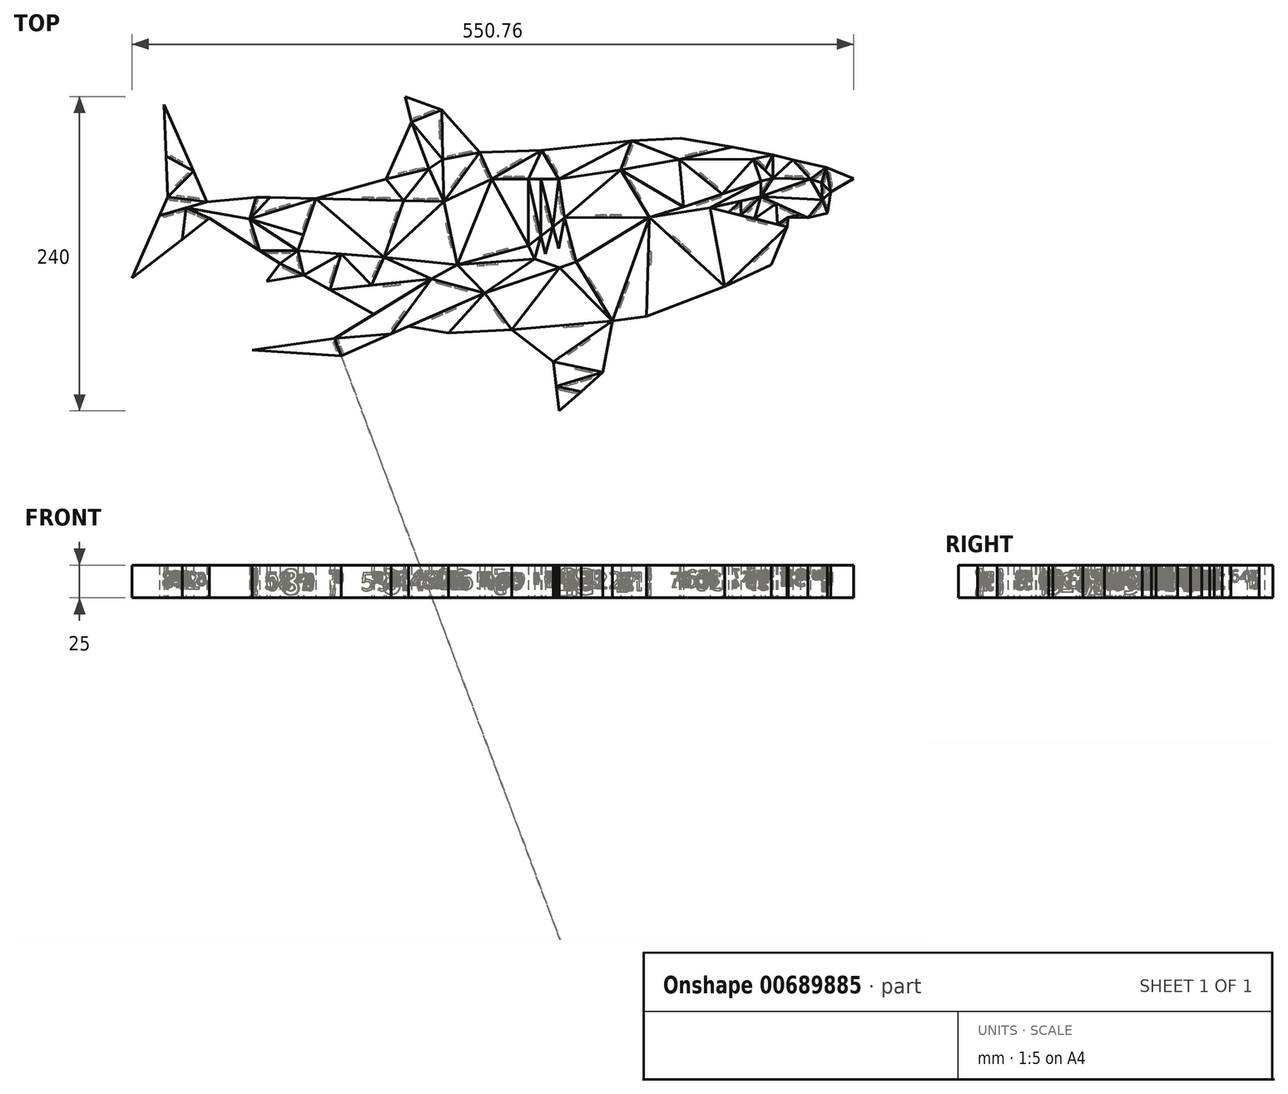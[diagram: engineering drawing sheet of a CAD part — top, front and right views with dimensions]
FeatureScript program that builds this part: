
annotation { "Feature Type Name" : "Feature", "Feature Type Description" : "" }
export const myFeature = defineFeature(function(context is Context, id is Id, definition is map)
    precondition{}
    {
        {
            var Q0;
            Q0=qCreatedBy(makeId("Top.planeOp"),FACE);
            var sketch = newSketch(context, id + "F0", { "sketchPlane" : qUnion([Q0])});
            skLineSegment(sketch, "E0.bottom", {"start": v(-560, -120) * mm, "end": v(560, -120) * mm});
            skLineSegment(sketch, "E0.top", {"start": v(-560, 120) * mm, "end": v(560, 120) * mm});
            skLineSegment(sketch, "E0.left", {"start": v(-560, -120) * mm, "end": v(-560, 120) * mm});
            skLineSegment(sketch, "E0.right", {"start": v(560, -120) * mm, "end": v(560, 120) * mm});
            skPoint(sketch, "E0.middle", {"position": v(0, 0) * mm});
            skLineSegment(sketch, "E1", {"start": v(0, 120) * mm, "end": v(0, -120) * mm});
            skLineSegment(sketch, "E2", {"start": v(-98.5, -25) * mm, "end": v(-62.96, -8.5) * mm});
            skLineSegment(sketch, "E3", {"start": v(-158.02, -47.81) * mm, "end": v(-98.5, -25) * mm});
            skLineSegment(sketch, "E4", {"start": v(-184.16, -51.15) * mm, "end": v(-158.02, -47.81) * mm});
            skLineSegment(sketch, "E5", {"start": v(-191.25, -90.42) * mm, "end": v(-184.16, -51.15) * mm});
            skLineSegment(sketch, "E6", {"start": v(-224.77, -120) * mm, "end": v(-191.25, -90.42) * mm});
            skLineSegment(sketch, "E7", {"start": v(-229.22, -82.3) * mm, "end": v(-224.77, -120) * mm});
            skLineSegment(sketch, "E8", {"start": v(-260.93, -57.82) * mm, "end": v(-229.22, -82.3) * mm});
            skLineSegment(sketch, "E9", {"start": v(-309.32, -60.6) * mm, "end": v(-260.93, -57.82) * mm});
            skLineSegment(sketch, "E10", {"start": v(-458.96, -73.4) * mm, "end": v(-391.1, -77.85) * mm});
            skLineSegment(sketch, "E11", {"start": v(-396.1, -64.5) * mm, "end": v(-458.96, -73.4) * mm});
            skLineSegment(sketch, "E12", {"start": v(-399.7, -27.56) * mm, "end": v(-366.14, -46.09) * mm});
            skLineSegment(sketch, "E13", {"start": v(-419.75, -16.22) * mm, "end": v(-399.7, -27.56) * mm});
            skLineSegment(sketch, "E14", {"start": v(-437.83, -7.4) * mm, "end": v(-419.75, -16.22) * mm});
            skLineSegment(sketch, "E15", {"start": v(-491.8, 27.08) * mm, "end": v(-437.83, -7.4) * mm});
            skLineSegment(sketch, "E16", {"start": v(-526.26, 113.86) * mm, "end": v(-523.5, 43.21) * mm});
            skLineSegment(sketch, "E17", {"start": v(-493.56, 39.57) * mm, "end": v(-526.26, 113.86) * mm});
            skLineSegment(sketch, "E18", {"start": v(-456.3, 42.91) * mm, "end": v(-493.56, 39.57) * mm});
            skLineSegment(sketch, "E19", {"start": v(-445.4, 43.06) * mm, "end": v(-456.3, 42.91) * mm});
            skLineSegment(sketch, "E20", {"start": v(-410.31, 42.07) * mm, "end": v(-445.4, 43.06) * mm});
            skLineSegment(sketch, "E21", {"start": v(-356.91, 57.1) * mm, "end": v(-410.31, 42.07) * mm});
            skLineSegment(sketch, "E22", {"start": v(-337.47, 100.57) * mm, "end": v(-356.91, 57.1) * mm});
            skLineSegment(sketch, "E23", {"start": v(-342.14, 120) * mm, "end": v(-337.47, 100.57) * mm});
            skLineSegment(sketch, "E24", {"start": v(-314.33, 109.61) * mm, "end": v(-342.14, 120) * mm});
            skLineSegment(sketch, "E25", {"start": v(-285.4, 77.35) * mm, "end": v(-314.33, 109.61) * mm});
            skLineSegment(sketch, "E26", {"start": v(-238.12, 79.02) * mm, "end": v(-285.4, 77.35) * mm});
            skLineSegment(sketch, "E27", {"start": v(-169.37, 86.33) * mm, "end": v(-238.12, 79.02) * mm});
            skLineSegment(sketch, "E28", {"start": v(-169.37, 86.33) * mm, "end": v(-132.1, 88) * mm});
            skLineSegment(sketch, "E29", {"start": v(-550.76, -18.53) * mm, "end": v(-491.8, 27.08) * mm});
            skLineSegment(sketch, "E30", {"start": v(-523.5, 43.21) * mm, "end": v(-550.76, -18.53) * mm});
            skLineSegment(sketch, "E31", {"start": v(-314.33, 109.61) * mm, "end": v(-337.47, 100.57) * mm});
            skLineSegment(sketch, "E32", {"start": v(-313.66, 71.78) * mm, "end": v(-285.4, 77.35) * mm});
            skLineSegment(sketch, "E33", {"start": v(-313.66, 71.78) * mm, "end": v(-314.33, 109.61) * mm});
            skLineSegment(sketch, "E34", {"start": v(-313.66, 71.78) * mm, "end": v(-337.47, 100.57) * mm});
            skLineSegment(sketch, "E35", {"start": v(-324.1, 64.88) * mm, "end": v(-313.66, 71.78) * mm});
            skLineSegment(sketch, "E36", {"start": v(-324.1, 64.88) * mm, "end": v(-356.91, 57.1) * mm});
            skLineSegment(sketch, "E37", {"start": v(-324.1, 64.88) * mm, "end": v(-337.47, 100.57) * mm});
            skLineSegment(sketch, "E38", {"start": v(-396.1, -64.5) * mm, "end": v(-391.1, -77.85) * mm});
            skLineSegment(sketch, "E39", {"start": v(-208.01, -105.2) * mm, "end": v(-227, -101.15) * mm});
            skLineSegment(sketch, "E40", {"start": v(-229.22, -82.3) * mm, "end": v(-184.16, -51.15) * mm});
            skLineSegment(sketch, "E41", {"start": v(-191.25, -90.42) * mm, "end": v(-229.22, -82.3) * mm});
            skLineSegment(sketch, "E42", {"start": v(-281.5, -30.01) * mm, "end": v(-391.1, -77.85) * mm});
            skLineSegment(sketch, "E43", {"start": v(-396.1, -64.5) * mm, "end": v(-353.1, -61.27) * mm});
            skLineSegment(sketch, "E44", {"start": v(-322.17, -19.07) * mm, "end": v(-396.1, -64.5) * mm});
            skLineSegment(sketch, "E45", {"start": v(-322.17, -19.07) * mm, "end": v(-353.1, -61.27) * mm});
            skLineSegment(sketch, "E46", {"start": v(-184.16, -51.15) * mm, "end": v(-260.93, -57.82) * mm});
            skLineSegment(sketch, "E47", {"start": v(-21, 65.86) * mm, "end": v(0, 57.32) * mm});
            skLineSegment(sketch, "E48", {"start": v(-61.42, 75.33) * mm, "end": v(-21, 65.86) * mm});
            skLineSegment(sketch, "E49", {"start": v(-92.6, 81.33) * mm, "end": v(-61.42, 75.33) * mm});
            skLineSegment(sketch, "E50", {"start": v(-132.1, 88) * mm, "end": v(-92.6, 81.33) * mm});
            skLineSegment(sketch, "E51", {"start": v(-17.51, 47.28) * mm, "end": v(0, 57.32) * mm});
            skLineSegment(sketch, "E52", {"start": v(-17.51, 47.28) * mm, "end": v(-19.9, 31) * mm});
            skLineSegment(sketch, "E53", {"start": v(-155.69, 27.8) * mm, "end": v(-158.02, -47.81) * mm});
            skLineSegment(sketch, "E54", {"start": v(-155.69, 27.8) * mm, "end": v(-98.5, -25) * mm});
            skLineSegment(sketch, "E55", {"start": v(-177.9, 64) * mm, "end": v(-155.69, 27.8) * mm});
            skLineSegment(sketch, "E56", {"start": v(-177.9, 64) * mm, "end": v(-169.37, 86.33) * mm});
            skLineSegment(sketch, "E57", {"start": v(-17.51, 47.28) * mm, "end": v(-21, 65.86) * mm});
            skLineSegment(sketch, "E58", {"start": v(-34.99, 27.4) * mm, "end": v(-19.9, 31) * mm});
            skLineSegment(sketch, "E59", {"start": v(-49.9, 27.93) * mm, "end": v(-34.99, 27.4) * mm});
            skLineSegment(sketch, "E60", {"start": v(-49.9, 27.93) * mm, "end": v(-50.83, 20.55) * mm});
            skLineSegment(sketch, "E61", {"start": v(-50.83, 20.55) * mm, "end": v(-62.96, -8.5) * mm});
            skLineSegment(sketch, "E62", {"start": v(-50.83, 20.55) * mm, "end": v(-98.5, -25) * mm});
            skLineSegment(sketch, "E63", {"start": v(-109.43, 35.16) * mm, "end": v(-98.5, -25) * mm});
            skLineSegment(sketch, "E64", {"start": v(-109.43, 35.16) * mm, "end": v(-50.83, 20.55) * mm});
            skLineSegment(sketch, "E65", {"start": v(-70.86, 43.59) * mm, "end": v(-34.99, 27.4) * mm});
            skLineSegment(sketch, "E66", {"start": v(-70.86, 43.59) * mm, "end": v(-109.43, 35.16) * mm});
            skLineSegment(sketch, "E67", {"start": v(-503.89, 63.04) * mm, "end": v(-524.72, 74.56) * mm});
            skLineSegment(sketch, "E68", {"start": v(-523.5, 43.21) * mm, "end": v(-503.89, 63.04) * mm});
            skLineSegment(sketch, "E69", {"start": v(-493.56, 39.57) * mm, "end": v(-523.5, 43.21) * mm});
            skLineSegment(sketch, "E70", {"start": v(-509.57, 34.94) * mm, "end": v(-493.56, 39.57) * mm});
            skLineSegment(sketch, "E71", {"start": v(-509.57, 34.94) * mm, "end": v(-491.8, 27.08) * mm});
            skLineSegment(sketch, "E72", {"start": v(-509.57, 34.94) * mm, "end": v(-529.73, 29.1) * mm});
            skLineSegment(sketch, "E73", {"start": v(-509.57, 34.94) * mm, "end": v(-512.54, 11.03) * mm});
            skLineSegment(sketch, "E74", {"start": v(-509.57, 34.94) * mm, "end": v(-461.04, 26.47) * mm});
            skLineSegment(sketch, "E75", {"start": v(-461.04, 26.47) * mm, "end": v(-456.3, 42.91) * mm});
            skLineSegment(sketch, "E76", {"start": v(-445.4, 43.06) * mm, "end": v(-461.04, 26.47) * mm});
            skLineSegment(sketch, "E77", {"start": v(-447.94, -21.09) * mm, "end": v(-437.83, -7.4) * mm});
            skLineSegment(sketch, "E78", {"start": v(-447.94, -21.09) * mm, "end": v(-419.75, -16.22) * mm});
            skLineSegment(sketch, "E79", {"start": v(-461.04, 26.47) * mm, "end": v(-453.35, 2.5) * mm});
            skLineSegment(sketch, "E80", {"start": v(-461.04, 26.47) * mm, "end": v(-410.31, 42.07) * mm});
            skLineSegment(sketch, "E81", {"start": v(-322.17, -19.07) * mm, "end": v(-281.5, -30.01) * mm});
            skLineSegment(sketch, "E82", {"start": v(-260.93, -57.82) * mm, "end": v(-281.5, -30.01) * mm});
            skLineSegment(sketch, "E83", {"start": v(-281.5, -30.01) * mm, "end": v(-309.32, -60.6) * mm});
            skLineSegment(sketch, "E84", {"start": v(-155.69, 27.8) * mm, "end": v(-109.43, 35.16) * mm});
            skLineSegment(sketch, "E85", {"start": v(-155.69, 27.8) * mm, "end": v(-129.84, 35.74) * mm});
            skLineSegment(sketch, "E86", {"start": v(-85.88, 40.3) * mm, "end": v(-85.88, 29.29) * mm});
            skLineSegment(sketch, "E87", {"start": v(-85.88, 29.29) * mm, "end": v(-70.86, 43.59) * mm});
            skLineSegment(sketch, "E88", {"start": v(-70.86, 43.59) * mm, "end": v(-75.52, 26.7) * mm});
            skLineSegment(sketch, "E89", {"start": v(-58.19, 22.38) * mm, "end": v(-49.9, 27.93) * mm});
            skLineSegment(sketch, "E90", {"start": v(-49.9, 27.93) * mm, "end": v(-40.47, 29.87) * mm});
            skLineSegment(sketch, "E91", {"start": v(-17.51, 47.28) * mm, "end": v(-23.8, 41.06) * mm});
            skLineSegment(sketch, "E92", {"start": v(-23.8, 41.06) * mm, "end": v(-34.99, 27.4) * mm});
            skLineSegment(sketch, "E93", {"start": v(-23.8, 41.06) * mm, "end": v(-19.9, 31) * mm});
            skLineSegment(sketch, "E94", {"start": v(-23.8, 41.06) * mm, "end": v(-70.86, 43.59) * mm});
            skLineSegment(sketch, "E95", {"start": v(-24.49, 54.25) * mm, "end": v(-21, 65.86) * mm});
            skLineSegment(sketch, "E96", {"start": v(-24.49, 54.25) * mm, "end": v(-23.8, 41.06) * mm});
            skLineSegment(sketch, "E97", {"start": v(-33, 57) * mm, "end": v(-21, 65.86) * mm});
            skLineSegment(sketch, "E98", {"start": v(-33, 57) * mm, "end": v(-24.49, 54.25) * mm});
            skLineSegment(sketch, "E99", {"start": v(-33, 57) * mm, "end": v(-23.8, 41.06) * mm});
            skLineSegment(sketch, "E100", {"start": v(-70.86, 43.59) * mm, "end": v(-70.86, 55.35) * mm});
            skLineSegment(sketch, "E101", {"start": v(-109.43, 35.16) * mm, "end": v(-70.86, 55.35) * mm});
            skLineSegment(sketch, "E102", {"start": v(-129.84, 35.74) * mm, "end": v(-70.86, 55.35) * mm});
            skLineSegment(sketch, "E103", {"start": v(-129.84, 35.74) * mm, "end": v(-177.9, 64) * mm});
            skLineSegment(sketch, "E104", {"start": v(-129.84, 35.74) * mm, "end": v(-132.83, 71.97) * mm});
            skLineSegment(sketch, "E105", {"start": v(-132.83, 71.97) * mm, "end": v(-169.37, 86.33) * mm});
            skLineSegment(sketch, "E106", {"start": v(-177.9, 64) * mm, "end": v(-132.83, 71.97) * mm});
            skLineSegment(sketch, "E107", {"start": v(-132.83, 71.97) * mm, "end": v(-92.6, 81.33) * mm});
            skLineSegment(sketch, "E108", {"start": v(-76.54, 72.24) * mm, "end": v(-61.42, 75.33) * mm});
            skLineSegment(sketch, "E109", {"start": v(-76.54, 72.24) * mm, "end": v(-132.83, 71.97) * mm});
            skLineSegment(sketch, "E110", {"start": v(-76.54, 72.24) * mm, "end": v(-70.86, 55.35) * mm});
            skLineSegment(sketch, "E111", {"start": v(-132.83, 71.97) * mm, "end": v(-100.35, 45.54) * mm});
            skLineSegment(sketch, "E112", {"start": v(-61.42, 57.63) * mm, "end": v(-70.86, 55.35) * mm});
            skLineSegment(sketch, "E113", {"start": v(-61.42, 57.63) * mm, "end": v(-33, 57) * mm});
            skLineSegment(sketch, "E114", {"start": v(-61.42, 57.63) * mm, "end": v(-61.42, 75.33) * mm});
            skLineSegment(sketch, "E115", {"start": v(-61.42, 57.63) * mm, "end": v(-76.54, 72.24) * mm});
            skLineSegment(sketch, "E116", {"start": v(-61.42, 75.33) * mm, "end": v(-67.65, 63.65) * mm});
            skLineSegment(sketch, "E117", {"start": v(-61.42, 57.63) * mm, "end": v(-46.15, 71.75) * mm});
            skLineSegment(sketch, "E118", {"start": v(-225.14, 56.85) * mm, "end": v(-177.9, 64) * mm});
            skLineSegment(sketch, "E119", {"start": v(-225.14, 56.85) * mm, "end": v(-238.12, 79.02) * mm});
            skLineSegment(sketch, "E120", {"start": v(-225.14, 56.85) * mm, "end": v(-169.37, 86.33) * mm});
            skLineSegment(sketch, "E121", {"start": v(-276.28, 56.87) * mm, "end": v(-285.4, 77.35) * mm});
            skLineSegment(sketch, "E122", {"start": v(-276.28, 56.87) * mm, "end": v(-225.14, 56.85) * mm});
            skLineSegment(sketch, "E123", {"start": v(-238.12, 79.02) * mm, "end": v(-276.28, 56.87) * mm});
            skLineSegment(sketch, "E124", {"start": v(-312.55, 39.84) * mm, "end": v(-313.66, 71.78) * mm});
            skLineSegment(sketch, "E125", {"start": v(-312.55, 39.84) * mm, "end": v(-276.28, 56.87) * mm});
            skLineSegment(sketch, "E126", {"start": v(-312.55, 39.84) * mm, "end": v(-285.4, 77.35) * mm});
            skLineSegment(sketch, "E127", {"start": v(-302.43, -8.43) * mm, "end": v(-276.28, 56.87) * mm});
            skLineSegment(sketch, "E128", {"start": v(-302.43, -8.43) * mm, "end": v(-281.5, -30.01) * mm});
            skLineSegment(sketch, "E129", {"start": v(-302.43, -8.43) * mm, "end": v(-322.17, -19.07) * mm});
            skLineSegment(sketch, "E130", {"start": v(-302.43, -8.43) * mm, "end": v(-312.55, 39.84) * mm});
            skLineSegment(sketch, "E131", {"start": v(-302.43, -8.43) * mm, "end": v(-248.23, 6.09) * mm});
            skLineSegment(sketch, "E132", {"start": v(-248.23, 6.09) * mm, "end": v(-276.28, 56.87) * mm});
            skLineSegment(sketch, "E133", {"start": v(-184.16, -51.15) * mm, "end": v(-155.69, 27.8) * mm});
            skLineSegment(sketch, "E134", {"start": v(-248.23, 6.09) * mm, "end": v(-220.7, 27.33) * mm});
            skLineSegment(sketch, "E135", {"start": v(-220.7, 27.33) * mm, "end": v(-155.69, 27.8) * mm});
            skLineSegment(sketch, "E136", {"start": v(-211.69, -6.17) * mm, "end": v(-155.69, 27.8) * mm});
            skLineSegment(sketch, "E137", {"start": v(-211.69, -6.17) * mm, "end": v(-220.7, 27.33) * mm});
            skLineSegment(sketch, "E138", {"start": v(-225.14, 56.85) * mm, "end": v(-220.7, 27.33) * mm});
            skLineSegment(sketch, "E139", {"start": v(-260.93, -57.82) * mm, "end": v(-224.52, -10.66) * mm});
            skLineSegment(sketch, "E140", {"start": v(-224.52, -10.66) * mm, "end": v(-184.16, -51.15) * mm});
            skLineSegment(sketch, "E141", {"start": v(-224.52, -10.66) * mm, "end": v(-211.69, -6.17) * mm});
            skLineSegment(sketch, "E142", {"start": v(-211.69, -6.17) * mm, "end": v(-184.16, -51.15) * mm});
            skLineSegment(sketch, "E143", {"start": v(-248.23, 6.09) * mm, "end": v(-248.23, 56.86) * mm});
            skLineSegment(sketch, "E144", {"start": v(-238.12, 79.02) * mm, "end": v(-248.23, 56.86) * mm});
            skLineSegment(sketch, "E145", {"start": v(-224.52, -10.66) * mm, "end": v(-243.56, -4.04) * mm});
            skLineSegment(sketch, "E146", {"start": v(-243.56, -4.04) * mm, "end": v(-248.23, 6.09) * mm});
            skLineSegment(sketch, "E147", {"start": v(-281.5, -30.01) * mm, "end": v(-243.56, -4.04) * mm});
            skLineSegment(sketch, "E148", {"start": v(-343.48, 40.35) * mm, "end": v(-410.31, 42.07) * mm});
            skLineSegment(sketch, "E149", {"start": v(-324.1, 64.88) * mm, "end": v(-343.48, 40.35) * mm});
            skLineSegment(sketch, "E150", {"start": v(-343.48, 40.35) * mm, "end": v(-356.91, 57.1) * mm});
            skLineSegment(sketch, "E151", {"start": v(-324.1, 64.88) * mm, "end": v(-312.55, 39.84) * mm});
            skLineSegment(sketch, "E152", {"start": v(-343.48, 40.35) * mm, "end": v(-312.55, 39.84) * mm});
            skLineSegment(sketch, "E153", {"start": v(-399.7, -27.56) * mm, "end": v(-322.17, -19.07) * mm});
            skLineSegment(sketch, "E154", {"start": v(-309.32, -60.6) * mm, "end": v(-339.75, -55.44) * mm});
            skLineSegment(sketch, "E155", {"start": v(-358.3, -2.7) * mm, "end": v(-322.17, -19.07) * mm});
            skLineSegment(sketch, "E156", {"start": v(-358.3, -2.7) * mm, "end": v(-302.43, -8.43) * mm});
            skLineSegment(sketch, "E157", {"start": v(-343.48, 40.35) * mm, "end": v(-358.3, -2.7) * mm});
            skLineSegment(sketch, "E158", {"start": v(-358.3, -2.7) * mm, "end": v(-410.31, 42.07) * mm});
            skLineSegment(sketch, "E159", {"start": v(-453.35, 2.5) * mm, "end": v(-424.06, 2.5) * mm});
            skLineSegment(sketch, "E160", {"start": v(-424.06, 2.5) * mm, "end": v(-419.75, -16.22) * mm});
            skLineSegment(sketch, "E161", {"start": v(-424.06, 2.5) * mm, "end": v(-437.83, -7.4) * mm});
            skLineSegment(sketch, "E162", {"start": v(-424.06, 2.5) * mm, "end": v(-410.31, 42.07) * mm});
            skLineSegment(sketch, "E163", {"start": v(-461.04, 26.47) * mm, "end": v(-419.87, 14.57) * mm});
            skLineSegment(sketch, "E164", {"start": v(-424.06, 2.5) * mm, "end": v(-358.3, -2.7) * mm});
            skLineSegment(sketch, "E165", {"start": v(-419.75, -16.22) * mm, "end": v(-391.18, -0.1) * mm});
            skLineSegment(sketch, "E166", {"start": v(-391.18, -0.1) * mm, "end": v(-399.7, -27.56) * mm});
            skLineSegment(sketch, "E167", {"start": v(-58.19, 22.38) * mm, "end": v(-58.84, 38.16) * mm});
            skLineSegment(sketch, "E168", {"start": v(-58.84, 38.16) * mm, "end": v(-75.52, 26.7) * mm});
            skLineSegment(sketch, "E169", {"start": v(-200.98, -99) * mm, "end": v(-21, -99) * mm});
            skLineSegment(sketch, "E170", {"start": v(-21, -99) * mm, "end": v(0, -120) * mm});
            skLineSegment(sketch, "E171", {"start": v(-21, -99) * mm, "end": v(-21, 30.74) * mm});
            skLineSegment(sketch, "E172", {"start": v(-21, 99) * mm, "end": v(-21, 65.86) * mm});
            skLineSegment(sketch, "E173", {"start": v(-21, 99) * mm, "end": v(0, 120) * mm});
            skLineSegment(sketch, "E174", {"start": v(-21, 99) * mm, "end": v(-304.81, 99) * mm});
            skLineSegment(sketch, "E175", {"start": v(-519.72, 99) * mm, "end": v(-338.17, 99) * mm});
            skLineSegment(sketch, "E176", {"start": v(-539, 99) * mm, "end": v(-525.68, 99) * mm});
            skLineSegment(sketch, "E177", {"start": v(-539, 99) * mm, "end": v(-560, 120) * mm});
            skLineSegment(sketch, "E178", {"start": v(-539, -99) * mm, "end": v(-539, -9.44) * mm});
            skLineSegment(sketch, "E179", {"start": v(-539, -99) * mm, "end": v(-227.25, -99) * mm});
            skLineSegment(sketch, "E180", {"start": v(-539, -99) * mm, "end": v(-560, -120) * mm});
            skLineSegment(sketch, "E181", {"start": v(-539, 99) * mm, "end": v(-539, 8.1) * mm});
            skLineSegment(sketch, "E182", {"start": v(-238.79, 13.37) * mm, "end": v(-248.23, 56.86) * mm});
            skLineSegment(sketch, "E183", {"start": v(-238.79, 13.37) * mm, "end": v(-243.56, -4.04) * mm});
            skLineSegment(sketch, "E184", {"start": v(-238.79, 56.86) * mm, "end": v(-238.79, 13.37) * mm});
            skLineSegment(sketch, "E185", {"start": v(-238.79, 56.86) * mm, "end": v(-229.63, 20.44) * mm});
            skLineSegment(sketch, "E186", {"start": v(-229.63, 20.44) * mm, "end": v(-225.14, 56.85) * mm});
            skLineSegment(sketch, "E187", {"start": v(-220.7, 27.33) * mm, "end": v(-225.14, 4.02) * mm});
            skLineSegment(sketch, "E188", {"start": v(-225.14, 4.02) * mm, "end": v(-229.63, 20.44) * mm});
            skLineSegment(sketch, "E189", {"start": v(-238.79, 13.37) * mm, "end": v(-235.13, 0) * mm});
            skLineSegment(sketch, "E190", {"start": v(-235.13, 0) * mm, "end": v(-229.63, 20.44) * mm});
            skLineSegment(sketch, "E191", {"start": v(-76.54, 72.24) * mm, "end": v(-100.35, 45.54) * mm});
            skLineSegment(sketch, "E192", {"start": v(-46.15, 71.75) * mm, "end": v(-33, 57) * mm});
            skLineSegment(sketch, "E193", {"start": v(-70.86, 43.59) * mm, "end": v(-33, 57) * mm});
            skLineSegment(sketch, "E194", {"start": v(-220.7, 27.33) * mm, "end": v(-177.9, 64) * mm});
            skLineSegment(sketch, "E195", {"start": v(-302.43, -8.43) * mm, "end": v(-243.56, -4.04) * mm});
            skLineSegment(sketch, "E196", {"start": v(-281.5, -30.01) * mm, "end": v(-224.52, -10.66) * mm});
            skLineSegment(sketch, "E197", {"start": v(-312.55, 39.84) * mm, "end": v(-358.3, -2.7) * mm});
            skLineSegment(sketch, "E198", {"start": v(-358.3, -2.7) * mm, "end": v(-367.99, -24.09) * mm});
            skLineSegment(sketch, "E199", {"start": v(-367.99, -24.09) * mm, "end": v(-391.18, -0.1) * mm});
            skLineSegment(sketch, "E200", {"start": v(-191.25, -90.42) * mm, "end": v(-227, -101.15) * mm});
            skLineSegment(sketch, "E201", {"start": v(-17.51, 47.28) * mm, "end": v(-24.49, 54.25) * mm});
            skLineSegment(sketch, "E202", {"start": v(-85.88, 40.3) * mm, "end": v(-95.55, 31.7) * mm});
            skLineSegment(sketch, "E203", {"start": v(-70.86, 43.59) * mm, "end": v(-61.42, 57.63) * mm});
            skLineSegment(sketch, "E204", {"start": v(-461.04, 26.47) * mm, "end": v(-424.06, 2.5) * mm});
            skSolve(sketch);
        }
        {
            var Q0;
            {var subQ0=sQuery(id+"F0.wireOp",EDGE,"E67");Q0=makeQuery(id+"F0.imprint","IMPRINT",FACE,{"disambiguationData":[TD([[makeQuery(id+"F0.imprint","IMPRINT",EDGE,{"derivedFrom":subQ0}),-1.0]])]});}
            var Q1;
            {var subQ2=sQuery(id+"F0.wireOp",EDGE,"E68");Q1=makeQuery(id+"F0.imprint","IMPRINT",FACE,{"disambiguationData":[TD([[makeQuery(id+"F0.imprint","IMPRINT",EDGE,{"derivedFrom":subQ2}),-1.0]])]});}
            var Q2;
            {var subQ0=sQuery(id+"F0.wireOp",EDGE,"E72");Q2=makeQuery(id+"F0.imprint","IMPRINT",FACE,{"disambiguationData":[TD([[makeQuery(id+"F0.imprint","IMPRINT",EDGE,{"derivedFrom":subQ0}),1.0]])]});}
            var Q3;
            {var subQ0=sQuery(id+"F0.wireOp",EDGE,"E71");Q3=makeQuery(id+"F0.imprint","IMPRINT",FACE,{"disambiguationData":[TD([[makeQuery(id+"F0.imprint","IMPRINT",EDGE,{"derivedFrom":subQ0}),1.0]])]});}
            var Q4;
            Q4=makeQuery(id+"F0.imprint","IMPRINT",FACE,{"disambiguationData":[TD([[makeQuery(id+"F0.imprint","IMPRINT",EDGE,{"derivedFrom":sQuery(id+"F0.wireOp",EDGE,"E19")}),1.0]])]});
            var Q5;
            {var subQ0=sQuery(id+"F0.wireOp",EDGE,"E80");Q5=makeQuery(id+"F0.imprint","IMPRINT",FACE,{"disambiguationData":[TD([[makeQuery(id+"F0.imprint","IMPRINT",EDGE,{"derivedFrom":subQ0}),-1.0]])]});}
            var Q6;
            {var subQ2=sQuery(id+"F0.wireOp",EDGE,"E159");Q6=makeQuery(id+"F0.imprint","IMPRINT",FACE,{"disambiguationData":[TD([[makeQuery(id+"F0.imprint","IMPRINT",EDGE,{"derivedFrom":subQ2}),-1.0]])]});}
            var Q7;
            Q7=makeQuery(id+"F0.imprint","IMPRINT",FACE,{"disambiguationData":[TD([[makeQuery(id+"F0.imprint","IMPRINT",EDGE,{"derivedFrom":sQuery(id+"F0.wireOp",EDGE,"E14")}),-1.0]])]});
            var Q8;
            Q8=makeQuery(id+"F0.imprint","IMPRINT",FACE,{"disambiguationData":[TD([[makeQuery(id+"F0.imprint","IMPRINT",EDGE,{"derivedFrom":sQuery(id+"F0.wireOp",EDGE,"E13")}),1.0]])]});
            var Q9;
            Q9=makeQuery(id+"F0.imprint","IMPRINT",FACE,{"disambiguationData":[TD([[makeQuery(id+"F0.imprint","IMPRINT",EDGE,{"derivedFrom":sQuery(id+"F0.wireOp",EDGE,"E148")}),1.0]])]});
            var Q10;
            Q10=makeQuery(id+"F0.imprint","IMPRINT",FACE,{"disambiguationData":[TD([[makeQuery(id+"F0.imprint","IMPRINT",EDGE,{"derivedFrom":sQuery(id+"F0.wireOp",EDGE,"E23")}),1.0]])]});
            var Q11;
            {var subQ3=sQuery(id+"F0.wireOp",EDGE,"E36");Q11=makeQuery(id+"F0.imprint","IMPRINT",FACE,{"disambiguationData":[TD([[makeQuery(id+"F0.imprint","IMPRINT",EDGE,{"derivedFrom":subQ3}),-1.0]])]});}
            var Q12;
            Q12=makeQuery(id+"F0.imprint","IMPRINT",FACE,{"disambiguationData":[TD([[makeQuery(id+"F0.imprint","IMPRINT",EDGE,{"derivedFrom":sQuery(id+"F0.wireOp",EDGE,"E149")}),1.0]])]});
            var Q13;
            {var subQ0=sQuery(id+"F0.wireOp",EDGE,"E198");Q13=makeQuery(id+"F0.imprint","IMPRINT",FACE,{"disambiguationData":[TD([[makeQuery(id+"F0.imprint","IMPRINT",EDGE,{"derivedFrom":subQ0}),-1.0]])]});}
            var Q14;
            {var subQ0=sQuery(id+"F0.wireOp",EDGE,"E12");Q14=makeQuery(id+"F0.imprint","IMPRINT",FACE,{"disambiguationData":[TD([[makeQuery(id+"F0.imprint","IMPRINT",EDGE,{"derivedFrom":subQ0}),1.0]])]});}
            var Q15;
            {var subQ0=sQuery(id+"F0.wireOp",EDGE,"E38");Q15=makeQuery(id+"F0.imprint","IMPRINT",FACE,{"disambiguationData":[TD([[makeQuery(id+"F0.imprint","IMPRINT",EDGE,{"derivedFrom":subQ0}),1.0]])]});}
            var Q16;
            {var subQ3=sQuery(id+"F0.wireOp",EDGE,"E45");Q16=makeQuery(id+"F0.imprint","IMPRINT",FACE,{"disambiguationData":[TD([[makeQuery(id+"F0.imprint","IMPRINT",EDGE,{"derivedFrom":subQ3}),1.0]])]});}
            var Q17;
            Q17=makeQuery(id+"F0.imprint","IMPRINT",FACE,{"disambiguationData":[TD([[makeQuery(id+"F0.imprint","IMPRINT",EDGE,{"derivedFrom":sQuery(id+"F0.wireOp",EDGE,"E130")}),1.0]])]});
            var Q18;
            {var subQ0=sQuery(id+"F0.wireOp",EDGE,"E32");Q18=makeQuery(id+"F0.imprint","IMPRINT",FACE,{"disambiguationData":[TD([[makeQuery(id+"F0.imprint","IMPRINT",EDGE,{"derivedFrom":subQ0}),1.0]])]});}
            var Q19;
            Q19=makeQuery(id+"F0.imprint","IMPRINT",FACE,{"disambiguationData":[TD([[makeQuery(id+"F0.imprint","IMPRINT",EDGE,{"derivedFrom":sQuery(id+"F0.wireOp",EDGE,"E121")}),1.0]])]});
            var Q20;
            Q20=makeQuery(id+"F0.imprint","IMPRINT",FACE,{"disambiguationData":[TD([[makeQuery(id+"F0.imprint","IMPRINT",EDGE,{"derivedFrom":sQuery(id+"F0.wireOp",EDGE,"E127")}),-1.0]])]});
            var Q21;
            {var subQ0=sQuery(id+"F0.wireOp",EDGE,"E123");Q21=makeQuery(id+"F0.imprint","IMPRINT",FACE,{"disambiguationData":[TD([[makeQuery(id+"F0.imprint","IMPRINT",EDGE,{"derivedFrom":subQ0}),1.0]])]});}
            var Q22;
            Q22=makeQuery(id+"F0.imprint","IMPRINT",FACE,{"disambiguationData":[TD([[makeQuery(id+"F0.imprint","IMPRINT",EDGE,{"derivedFrom":sQuery(id+"F0.wireOp",EDGE,"E128")}),1.0]])]});
            var Q23;
            Q23=makeQuery(id+"F0.imprint","IMPRINT",FACE,{"disambiguationData":[TD([[makeQuery(id+"F0.imprint","IMPRINT",EDGE,{"derivedFrom":sQuery(id+"F0.wireOp",EDGE,"E9")}),1.0]])]});
            var Q24;
            {var subQ3=sQuery(id+"F0.wireOp",EDGE,"E39");Q24=makeQuery(id+"F0.imprint","IMPRINT",FACE,{"disambiguationData":[TD([[makeQuery(id+"F0.imprint","IMPRINT",EDGE,{"derivedFrom":subQ3}),1.0]])]});}
            var Q25;
            {var subQ0=sQuery(id+"F0.wireOp",EDGE,"E41");Q25=makeQuery(id+"F0.imprint","IMPRINT",FACE,{"disambiguationData":[TD([[makeQuery(id+"F0.imprint","IMPRINT",EDGE,{"derivedFrom":subQ0}),1.0]])]});}
            var Q26;
            Q26=makeQuery(id+"F0.imprint","IMPRINT",FACE,{"disambiguationData":[TD([[makeQuery(id+"F0.imprint","IMPRINT",EDGE,{"derivedFrom":sQuery(id+"F0.wireOp",EDGE,"E8")}),1.0]])]});
            var Q27;
            Q27=makeQuery(id+"F0.imprint","IMPRINT",FACE,{"disambiguationData":[TD([[makeQuery(id+"F0.imprint","IMPRINT",EDGE,{"derivedFrom":sQuery(id+"F0.wireOp",EDGE,"E137")}),1.0]])]});
            var Q28;
            {var subQ0=sQuery(id+"F0.wireOp",EDGE,"E143");Q28=makeQuery(id+"F0.imprint","IMPRINT",FACE,{"disambiguationData":[TD([[makeQuery(id+"F0.imprint","IMPRINT",EDGE,{"derivedFrom":subQ0}),-1.0]])]});}
            var Q29;
            {var subQ0=sQuery(id+"F0.wireOp",EDGE,"E184");Q29=makeQuery(id+"F0.imprint","IMPRINT",FACE,{"disambiguationData":[TD([[makeQuery(id+"F0.imprint","IMPRINT",EDGE,{"derivedFrom":subQ0}),1.0]])]});}
            var Q30;
            {var subQ0=sQuery(id+"F0.wireOp",EDGE,"E138");Q30=makeQuery(id+"F0.imprint","IMPRINT",FACE,{"disambiguationData":[TD([[makeQuery(id+"F0.imprint","IMPRINT",EDGE,{"derivedFrom":subQ0}),-1.0]])]});}
            var Q31;
            Q31=makeQuery(id+"F0.imprint","IMPRINT",FACE,{"disambiguationData":[TD([[makeQuery(id+"F0.imprint","IMPRINT",EDGE,{"derivedFrom":sQuery(id+"F0.wireOp",EDGE,"E27")}),1.0]])]});
            var Q32;
            Q32=makeQuery(id+"F0.imprint","IMPRINT",FACE,{"disambiguationData":[TD([[makeQuery(id+"F0.imprint","IMPRINT",EDGE,{"derivedFrom":sQuery(id+"F0.wireOp",EDGE,"E56")}),-1.0]])]});
            var Q33;
            Q33=makeQuery(id+"F0.imprint","IMPRINT",FACE,{"disambiguationData":[TD([[makeQuery(id+"F0.imprint","IMPRINT",EDGE,{"derivedFrom":sQuery(id+"F0.wireOp",EDGE,"E55")}),-1.0]])]});
            var Q34;
            Q34=makeQuery(id+"F0.imprint","IMPRINT",FACE,{"disambiguationData":[TD([[makeQuery(id+"F0.imprint","IMPRINT",EDGE,{"derivedFrom":sQuery(id+"F0.wireOp",EDGE,"E133")}),1.0]])]});
            var Q35;
            Q35=makeQuery(id+"F0.imprint","IMPRINT",FACE,{"disambiguationData":[TD([[makeQuery(id+"F0.imprint","IMPRINT",EDGE,{"derivedFrom":sQuery(id+"F0.wireOp",EDGE,"E3")}),1.0]])]});
            var Q36;
            Q36=makeQuery(id+"F0.imprint","IMPRINT",FACE,{"disambiguationData":[TD([[makeQuery(id+"F0.imprint","IMPRINT",EDGE,{"derivedFrom":sQuery(id+"F0.wireOp",EDGE,"E84")}),1.0]])]});
            var Q37;
            {var subQ4=sQuery(id+"F0.wireOp",EDGE,"E62");Q37=makeQuery(id+"F0.imprint","IMPRINT",FACE,{"disambiguationData":[TD([[makeQuery(id+"F0.imprint","IMPRINT",EDGE,{"derivedFrom":subQ4}),-1.0]])]});}
            var Q38;
            Q38=makeQuery(id+"F0.imprint","IMPRINT",FACE,{"disambiguationData":[TD([[makeQuery(id+"F0.imprint","IMPRINT",EDGE,{"derivedFrom":sQuery(id+"F0.wireOp",EDGE,"E109")}),1.0]])]});
            var Q39;
            {var subQ0=sQuery(id+"F0.wireOp",EDGE,"E108");Q39=makeQuery(id+"F0.imprint","IMPRINT",FACE,{"disambiguationData":[TD([[makeQuery(id+"F0.imprint","IMPRINT",EDGE,{"derivedFrom":subQ0}),-1.0]])]});}
            var Q40;
            Q40=makeQuery(id+"F0.imprint","IMPRINT",FACE,{"disambiguationData":[TD([[makeQuery(id+"F0.imprint","IMPRINT",EDGE,{"derivedFrom":sQuery(id+"F0.wireOp",EDGE,"E100")}),-1.0]])]});
            var Q41;
            {var subQ2=sQuery(id+"F0.wireOp",EDGE,"E86");Q41=makeQuery(id+"F0.imprint","IMPRINT",FACE,{"disambiguationData":[TD([[makeQuery(id+"F0.imprint","IMPRINT",EDGE,{"derivedFrom":subQ2}),1.0]])]});}
            var Q42;
            {var subQ0=sQuery(id+"F0.wireOp",EDGE,"E88");Q42=makeQuery(id+"F0.imprint","IMPRINT",FACE,{"disambiguationData":[TD([[makeQuery(id+"F0.imprint","IMPRINT",EDGE,{"derivedFrom":subQ0}),1.0]])]});}
            var Q43;
            Q43=makeQuery(id+"F0.imprint","IMPRINT",FACE,{"disambiguationData":[TD([[makeQuery(id+"F0.imprint","IMPRINT",EDGE,{"derivedFrom":sQuery(id+"F0.wireOp",EDGE,"E89")}),1.0]])]});
            var Q44;
            Q44=makeQuery(id+"F0.imprint","IMPRINT",FACE,{"disambiguationData":[TD([[makeQuery(id+"F0.imprint","IMPRINT",EDGE,{"derivedFrom":sQuery(id+"F0.wireOp",EDGE,"E94")}),-1.0]])]});
            var Q45;
            Q45=makeQuery(id+"F0.imprint","IMPRINT",FACE,{"disambiguationData":[TD([[makeQuery(id+"F0.imprint","IMPRINT",EDGE,{"derivedFrom":sQuery(id+"F0.wireOp",EDGE,"E113")}),1.0]])]});
            var Q46;
            Q46=makeQuery(id+"F0.imprint","IMPRINT",FACE,{"disambiguationData":[TD([[makeQuery(id+"F0.imprint","IMPRINT",EDGE,{"derivedFrom":sQuery(id+"F0.wireOp",EDGE,"E95")}),1.0]])]});
            var Q47;
            Q47=makeQuery(id+"F0.imprint","IMPRINT",FACE,{"disambiguationData":[TD([[makeQuery(id+"F0.imprint","IMPRINT",EDGE,{"derivedFrom":sQuery(id+"F0.wireOp",EDGE,"E47")}),-1.0]])]});
            var Q48;
            Q48=makeQuery(id+"F0.imprint","IMPRINT",FACE,{"disambiguationData":[TD([[makeQuery(id+"F0.imprint","IMPRINT",EDGE,{"derivedFrom":sQuery(id+"F0.wireOp",EDGE,"E91")}),-1.0]])]});
            var Q49;
            {var subQ0=sQuery(id+"F0.wireOp",EDGE,"E92");Q49=makeQuery(id+"F0.imprint","IMPRINT",FACE,{"disambiguationData":[TD([[makeQuery(id+"F0.imprint","IMPRINT",EDGE,{"derivedFrom":subQ0}),1.0]])]});}
            extrude(context, id + "F1", {"entities" : qUnion([Q0, Q1, Q2, Q3, Q4, Q5, Q6, Q7, Q8, Q9, Q10, Q11, Q12, Q13, Q14, Q15, Q16, Q17, Q18, Q19, Q20, Q21, Q22, Q23, Q24, Q25, Q26, Q27, Q28, Q29, Q30, Q31, Q32, Q33, Q34, Q35, Q36, Q37, Q38, Q39, Q40, Q41, Q42, Q43, Q44, Q45, Q46, Q47, Q48, Q49]), "depth" : 25 * mm, "offsetDistance" : 25 * mm});
        }
        {
            var Q0;
            {var subQ2=sQuery(id+"F0.wireOp",EDGE,"E67");Q0=makeQuery(id+"F0.imprint","IMPRINT",FACE,{"disambiguationData":[TD([[makeQuery(id+"F0.imprint","IMPRINT",EDGE,{"derivedFrom":subQ2}),1.0]])]});}
            var Q1;
            {var subQ0=sQuery(id+"F0.wireOp",EDGE,"E69");Q1=makeQuery(id+"F0.imprint","IMPRINT",FACE,{"disambiguationData":[TD([[makeQuery(id+"F0.imprint","IMPRINT",EDGE,{"derivedFrom":subQ0}),1.0]])]});}
            var Q2;
            {var subQ0=sQuery(id+"F0.wireOp",EDGE,"E71");Q2=makeQuery(id+"F0.imprint","IMPRINT",FACE,{"disambiguationData":[TD([[makeQuery(id+"F0.imprint","IMPRINT",EDGE,{"derivedFrom":subQ0}),-1.0]])]});}
            var Q3;
            Q3=makeQuery(id+"F0.imprint","IMPRINT",FACE,{"disambiguationData":[TD([[makeQuery(id+"F0.imprint","IMPRINT",EDGE,{"derivedFrom":sQuery(id+"F0.wireOp",EDGE,"E20")}),1.0]])]});
            var Q4;
            Q4=makeQuery(id+"F0.imprint","IMPRINT",FACE,{"disambiguationData":[TD([[makeQuery(id+"F0.imprint","IMPRINT",EDGE,{"derivedFrom":sQuery(id+"F0.wireOp",EDGE,"E14")}),1.0]])]});
            var Q5;
            {var subQ0=sQuery(id+"F0.wireOp",EDGE,"E166");Q5=makeQuery(id+"F0.imprint","IMPRINT",FACE,{"disambiguationData":[TD([[makeQuery(id+"F0.imprint","IMPRINT",EDGE,{"derivedFrom":subQ0}),1.0]])]});}
            var Q6;
            {var subQ0=sQuery(id+"F0.wireOp",EDGE,"E155");Q6=makeQuery(id+"F0.imprint","IMPRINT",FACE,{"disambiguationData":[TD([[makeQuery(id+"F0.imprint","IMPRINT",EDGE,{"derivedFrom":subQ0}),-1.0]])]});}
            var Q7;
            Q7=makeQuery(id+"F0.imprint","IMPRINT",FACE,{"disambiguationData":[TD([[makeQuery(id+"F0.imprint","IMPRINT",EDGE,{"derivedFrom":sQuery(id+"F0.wireOp",EDGE,"E152")}),-1.0]])]});
            var Q8;
            Q8=makeQuery(id+"F0.imprint","IMPRINT",FACE,{"disambiguationData":[TD([[makeQuery(id+"F0.imprint","IMPRINT",EDGE,{"derivedFrom":sQuery(id+"F0.wireOp",EDGE,"E21")}),1.0]])]});
            var Q9;
            Q9=makeQuery(id+"F0.imprint","IMPRINT",FACE,{"disambiguationData":[TD([[makeQuery(id+"F0.imprint","IMPRINT",EDGE,{"derivedFrom":sQuery(id+"F0.wireOp",EDGE,"E31")}),1.0]])]});
            var Q10;
            Q10=makeQuery(id+"F0.imprint","IMPRINT",FACE,{"disambiguationData":[TD([[makeQuery(id+"F0.imprint","IMPRINT",EDGE,{"derivedFrom":sQuery(id+"F0.wireOp",EDGE,"E32")}),-1.0]])]});
            var Q11;
            Q11=makeQuery(id+"F0.imprint","IMPRINT",FACE,{"disambiguationData":[TD([[makeQuery(id+"F0.imprint","IMPRINT",EDGE,{"derivedFrom":sQuery(id+"F0.wireOp",EDGE,"E125")}),-1.0]])]});
            var Q12;
            Q12=makeQuery(id+"F0.imprint","IMPRINT",FACE,{"disambiguationData":[TD([[makeQuery(id+"F0.imprint","IMPRINT",EDGE,{"derivedFrom":sQuery(id+"F0.wireOp",EDGE,"E10")}),1.0]])]});
            var Q13;
            {var subQ0=sQuery(id+"F0.wireOp",EDGE,"E43");Q13=makeQuery(id+"F0.imprint","IMPRINT",FACE,{"disambiguationData":[TD([[makeQuery(id+"F0.imprint","IMPRINT",EDGE,{"derivedFrom":subQ0}),1.0]])]});}
            var Q14;
            Q14=makeQuery(id+"F0.imprint","IMPRINT",FACE,{"disambiguationData":[TD([[makeQuery(id+"F0.imprint","IMPRINT",EDGE,{"derivedFrom":sQuery(id+"F0.wireOp",EDGE,"E81")}),1.0]])]});
            var Q15;
            {var subQ0=sQuery(id+"F0.wireOp",EDGE,"E83");Q15=makeQuery(id+"F0.imprint","IMPRINT",FACE,{"disambiguationData":[TD([[makeQuery(id+"F0.imprint","IMPRINT",EDGE,{"derivedFrom":subQ0}),-1.0]])]});}
            var Q16;
            Q16=makeQuery(id+"F0.imprint","IMPRINT",FACE,{"disambiguationData":[TD([[makeQuery(id+"F0.imprint","IMPRINT",EDGE,{"derivedFrom":sQuery(id+"F0.wireOp",EDGE,"E131")}),-1.0]])]});
            var Q17;
            Q17=makeQuery(id+"F0.imprint","IMPRINT",FACE,{"disambiguationData":[TD([[makeQuery(id+"F0.imprint","IMPRINT",EDGE,{"derivedFrom":sQuery(id+"F0.wireOp",EDGE,"E82")}),-1.0]])]});
            var Q18;
            Q18=makeQuery(id+"F0.imprint","IMPRINT",FACE,{"disambiguationData":[TD([[makeQuery(id+"F0.imprint","IMPRINT",EDGE,{"derivedFrom":sQuery(id+"F0.wireOp",EDGE,"E140")}),1.0]])]});
            var Q19;
            Q19=makeQuery(id+"F0.imprint","IMPRINT",FACE,{"disambiguationData":[TD([[makeQuery(id+"F0.imprint","IMPRINT",EDGE,{"derivedFrom":sQuery(id+"F0.wireOp",EDGE,"E5")}),1.0]])]});
            var Q20;
            {var subQ0=sQuery(id+"F0.wireOp",EDGE,"E39");Q20=makeQuery(id+"F0.imprint","IMPRINT",FACE,{"disambiguationData":[TD([[makeQuery(id+"F0.imprint","IMPRINT",EDGE,{"derivedFrom":subQ0}),-1.0]])]});}
            var Q21;
            Q21=makeQuery(id+"F0.imprint","IMPRINT",FACE,{"disambiguationData":[TD([[makeQuery(id+"F0.imprint","IMPRINT",EDGE,{"derivedFrom":sQuery(id+"F0.wireOp",EDGE,"E4")}),1.0]])]});
            var Q22;
            Q22=makeQuery(id+"F0.imprint","IMPRINT",FACE,{"disambiguationData":[TD([[makeQuery(id+"F0.imprint","IMPRINT",EDGE,{"derivedFrom":sQuery(id+"F0.wireOp",EDGE,"E135")}),-1.0]])]});
            var Q23;
            {var subQ0=sQuery(id+"F0.wireOp",EDGE,"E187");Q23=makeQuery(id+"F0.imprint","IMPRINT",FACE,{"disambiguationData":[TD([[makeQuery(id+"F0.imprint","IMPRINT",EDGE,{"derivedFrom":subQ0}),-1.0]])]});}
            var Q24;
            {var subQ0=sQuery(id+"F0.wireOp",EDGE,"E189");Q24=makeQuery(id+"F0.imprint","IMPRINT",FACE,{"disambiguationData":[TD([[makeQuery(id+"F0.imprint","IMPRINT",EDGE,{"derivedFrom":subQ0}),1.0]])]});}
            var Q25;
            {var subQ0=sQuery(id+"F0.wireOp",EDGE,"E132");Q25=makeQuery(id+"F0.imprint","IMPRINT",FACE,{"disambiguationData":[TD([[makeQuery(id+"F0.imprint","IMPRINT",EDGE,{"derivedFrom":subQ0}),-1.0]])]});}
            var Q26;
            {var subQ0=sQuery(id+"F0.wireOp",EDGE,"E182");Q26=makeQuery(id+"F0.imprint","IMPRINT",FACE,{"disambiguationData":[TD([[makeQuery(id+"F0.imprint","IMPRINT",EDGE,{"derivedFrom":subQ0}),-1.0]])]});}
            var Q27;
            {var subQ2=sQuery(id+"F0.wireOp",EDGE,"E185");Q27=makeQuery(id+"F0.imprint","IMPRINT",FACE,{"disambiguationData":[TD([[makeQuery(id+"F0.imprint","IMPRINT",EDGE,{"derivedFrom":subQ2}),1.0]])]});}
            var Q28;
            Q28=makeQuery(id+"F0.imprint","IMPRINT",FACE,{"disambiguationData":[TD([[makeQuery(id+"F0.imprint","IMPRINT",EDGE,{"derivedFrom":sQuery(id+"F0.wireOp",EDGE,"E26")}),1.0]])]});
            var Q29;
            Q29=makeQuery(id+"F0.imprint","IMPRINT",FACE,{"disambiguationData":[TD([[makeQuery(id+"F0.imprint","IMPRINT",EDGE,{"derivedFrom":sQuery(id+"F0.wireOp",EDGE,"E118")}),-1.0]])]});
            var Q30;
            Q30=makeQuery(id+"F0.imprint","IMPRINT",FACE,{"disambiguationData":[TD([[makeQuery(id+"F0.imprint","IMPRINT",EDGE,{"derivedFrom":sQuery(id+"F0.wireOp",EDGE,"E28")}),-1.0]])]});
            var Q31;
            Q31=makeQuery(id+"F0.imprint","IMPRINT",FACE,{"disambiguationData":[TD([[makeQuery(id+"F0.imprint","IMPRINT",EDGE,{"derivedFrom":sQuery(id+"F0.wireOp",EDGE,"E55")}),1.0]])]});
            var Q32;
            {var subQ0=sQuery(id+"F0.wireOp",EDGE,"E104");Q32=makeQuery(id+"F0.imprint","IMPRINT",FACE,{"disambiguationData":[TD([[makeQuery(id+"F0.imprint","IMPRINT",EDGE,{"derivedFrom":subQ0}),-1.0]])]});}
            var Q33;
            Q33=makeQuery(id+"F0.imprint","IMPRINT",FACE,{"disambiguationData":[TD([[makeQuery(id+"F0.imprint","IMPRINT",EDGE,{"derivedFrom":sQuery(id+"F0.wireOp",EDGE,"E54")}),1.0]])]});
            var Q34;
            {var subQ0=sQuery(id+"F0.wireOp",EDGE,"E110");Q34=makeQuery(id+"F0.imprint","IMPRINT",FACE,{"disambiguationData":[TD([[makeQuery(id+"F0.imprint","IMPRINT",EDGE,{"derivedFrom":subQ0}),-1.0]])]});}
            var Q35;
            {var subQ0=sQuery(id+"F0.wireOp",EDGE,"E100");Q35=makeQuery(id+"F0.imprint","IMPRINT",FACE,{"disambiguationData":[TD([[makeQuery(id+"F0.imprint","IMPRINT",EDGE,{"derivedFrom":subQ0}),1.0]])]});}
            var Q36;
            {var subQ0=sQuery(id+"F0.wireOp",EDGE,"E86");Q36=makeQuery(id+"F0.imprint","IMPRINT",FACE,{"disambiguationData":[TD([[makeQuery(id+"F0.imprint","IMPRINT",EDGE,{"derivedFrom":subQ0}),-1.0]])]});}
            var Q37;
            {var subQ0=sQuery(id+"F0.wireOp",EDGE,"E87");Q37=makeQuery(id+"F0.imprint","IMPRINT",FACE,{"disambiguationData":[TD([[makeQuery(id+"F0.imprint","IMPRINT",EDGE,{"derivedFrom":subQ0}),-1.0]])]});}
            var Q38;
            {var subQ2=sQuery(id+"F0.wireOp",EDGE,"E167");Q38=makeQuery(id+"F0.imprint","IMPRINT",FACE,{"disambiguationData":[TD([[makeQuery(id+"F0.imprint","IMPRINT",EDGE,{"derivedFrom":subQ2}),1.0]])]});}
            var Q39;
            {var subQ0=sQuery(id+"F0.wireOp",EDGE,"E114");Q39=makeQuery(id+"F0.imprint","IMPRINT",FACE,{"disambiguationData":[TD([[makeQuery(id+"F0.imprint","IMPRINT",EDGE,{"derivedFrom":subQ0}),1.0]])]});}
            var Q40;
            {var subQ0=sQuery(id+"F0.wireOp",EDGE,"E97");Q40=makeQuery(id+"F0.imprint","IMPRINT",FACE,{"disambiguationData":[TD([[makeQuery(id+"F0.imprint","IMPRINT",EDGE,{"derivedFrom":subQ0}),1.0]])]});}
            var Q41;
            Q41=makeQuery(id+"F0.imprint","IMPRINT",FACE,{"disambiguationData":[TD([[makeQuery(id+"F0.imprint","IMPRINT",EDGE,{"derivedFrom":sQuery(id+"F0.wireOp",EDGE,"E57")}),1.0]])]});
            var Q42;
            Q42=makeQuery(id+"F0.imprint","IMPRINT",FACE,{"disambiguationData":[TD([[makeQuery(id+"F0.imprint","IMPRINT",EDGE,{"derivedFrom":sQuery(id+"F0.wireOp",EDGE,"E52")}),-1.0]])]});
            var Q43;
            Q43=makeQuery(id+"F0.imprint","IMPRINT",FACE,{"disambiguationData":[TD([[makeQuery(id+"F0.imprint","IMPRINT",EDGE,{"derivedFrom":sQuery(id+"F0.wireOp",EDGE,"E96")}),-1.0]])]});
            var Q44;
            Q44=makeQuery(id+"F0.imprint","IMPRINT",FACE,{"disambiguationData":[TD([[makeQuery(id+"F0.imprint","IMPRINT",EDGE,{"derivedFrom":sQuery(id+"F0.wireOp",EDGE,"E113")}),-1.0]])]});
            var Q45;
            {var subQ0=sQuery(id+"F0.wireOp",EDGE,"E92");Q45=makeQuery(id+"F0.imprint","IMPRINT",FACE,{"disambiguationData":[TD([[makeQuery(id+"F0.imprint","IMPRINT",EDGE,{"derivedFrom":subQ0}),-1.0]])]});}
            var Q46;
            Q46=makeQuery(id+"F0.imprint","IMPRINT",FACE,{"disambiguationData":[TD([[makeQuery(id+"F0.imprint","IMPRINT",EDGE,{"derivedFrom":sQuery(id+"F0.wireOp",EDGE,"E2")}),1.0]])]});
            var Q47;
            {var subQ0=sQuery(id+"F0.wireOp",EDGE,"E60");Q47=makeQuery(id+"F0.imprint","IMPRINT",FACE,{"disambiguationData":[TD([[makeQuery(id+"F0.imprint","IMPRINT",EDGE,{"derivedFrom":subQ0}),-1.0]])]});}
            extrude(context, id + "F2", {"entities" : qUnion([Q0, Q1, Q2, Q3, Q4, Q5, Q6, Q7, Q8, Q9, Q10, Q11, Q12, Q13, Q14, Q15, Q16, Q17, Q18, Q19, Q20, Q21, Q22, Q23, Q24, Q25, Q26, Q27, Q28, Q29, Q30, Q31, Q32, Q33, Q34, Q35, Q36, Q37, Q38, Q39, Q40, Q41, Q42, Q43, Q44, Q45, Q46, Q47]), "depth" : 25 * mm, "offsetDistance" : 25 * mm});
        }
        {
            var Q0;
            Q0=makeQuery(id+"F0.imprint","IMPRINT",FACE,{"disambiguationData":[TD([[makeQuery(id+"F0.imprint","IMPRINT",EDGE,{"derivedFrom":sQuery(id+"F0.wireOp",EDGE,"E18")}),1.0]])]});
            var Q1;
            Q1=makeQuery(id+"F0.imprint","IMPRINT",FACE,{"disambiguationData":[TD([[makeQuery(id+"F0.imprint","IMPRINT",EDGE,{"derivedFrom":sQuery(id+"F0.wireOp",EDGE,"E79")}),1.0]])]});
            var Q2;
            {var subQ5=sQuery(id+"F0.wireOp",EDGE,"E158");Q2=makeQuery(id+"F0.imprint","IMPRINT",FACE,{"disambiguationData":[TD([[makeQuery(id+"F0.imprint","IMPRINT",EDGE,{"derivedFrom":subQ5}),1.0]])]});}
            var Q3;
            Q3=makeQuery(id+"F0.imprint","IMPRINT",FACE,{"disambiguationData":[TD([[makeQuery(id+"F0.imprint","IMPRINT",EDGE,{"derivedFrom":sQuery(id+"F0.wireOp",EDGE,"E36")}),1.0]])]});
            var Q4;
            Q4=makeQuery(id+"F0.imprint","IMPRINT",FACE,{"disambiguationData":[TD([[makeQuery(id+"F0.imprint","IMPRINT",EDGE,{"derivedFrom":sQuery(id+"F0.wireOp",EDGE,"E34")}),1.0]])]});
            var Q5;
            Q5=makeQuery(id+"F0.imprint","IMPRINT",FACE,{"disambiguationData":[TD([[makeQuery(id+"F0.imprint","IMPRINT",EDGE,{"derivedFrom":sQuery(id+"F0.wireOp",EDGE,"E129")}),-1.0]])]});
            var Q6;
            {var subQ0=sQuery(id+"F0.wireOp",EDGE,"E119");Q6=makeQuery(id+"F0.imprint","IMPRINT",FACE,{"disambiguationData":[TD([[makeQuery(id+"F0.imprint","IMPRINT",EDGE,{"derivedFrom":subQ0}),1.0]])]});}
            var Q7;
            {var subQ0=sQuery(id+"F0.wireOp",EDGE,"E146");Q7=makeQuery(id+"F0.imprint","IMPRINT",FACE,{"disambiguationData":[TD([[makeQuery(id+"F0.imprint","IMPRINT",EDGE,{"derivedFrom":subQ0}),-1.0]])]});}
            var Q8;
            Q8=makeQuery(id+"F0.imprint","IMPRINT",FACE,{"disambiguationData":[TD([[makeQuery(id+"F0.imprint","IMPRINT",EDGE,{"derivedFrom":sQuery(id+"F0.wireOp",EDGE,"E145")}),1.0]])]});
            var Q9;
            Q9=makeQuery(id+"F0.imprint","IMPRINT",FACE,{"disambiguationData":[TD([[makeQuery(id+"F0.imprint","IMPRINT",EDGE,{"derivedFrom":sQuery(id+"F0.wireOp",EDGE,"E46")}),-1.0]])]});
            var Q10;
            Q10=makeQuery(id+"F0.imprint","IMPRINT",FACE,{"disambiguationData":[TD([[makeQuery(id+"F0.imprint","IMPRINT",EDGE,{"derivedFrom":sQuery(id+"F0.wireOp",EDGE,"E56")}),1.0]])]});
            var Q11;
            Q11=makeQuery(id+"F0.imprint","IMPRINT",FACE,{"disambiguationData":[TD([[makeQuery(id+"F0.imprint","IMPRINT",EDGE,{"derivedFrom":sQuery(id+"F0.wireOp",EDGE,"E103")}),-1.0]])]});
            var Q12;
            Q12=makeQuery(id+"F0.imprint","IMPRINT",FACE,{"disambiguationData":[TD([[makeQuery(id+"F0.imprint","IMPRINT",EDGE,{"derivedFrom":sQuery(id+"F0.wireOp",EDGE,"E49")}),-1.0]])]});
            var Q13;
            {var subQ0=sQuery(id+"F0.wireOp",EDGE,"E110");Q13=makeQuery(id+"F0.imprint","IMPRINT",FACE,{"disambiguationData":[TD([[makeQuery(id+"F0.imprint","IMPRINT",EDGE,{"derivedFrom":subQ0}),1.0]])]});}
            var Q14;
            {var subQ0=sQuery(id+"F0.wireOp",EDGE,"E114");Q14=makeQuery(id+"F0.imprint","IMPRINT",FACE,{"disambiguationData":[TD([[makeQuery(id+"F0.imprint","IMPRINT",EDGE,{"derivedFrom":subQ0}),-1.0]])]});}
            var Q15;
            {var subQ3=sQuery(id+"F0.wireOp",EDGE,"E202");Q15=makeQuery(id+"F0.imprint","IMPRINT",FACE,{"disambiguationData":[TD([[makeQuery(id+"F0.imprint","IMPRINT",EDGE,{"derivedFrom":subQ3}),-1.0]])]});}
            var Q16;
            {var subQ0=sQuery(id+"F0.wireOp",EDGE,"E59");Q16=makeQuery(id+"F0.imprint","IMPRINT",FACE,{"disambiguationData":[TD([[makeQuery(id+"F0.imprint","IMPRINT",EDGE,{"derivedFrom":subQ0}),1.0]])]});}
            extrude(context, id + "F3", {"entities" : qUnion([Q0, Q1, Q2, Q3, Q4, Q5, Q6, Q7, Q8, Q9, Q10, Q11, Q12, Q13, Q14, Q15, Q16]), "depth" : 25 * mm, "offsetDistance" : 25 * mm});
        }
        {
            var Q0;
            {var subQ2=sQuery(id+"F0.wireOp",EDGE,"E163");Q0=makeQuery(id+"F0.imprint","IMPRINT",FACE,{"disambiguationData":[TD([[makeQuery(id+"F0.imprint","IMPRINT",EDGE,{"derivedFrom":subQ2}),-1.0]])]});}
            var Q1;
            {var subQ0=sQuery(id+"F0.wireOp",EDGE,"E160");Q1=makeQuery(id+"F0.imprint","IMPRINT",FACE,{"disambiguationData":[TD([[makeQuery(id+"F0.imprint","IMPRINT",EDGE,{"derivedFrom":subQ0}),1.0]])]});}
            var Q2;
            Q2=makeQuery(id+"F0.imprint","IMPRINT",FACE,{"disambiguationData":[TD([[makeQuery(id+"F0.imprint","IMPRINT",EDGE,{"derivedFrom":sQuery(id+"F0.wireOp",EDGE,"E35")}),-1.0]])]});
            extrude(context, id + "F4", {"entities" : qUnion([Q0, Q1, Q2]), "depth" : 25 * mm, "offsetDistance" : 25 * mm});
        }
        {
            var Q0;
            Q0=makeQuery(id+"F1.opExtrude","SWEPT_BODY",BODY,{"disambiguationData":[OSD([sQuery(id+"F0.wireOp",EDGE,"E3"),sQuery(id+"F0.wireOp",EDGE,"E53"),sQuery(id+"F0.wireOp",EDGE,"E54")])]});
            transform(context, id + "F5", {"entities" : qUnion([Q0]), "transformType" : TransformType.TRANSLATION_3D, "dx" : 0 * mm, "dy" : 0 * mm, "dz" : 0 * mm, "makeCopy" : true});
        }
        {
            var Q0;
            Q0=makeQuery(id+"F1.opExtrude","SWEPT_FACE",FACE,{"disambiguationData":[OSD([sQuery(id+"F0.wireOp",EDGE,"E53")])]});
            var sketch = newSketch(context, id + "F6", { "sketchPlane" : qUnion([Q0])});
            skText(sketch, "E205", { "text": "1", "fontName": "OpenSans-Bold.ttf"});
            const initialGuessF6  = {"E205": [0.00121, 0.00172, 1, 0, 0.02117]};
            skSetInitialGuess(sketch, initialGuessF6);
            skSolve(sketch);
        }
        {
            var Q0;
            Q0 = qSketchRegion(id + "F6", true);
            extrude(context, id + "F7", {"entities" : qUnion([Q0]), "operationType" : NewBodyOperationType.REMOVE, "oppositeDirection" : true, "depth" : 2 * mm, "offsetDistance" : 25 * mm});
        }
        {
            var Q0;
            Q0=makeQuery(id+"F1.opExtrude","SWEPT_FACE",FACE,{"disambiguationData":[OSD([sQuery(id+"F0.wireOp",EDGE,"E39")])]});
            var sketch = newSketch(context, id + "F8", { "sketchPlane" : qUnion([Q0])});
            skText(sketch, "E206", { "text": "2", "fontName": "OpenSans-Bold.ttf"});
            const initialGuessF8  = {"E206": [0.18333, 0.0017, 1, 0, 0.02096]};
            skSetInitialGuess(sketch, initialGuessF8);
            skSolve(sketch);
        }
        {
            var Q0;
            Q0=makeQuery(id+"F8.imprint","IMPRINT",FACE,{"disambiguationData":[TD([[makeQuery(id+"F8.imprint","IMPRINT",EDGE,{"derivedFrom":sQuery(id+"F8.wireOp",EDGE,"E206.sketch_text.stroke-0")}),-1.0]])]});
            extrude(context, id + "F9", {"entities" : qUnion([Q0]), "operationType" : NewBodyOperationType.REMOVE, "oppositeDirection" : true, "depth" : 2 * mm, "offsetDistance" : 25 * mm});
        }
        {
            var Q0;
            Q0=makeQuery(id+"F1.opExtrude","SWEPT_FACE",FACE,{"disambiguationData":[OSD([sQuery(id+"F0.wireOp",EDGE,"E41")])]});
            var sketch = newSketch(context, id + "F10", { "sketchPlane" : qUnion([Q0])});
            skText(sketch, "E207", { "text": "3", "fontName": "OpenSans-Bold.ttf"});
            const initialGuessF10  = {"E207": [0.17496, 0.00268, 1, 0, 0.01956]};
            skSetInitialGuess(sketch, initialGuessF10);
            skSolve(sketch);
        }
        {
            var Q0;
            Q0=makeQuery(id+"F10.imprint","IMPRINT",FACE,{"disambiguationData":[TD([[makeQuery(id+"F10.imprint","IMPRINT",EDGE,{"derivedFrom":sQuery(id+"F10.wireOp",EDGE,"E207.sketch_text.stroke-0")}),-1.0]])]});
            extrude(context, id + "F11", {"entities" : qUnion([Q0]), "operationType" : NewBodyOperationType.REMOVE, "oppositeDirection" : true, "depth" : 2 * mm, "offsetDistance" : 25 * mm});
        }
        {
            var Q0;
            Q0=makeQuery(id+"F1.opExtrude","SWEPT_FACE",FACE,{"disambiguationData":[OSD([sQuery(id+"F0.wireOp",EDGE,"E46")])]});
            var sketch = newSketch(context, id + "F12", { "sketchPlane" : qUnion([Q0])});
            skText(sketch, "E208", { "text": "4", "fontName": "OpenSans-Bold.ttf"});
            const initialGuessF12  = {"E208": [0.2097, 0.00235, 1, 0, 0.02013]};
            skSetInitialGuess(sketch, initialGuessF12);
            skSolve(sketch);
        }
        {
            var Q0;
            Q0=makeQuery(id+"F12.imprint","IMPRINT",FACE,{"disambiguationData":[TD([[makeQuery(id+"F12.imprint","IMPRINT",EDGE,{"derivedFrom":sQuery(id+"F12.wireOp",EDGE,"E208.sketch_text.stroke-0")}),-1.0]])]});
            extrude(context, id + "F13", {"entities" : qUnion([Q0]), "operationType" : NewBodyOperationType.REMOVE, "oppositeDirection" : true, "depth" : 2 * mm, "offsetDistance" : 25 * mm});
        }
        {
            var Q0;
            Q0=makeQuery(id+"F1.opExtrude","SWEPT_FACE",FACE,{"disambiguationData":[OSD([sQuery(id+"F0.wireOp",EDGE,"E82")])]});
            var sketch = newSketch(context, id + "F14", { "sketchPlane" : qUnion([Q0])});
            skText(sketch, "E209", { "text": "5", "fontName": "OpenSans-Bold.ttf"});
            const initialGuessF14  = {"E209": [0.11513, 0.00267, 1, 0, 0.0192]};
            skSetInitialGuess(sketch, initialGuessF14);
            skSolve(sketch);
        }
        {
            var Q0;
            Q0=makeQuery(id+"F14.imprint","IMPRINT",FACE,{"disambiguationData":[TD([[makeQuery(id+"F14.imprint","IMPRINT",EDGE,{"derivedFrom":sQuery(id+"F14.wireOp",EDGE,"E209.sketch_text.stroke-0")}),-1.0]])]});
            extrude(context, id + "F15", {"entities" : qUnion([Q0]), "operationType" : NewBodyOperationType.REMOVE, "oppositeDirection" : true, "depth" : 2 * mm, "offsetDistance" : 25 * mm});
        }
        {
            var Q0;
            Q0=makeQuery(id+"F1.opExtrude","SWEPT_FACE",FACE,{"disambiguationData":[OSD([sQuery(id+"F0.wireOp",EDGE,"E153")])]});
            var sketch = newSketch(context, id + "F16", { "sketchPlane" : qUnion([Q0])});
            skText(sketch, "E210", { "text": "6", "fontName": "OpenSans-Bold.ttf"});
            const initialGuessF16  = {"E210": [0.34531, 0.003, 1, 0, 0.01905]};
            skSetInitialGuess(sketch, initialGuessF16);
            skSolve(sketch);
        }
        {
            var Q0;
            Q0=makeQuery(id+"F16.imprint","IMPRINT",FACE,{"disambiguationData":[TD([[makeQuery(id+"F16.imprint","IMPRINT",EDGE,{"derivedFrom":sQuery(id+"F16.wireOp",EDGE,"E210.sketch_text.stroke-0")}),-1.0]])]});
            extrude(context, id + "F17", {"entities" : qUnion([Q0]), "operationType" : NewBodyOperationType.REMOVE, "oppositeDirection" : true, "depth" : 2 * mm, "offsetDistance" : 25 * mm});
        }
        {
            var Q0;
            Q0=makeQuery(id+"F1.opExtrude","SWEPT_FACE",FACE,{"disambiguationData":[OSD([sQuery(id+"F0.wireOp",EDGE,"E166")])]});
            var sketch = newSketch(context, id + "F18", { "sketchPlane" : qUnion([Q0])});
            skText(sketch, "E211", { "text": "7", "fontName": "OpenSans-Bold.ttf"});
            const initialGuessF18  = {"E211": [-0.14042, 0.00212, 1, 0, 0.01955]};
            skSetInitialGuess(sketch, initialGuessF18);
            skSolve(sketch);
        }
        {
            var Q0;
            Q0=makeQuery(id+"F18.imprint","IMPRINT",FACE,{"disambiguationData":[TD([[makeQuery(id+"F18.imprint","IMPRINT",EDGE,{"derivedFrom":sQuery(id+"F18.wireOp",EDGE,"E211.sketch_text.stroke-0")}),-1.0]])]});
            extrude(context, id + "F19", {"entities" : qUnion([Q0]), "operationType" : NewBodyOperationType.REMOVE, "oppositeDirection" : true, "depth" : 2 * mm, "offsetDistance" : 25 * mm});
        }
        {
            var Q0;
            Q0=makeQuery(id+"F1.opExtrude","SWEPT_FACE",FACE,{"disambiguationData":[OSD([sQuery(id+"F0.wireOp",EDGE,"E14")])]});
            var sketch = newSketch(context, id + "F20", { "sketchPlane" : qUnion([Q0])});
            skText(sketch, "E212", { "text": "8", "fontName": "OpenSans-Bold.ttf"});
            const initialGuessF20  = {"E212": [0.37286, 0.00255, 1, 0, 0.0194]};
            skSetInitialGuess(sketch, initialGuessF20);
            skSolve(sketch);
        }
        {
            var Q0;
            Q0=makeQuery(id+"F20.imprint","IMPRINT",FACE,{"disambiguationData":[TD([[makeQuery(id+"F20.imprint","IMPRINT",EDGE,{"derivedFrom":sQuery(id+"F20.wireOp",EDGE,"E212.sketch_text.stroke-0")}),-1.0]])]});
            extrude(context, id + "F21", {"entities" : qUnion([Q0]), "operationType" : NewBodyOperationType.REMOVE, "oppositeDirection" : true, "depth" : 2 * mm, "offsetDistance" : 25 * mm});
        }
        {
            var Q0;
            Q0=makeQuery(id+"F1.opExtrude","SWEPT_FACE",FACE,{"disambiguationData":[OSD([sQuery(id+"F0.wireOp",EDGE,"E79")])]});
            var sketch = newSketch(context, id + "F22", { "sketchPlane" : qUnion([Q0])});
            skText(sketch, "E213", { "text": "9", "fontName": "OpenSans-Bold.ttf"});
            const initialGuessF22  = {"E213": [0.14422, 0.00248, 1, 0, 0.01863]};
            skSetInitialGuess(sketch, initialGuessF22);
            skSolve(sketch);
        }
        {
            var Q0;
            Q0=makeQuery(id+"F22.imprint","IMPRINT",FACE,{"disambiguationData":[TD([[makeQuery(id+"F22.imprint","IMPRINT",EDGE,{"derivedFrom":sQuery(id+"F22.wireOp",EDGE,"E213.sketch_text.stroke-0")}),-1.0]])]});
            extrude(context, id + "F23", {"entities" : qUnion([Q0]), "operationType" : NewBodyOperationType.REMOVE, "oppositeDirection" : true, "depth" : 2 * mm, "offsetDistance" : 25 * mm});
        }
        {
            var Q0;
            Q0=makeQuery(id+"F1.opExtrude","SWEPT_FACE",FACE,{"disambiguationData":[OSD([sQuery(id+"F0.wireOp",EDGE,"E159")])]});
            var sketch = newSketch(context, id + "F24", { "sketchPlane" : qUnion([Q0])});
            skText(sketch, "E214", { "text": "10", "fontName": "OpenSans-Bold.ttf"});
            const initialGuessF24  = {"E214": [0.42897, 0.00562, 1, 0, 0.01227]};
            skSetInitialGuess(sketch, initialGuessF24);
            skSolve(sketch);
        }
        {
            var Q0;
            Q0=makeQuery(id+"F24.imprint","IMPRINT",FACE,{"disambiguationData":[TD([[makeQuery(id+"F24.imprint","IMPRINT",EDGE,{"derivedFrom":sQuery(id+"F24.wireOp",EDGE,"E214.sketch_text.stroke-0")}),-1.0]])]});
            var Q1;
            Q1=makeQuery(id+"F24.imprint","IMPRINT",FACE,{"disambiguationData":[TD([[makeQuery(id+"F24.imprint","IMPRINT",EDGE,{"derivedFrom":sQuery(id+"F24.wireOp",EDGE,"E214.sketch_text.stroke-10")}),-1.0]])]});
            extrude(context, id + "F25", {"entities" : qUnion([Q0, Q1]), "operationType" : NewBodyOperationType.REMOVE, "oppositeDirection" : true, "depth" : 2 * mm, "offsetDistance" : 25 * mm});
        }
        {
            var Q0;
            Q0=makeQuery(id+"F1.opExtrude","SWEPT_FACE",FACE,{"disambiguationData":[OSD([sQuery(id+"F0.wireOp",EDGE,"E67")])]});
            var sketch = newSketch(context, id + "F26", { "sketchPlane" : qUnion([Q0])});
            skText(sketch, "E215", { "text": "11", "fontName": "AllertaStencil-Regular.ttf"});
            const initialGuessF26  = {"E215": [-0.49277, 0.00927, 1, 0, 0.01037]};
            skSetInitialGuess(sketch, initialGuessF26);
            skSolve(sketch);
        }
        {
            var Q0;
            Q0=makeQuery(id+"F26.imprint","IMPRINT",FACE,{"disambiguationData":[TD([[makeQuery(id+"F26.imprint","IMPRINT",EDGE,{"derivedFrom":sQuery(id+"F26.wireOp",EDGE,"E215.sketch_text.stroke-0")}),-1.0]])]});
            var Q1;
            Q1=makeQuery(id+"F26.imprint","IMPRINT",FACE,{"disambiguationData":[TD([[makeQuery(id+"F26.imprint","IMPRINT",EDGE,{"derivedFrom":sQuery(id+"F26.wireOp",EDGE,"E215.sketch_text.stroke-7")}),-1.0]])]});
            extrude(context, id + "F27", {"entities" : qUnion([Q0, Q1]), "operationType" : NewBodyOperationType.REMOVE, "oppositeDirection" : true, "depth" : 2 * mm, "offsetDistance" : 25 * mm});
        }
        {
            var Q0;
            Q0=makeQuery(id+"F1.opExtrude","SWEPT_FACE",FACE,{"disambiguationData":[OSD([sQuery(id+"F0.wireOp",EDGE,"E69")])]});
            var sketch = newSketch(context, id + "F28", { "sketchPlane" : qUnion([Q0])});
            skText(sketch, "E216", { "text": "12", "fontName": "AllertaStencil-Regular.ttf"});
            const initialGuessF28  = {"E216": [-0.51886, 0.00654, 1, 0, 0.0135]};
            skSetInitialGuess(sketch, initialGuessF28);
            skSolve(sketch);
        }
        {
            var Q0;
            Q0=makeQuery(id+"F28.imprint","IMPRINT",FACE,{"disambiguationData":[TD([[makeQuery(id+"F28.imprint","IMPRINT",EDGE,{"derivedFrom":sQuery(id+"F28.wireOp",EDGE,"E216.sketch_text.stroke-0")}),-1.0]])]});
            var Q1;
            Q1=makeQuery(id+"F28.imprint","IMPRINT",FACE,{"disambiguationData":[TD([[makeQuery(id+"F28.imprint","IMPRINT",EDGE,{"derivedFrom":sQuery(id+"F28.wireOp",EDGE,"E216.sketch_text.stroke-7")}),-1.0]])]});
            extrude(context, id + "F29", {"entities" : qUnion([Q0, Q1]), "operationType" : NewBodyOperationType.REMOVE, "oppositeDirection" : true, "depth" : 2 * mm, "offsetDistance" : 25 * mm});
        }
        {
            var Q0;
            Q0=makeQuery(id+"F1.opExtrude","SWEPT_FACE",FACE,{"disambiguationData":[OSD([sQuery(id+"F0.wireOp",EDGE,"E75")])]});
            var sketch = newSketch(context, id + "F30", { "sketchPlane" : qUnion([Q0])});
            skText(sketch, "E217", { "text": "13", "fontName": "AllertaStencil-Regular.ttf"});
            const initialGuessF30  = {"E217": [0.086, 0.01316, 1, 0, 0.00916]};
            skSetInitialGuess(sketch, initialGuessF30);
            skSolve(sketch);
        }
        {
            var Q0;
            Q0=makeQuery(id+"F30.imprint","IMPRINT",FACE,{"disambiguationData":[TD([[makeQuery(id+"F30.imprint","IMPRINT",EDGE,{"derivedFrom":sQuery(id+"F30.wireOp",EDGE,"E217.sketch_text.stroke-0")}),-1.0]])]});
            var Q1;
            Q1=makeQuery(id+"F30.imprint","IMPRINT",FACE,{"disambiguationData":[TD([[makeQuery(id+"F30.imprint","IMPRINT",EDGE,{"derivedFrom":sQuery(id+"F30.wireOp",EDGE,"E217.sketch_text.stroke-7")}),-1.0]])]});
            extrude(context, id + "F31", {"entities" : qUnion([Q0, Q1]), "operationType" : NewBodyOperationType.REMOVE, "oppositeDirection" : true, "depth" : 2 * mm, "offsetDistance" : 25 * mm});
        }
        {
            var Q0;
            Q0=makeQuery(id+"F1.opExtrude","SWEPT_FACE",FACE,{"disambiguationData":[OSD([sQuery(id+"F0.wireOp",EDGE,"E36")])]});
            var sketch = newSketch(context, id + "F32", { "sketchPlane" : qUnion([Q0])});
            skText(sketch, "E218", { "text": "14", "fontName": "AllertaStencil-Regular.ttf"});
            const initialGuessF32  = {"E218": [-0.32481, 0.0056, 1, 0, 0.01585]};
            skSetInitialGuess(sketch, initialGuessF32);
            skSolve(sketch);
        }
        {
            var Q0;
            Q0=makeQuery(id+"F32.imprint","IMPRINT",FACE,{"disambiguationData":[TD([[makeQuery(id+"F32.imprint","IMPRINT",EDGE,{"derivedFrom":sQuery(id+"F32.wireOp",EDGE,"E218.sketch_text.stroke-0")}),-1.0]])]});
            var Q1;
            Q1=makeQuery(id+"F32.imprint","IMPRINT",FACE,{"disambiguationData":[TD([[makeQuery(id+"F32.imprint","IMPRINT",EDGE,{"derivedFrom":sQuery(id+"F32.wireOp",EDGE,"E218.sketch_text.stroke-7")}),-1.0]])]});
            var Q2;
            Q2=makeQuery(id+"F32.imprint","IMPRINT",FACE,{"disambiguationData":[TD([[makeQuery(id+"F32.imprint","IMPRINT",EDGE,{"derivedFrom":sQuery(id+"F32.wireOp",EDGE,"E218.sketch_text.stroke-15")}),-1.0]])]});
            extrude(context, id + "F33", {"entities" : qUnion([Q0, Q1, Q2]), "operationType" : NewBodyOperationType.REMOVE, "oppositeDirection" : true, "depth" : 2 * mm, "offsetDistance" : 25 * mm});
        }
        {
            var Q0;
            Q0=makeQuery(id+"F1.opExtrude","SWEPT_FACE",FACE,{"disambiguationData":[OSD([sQuery(id+"F0.wireOp",EDGE,"E31")])]});
            var sketch = newSketch(context, id + "F34", { "sketchPlane" : qUnion([Q0])});
            skText(sketch, "E219", { "text": "15", "fontName": "AllertaStencil-Regular.ttf"});
            const initialGuessF34  = {"E219": [-0.27595, 0.00694, 1, 0, 0.01372]};
            skSetInitialGuess(sketch, initialGuessF34);
            skSolve(sketch);
        }
        {
            var Q0;
            Q0=makeQuery(id+"F34.imprint","IMPRINT",FACE,{"disambiguationData":[TD([[makeQuery(id+"F34.imprint","IMPRINT",EDGE,{"derivedFrom":sQuery(id+"F34.wireOp",EDGE,"E219.sketch_text.stroke-0")}),-1.0]])]});
            var Q1;
            Q1=makeQuery(id+"F34.imprint","IMPRINT",FACE,{"disambiguationData":[TD([[makeQuery(id+"F34.imprint","IMPRINT",EDGE,{"derivedFrom":sQuery(id+"F34.wireOp",EDGE,"E219.sketch_text.stroke-33")}),-1.0]])]});
            var Q2;
            Q2=makeQuery(id+"F34.imprint","IMPRINT",FACE,{"disambiguationData":[TD([[makeQuery(id+"F34.imprint","IMPRINT",EDGE,{"derivedFrom":sQuery(id+"F34.wireOp",EDGE,"E219.sketch_text.stroke-7")}),-1.0]])]});
            extrude(context, id + "F35", {"entities" : qUnion([Q0, Q1, Q2]), "operationType" : NewBodyOperationType.REMOVE, "oppositeDirection" : true, "depth" : 2 * mm, "offsetDistance" : 25 * mm});
        }
        {
            var Q0;
            Q0=makeQuery(id+"F1.opExtrude","SWEPT_FACE",FACE,{"disambiguationData":[OSD([sQuery(id+"F0.wireOp",EDGE,"E32")])]});
            var sketch = newSketch(context, id + "F36", { "sketchPlane" : qUnion([Q0])});
            skText(sketch, "E220", { "text": "16", "fontName": "AllertaStencil-Regular.ttf"});
            const initialGuessF36  = {"E220": [-0.29057, 0.006, 1, 0, 0.01466]};
            skSetInitialGuess(sketch, initialGuessF36);
            skSolve(sketch);
        }
        {
            var Q0;
            Q0=makeQuery(id+"F36.imprint","IMPRINT",FACE,{"disambiguationData":[TD([[makeQuery(id+"F36.imprint","IMPRINT",EDGE,{"derivedFrom":sQuery(id+"F36.wireOp",EDGE,"E220.sketch_text.stroke-0")}),-1.0]])]});
            var Q1;
            Q1=makeQuery(id+"F36.imprint","IMPRINT",FACE,{"disambiguationData":[TD([[makeQuery(id+"F36.imprint","IMPRINT",EDGE,{"derivedFrom":sQuery(id+"F36.wireOp",EDGE,"E220.sketch_text.stroke-7")}),-1.0]])]});
            var Q2;
            Q2=makeQuery(id+"F36.imprint","IMPRINT",FACE,{"disambiguationData":[TD([[makeQuery(id+"F36.imprint","IMPRINT",EDGE,{"derivedFrom":sQuery(id+"F36.wireOp",EDGE,"E220.sketch_text.stroke-38")}),-1.0]])]});
            extrude(context, id + "F37", {"entities" : qUnion([Q0, Q1, Q2]), "operationType" : NewBodyOperationType.REMOVE, "oppositeDirection" : true, "depth" : 2 * mm, "offsetDistance" : 25 * mm});
        }
        {
            var Q0;
            Q0=makeQuery(id+"F1.opExtrude","SWEPT_FACE",FACE,{"disambiguationData":[OSD([sQuery(id+"F0.wireOp",EDGE,"E119")])]});
            var sketch = newSketch(context, id + "F38", { "sketchPlane" : qUnion([Q0])});
            skText(sketch, "E221", { "text": "17", "fontName": "AllertaStencil-Regular.ttf"});
            const initialGuessF38  = {"E221": [-0.1833, 0.00772, 1, 0, 0.01225]};
            skSetInitialGuess(sketch, initialGuessF38);
            skSolve(sketch);
        }
        {
            var Q0;
            Q0=makeQuery(id+"F38.imprint","IMPRINT",FACE,{"disambiguationData":[TD([[makeQuery(id+"F38.imprint","IMPRINT",EDGE,{"derivedFrom":sQuery(id+"F38.wireOp",EDGE,"E221.sketch_text.stroke-0")}),-1.0]])]});
            var Q1;
            Q1=makeQuery(id+"F38.imprint","IMPRINT",FACE,{"disambiguationData":[TD([[makeQuery(id+"F38.imprint","IMPRINT",EDGE,{"derivedFrom":sQuery(id+"F38.wireOp",EDGE,"E221.sketch_text.stroke-7")}),-1.0]])]});
            extrude(context, id + "F39", {"entities" : qUnion([Q0, Q1]), "operationType" : NewBodyOperationType.REMOVE, "oppositeDirection" : true, "depth" : 2 * mm, "offsetDistance" : 25 * mm});
        }
        {
            var Q0;
            Q0=makeQuery(id+"F1.opExtrude","SWEPT_FACE",FACE,{"disambiguationData":[OSD([sQuery(id+"F0.wireOp",EDGE,"E72")])]});
            var sketch = newSketch(context, id + "F40", { "sketchPlane" : qUnion([Q0])});
            skText(sketch, "E222", { "text": "18", "fontName": "AllertaStencil-Regular.ttf"});
            const initialGuessF40  = {"E222": [0.48186, 0.00795, 1, 0, 0.01248]};
            skSetInitialGuess(sketch, initialGuessF40);
            skSolve(sketch);
        }
        {
            var Q0;
            Q0=makeQuery(id+"F40.imprint","IMPRINT",FACE,{"disambiguationData":[TD([[makeQuery(id+"F40.imprint","IMPRINT",EDGE,{"derivedFrom":sQuery(id+"F40.wireOp",EDGE,"E222.sketch_text.stroke-0")}),-1.0]])]});
            var Q1;
            Q1=makeQuery(id+"F40.imprint","IMPRINT",FACE,{"disambiguationData":[TD([[makeQuery(id+"F40.imprint","IMPRINT",EDGE,{"derivedFrom":sQuery(id+"F40.wireOp",EDGE,"E222.sketch_text.stroke-7")}),-1.0]])]});
            var Q2;
            Q2=makeQuery(id+"F40.imprint","IMPRINT",FACE,{"disambiguationData":[TD([[makeQuery(id+"F40.imprint","IMPRINT",EDGE,{"derivedFrom":sQuery(id+"F40.wireOp",EDGE,"E222.sketch_text.stroke-31")}),-1.0]])]});
            extrude(context, id + "F41", {"entities" : qUnion([Q0, Q1, Q2]), "operationType" : NewBodyOperationType.REMOVE, "oppositeDirection" : true, "depth" : 2 * mm, "offsetDistance" : 25 * mm});
        }
        {
            var Q0;
            Q0=makeQuery(id+"F1.opExtrude","SWEPT_FACE",FACE,{"disambiguationData":[OSD([sQuery(id+"F0.wireOp",EDGE,"E38")])]});
            var sketch = newSketch(context, id + "F42", { "sketchPlane" : qUnion([Q0])});
            skText(sketch, "E223", { "text": "19", "fontName": "AllertaStencil-Regular.ttf"});
            const initialGuessF42  = {"E223": [-0.07757, 0.01116, 1, 0, 0.00856]};
            skSetInitialGuess(sketch, initialGuessF42);
            skSolve(sketch);
        }
        {
            var Q0;
            Q0=makeQuery(id+"F42.imprint","IMPRINT",FACE,{"disambiguationData":[TD([[makeQuery(id+"F42.imprint","IMPRINT",EDGE,{"derivedFrom":sQuery(id+"F42.wireOp",EDGE,"E223.sketch_text.stroke-0")}),-1.0]])]});
            var Q1;
            Q1=makeQuery(id+"F42.imprint","IMPRINT",FACE,{"disambiguationData":[TD([[makeQuery(id+"F42.imprint","IMPRINT",EDGE,{"derivedFrom":sQuery(id+"F42.wireOp",EDGE,"E223.sketch_text.stroke-7")}),-1.0]])]});
            var Q2;
            Q2=makeQuery(id+"F42.imprint","IMPRINT",FACE,{"disambiguationData":[TD([[makeQuery(id+"F42.imprint","IMPRINT",EDGE,{"derivedFrom":sQuery(id+"F42.wireOp",EDGE,"E223.sketch_text.stroke-21")}),-1.0]])]});
            extrude(context, id + "F43", {"entities" : qUnion([Q0, Q1, Q2]), "operationType" : NewBodyOperationType.REMOVE, "oppositeDirection" : true, "depth" : 2 * mm, "offsetDistance" : 25 * mm});
        }
        {
            var Q0;
            Q0=makeQuery(id+"F1.opExtrude","SWEPT_FACE",FACE,{"disambiguationData":[OSD([sQuery(id+"F0.wireOp",EDGE,"E81")])]});
            var sketch = newSketch(context, id + "F44", { "sketchPlane" : qUnion([Q0])});
            skText(sketch, "E224", { "text": "20", "fontName": "AllertaStencil-Regular.ttf"});
            const initialGuessF44  = {"E224": [0.2757, 0.00644, 1, 0, 0.0154]};
            skSetInitialGuess(sketch, initialGuessF44);
            skSolve(sketch);
        }
        {
            var Q0;
            Q0=makeQuery(id+"F44.imprint","IMPRINT",FACE,{"disambiguationData":[TD([[makeQuery(id+"F44.imprint","IMPRINT",EDGE,{"derivedFrom":sQuery(id+"F44.wireOp",EDGE,"E224.sketch_text.stroke-0")}),-1.0]])]});
            var Q1;
            Q1=makeQuery(id+"F44.imprint","IMPRINT",FACE,{"disambiguationData":[TD([[makeQuery(id+"F44.imprint","IMPRINT",EDGE,{"derivedFrom":sQuery(id+"F44.wireOp",EDGE,"E224.sketch_text.stroke-33")}),-1.0]])]});
            var Q2;
            Q2=makeQuery(id+"F44.imprint","IMPRINT",FACE,{"disambiguationData":[TD([[makeQuery(id+"F44.imprint","IMPRINT",EDGE,{"derivedFrom":sQuery(id+"F44.wireOp",EDGE,"E224.sketch_text.stroke-49")}),-1.0]])]});
            extrude(context, id + "F45", {"entities" : qUnion([Q0, Q1, Q2]), "operationType" : NewBodyOperationType.REMOVE, "oppositeDirection" : true, "depth" : 2 * mm, "offsetDistance" : 25 * mm});
        }
        {
            var Q0;
            Q0=makeQuery(id+"F1.opExtrude","SWEPT_FACE",FACE,{"disambiguationData":[OSD([sQuery(id+"F0.wireOp",EDGE,"E57")])]});
            var sketch = newSketch(context, id + "F46", { "sketchPlane" : qUnion([Q0])});
            skText(sketch, "E225", { "text": "21", "fontName": "AllertaStencil-Regular.ttf"});
            const initialGuessF46  = {"E225": [-0.06574, 0.00947, 1, 0, 0.00984]};
            skSetInitialGuess(sketch, initialGuessF46);
            skSolve(sketch);
        }
        {
            var Q0;
            Q0=makeQuery(id+"F46.imprint","IMPRINT",FACE,{"disambiguationData":[TD([[makeQuery(id+"F46.imprint","IMPRINT",EDGE,{"derivedFrom":sQuery(id+"F46.wireOp",EDGE,"E225.sketch_text.stroke-0")}),-1.0]])]});
            var Q1;
            Q1=makeQuery(id+"F46.imprint","IMPRINT",FACE,{"disambiguationData":[TD([[makeQuery(id+"F46.imprint","IMPRINT",EDGE,{"derivedFrom":sQuery(id+"F46.wireOp",EDGE,"E225.sketch_text.stroke-33")}),-1.0]])]});
            extrude(context, id + "F47", {"entities" : qUnion([Q0, Q1]), "operationType" : NewBodyOperationType.REMOVE, "oppositeDirection" : true, "depth" : 2 * mm, "offsetDistance" : 25 * mm});
        }
        {
            var Q0;
            Q0=makeQuery(id+"F1.opExtrude","SWEPT_FACE",FACE,{"disambiguationData":[OSD([sQuery(id+"F0.wireOp",EDGE,"E135")])]});
            var sketch = newSketch(context, id + "F48", { "sketchPlane" : qUnion([Q0])});
            skText(sketch, "E226", { "text": "22", "fontName": "AllertaStencil-Regular.ttf"});
            const initialGuessF48  = {"E226": [-0.19845, 0.00662, 1, 0, 0.01349]};
            skSetInitialGuess(sketch, initialGuessF48);
            skSolve(sketch);
        }
        {
            var Q0;
            Q0=makeQuery(id+"F48.imprint","IMPRINT",FACE,{"disambiguationData":[TD([[makeQuery(id+"F48.imprint","IMPRINT",EDGE,{"derivedFrom":sQuery(id+"F48.wireOp",EDGE,"E226.sketch_text.stroke-0")}),-1.0]])]});
            var Q1;
            Q1=makeQuery(id+"F48.imprint","IMPRINT",FACE,{"disambiguationData":[TD([[makeQuery(id+"F48.imprint","IMPRINT",EDGE,{"derivedFrom":sQuery(id+"F48.wireOp",EDGE,"E226.sketch_text.stroke-33")}),-1.0]])]});
            extrude(context, id + "F49", {"entities" : qUnion([Q0, Q1]), "operationType" : NewBodyOperationType.REMOVE, "oppositeDirection" : true, "depth" : 2 * mm, "offsetDistance" : 25 * mm});
        }
        {
            var Q0;
            Q0=makeQuery(id+"F1.opExtrude","SWEPT_FACE",FACE,{"disambiguationData":[OSD([sQuery(id+"F0.wireOp",EDGE,"E56")])]});
            var sketch = newSketch(context, id + "F50", { "sketchPlane" : qUnion([Q0])});
            skText(sketch, "E227", { "text": "23", "fontName": "AllertaStencil-Regular.ttf"});
            const initialGuessF50  = {"E227": [-0.01833, 0.00667, 1, 0, 0.012]};
            skSetInitialGuess(sketch, initialGuessF50);
            skSolve(sketch);
        }
        {
            var Q0;
            Q0=makeQuery(id+"F50.imprint","IMPRINT",FACE,{"disambiguationData":[TD([[makeQuery(id+"F50.imprint","IMPRINT",EDGE,{"derivedFrom":sQuery(id+"F50.wireOp",EDGE,"E227.sketch_text.stroke-0")}),-1.0]])]});
            var Q1;
            Q1=makeQuery(id+"F50.imprint","IMPRINT",FACE,{"disambiguationData":[TD([[makeQuery(id+"F50.imprint","IMPRINT",EDGE,{"derivedFrom":sQuery(id+"F50.wireOp",EDGE,"E227.sketch_text.stroke-33")}),-1.0]])]});
            extrude(context, id + "F51", {"entities" : qUnion([Q0, Q1]), "operationType" : NewBodyOperationType.REMOVE, "oppositeDirection" : true, "depth" : 2 * mm, "offsetDistance" : 25 * mm});
        }
        {
            var Q0;
            Q0=makeQuery(id+"F1.opExtrude","SWEPT_FACE",FACE,{"disambiguationData":[OSD([sQuery(id+"F0.wireOp",EDGE,"E92")])]});
            var sketch = newSketch(context, id + "F52", { "sketchPlane" : qUnion([Q0])});
            skText(sketch, "E228", { "text": "24", "fontName": "AllertaStencil-Regular.ttf"});
            const initialGuessF52  = {"E228": [-0.01428, 0.01431, 1, 0, 0.0066]};
            skSetInitialGuess(sketch, initialGuessF52);
            skSolve(sketch);
        }
        {
            var Q0;
            Q0=makeQuery(id+"F52.imprint","IMPRINT",FACE,{"disambiguationData":[TD([[makeQuery(id+"F52.imprint","IMPRINT",EDGE,{"derivedFrom":sQuery(id+"F52.wireOp",EDGE,"E228.sketch_text.stroke-0")}),-1.0]])]});
            var Q1;
            Q1=makeQuery(id+"F52.imprint","IMPRINT",FACE,{"disambiguationData":[TD([[makeQuery(id+"F52.imprint","IMPRINT",EDGE,{"derivedFrom":sQuery(id+"F52.wireOp",EDGE,"E228.sketch_text.stroke-41")}),-1.0]])]});
            var Q2;
            Q2=makeQuery(id+"F52.imprint","IMPRINT",FACE,{"disambiguationData":[TD([[makeQuery(id+"F52.imprint","IMPRINT",EDGE,{"derivedFrom":sQuery(id+"F52.wireOp",EDGE,"E228.sketch_text.stroke-33")}),-1.0]])]});
            extrude(context, id + "F53", {"entities" : qUnion([Q0, Q1, Q2]), "operationType" : NewBodyOperationType.REMOVE, "oppositeDirection" : true, "depth" : 2 * mm, "offsetDistance" : 25 * mm});
        }
        {
            var Q0;
            Q0=makeQuery(id+"F1.opExtrude","SWEPT_FACE",FACE,{"disambiguationData":[OSD([sQuery(id+"F0.wireOp",EDGE,"E64")])]});
            var sketch = newSketch(context, id + "F54", { "sketchPlane" : qUnion([Q0])});
            skText(sketch, "E229", { "text": "25", "fontName": "AllertaStencil-Regular.ttf"});
            const initialGuessF54  = {"E229": [0.06818, 0.00692, 1, 0, 0.01121]};
            skSetInitialGuess(sketch, initialGuessF54);
            skSolve(sketch);
        }
        {
            var Q0;
            Q0=makeQuery(id+"F54.imprint","IMPRINT",FACE,{"disambiguationData":[TD([[makeQuery(id+"F54.imprint","IMPRINT",EDGE,{"derivedFrom":sQuery(id+"F54.wireOp",EDGE,"E229.sketch_text.stroke-0")}),-1.0]])]});
            var Q1;
            Q1=makeQuery(id+"F54.imprint","IMPRINT",FACE,{"disambiguationData":[TD([[makeQuery(id+"F54.imprint","IMPRINT",EDGE,{"derivedFrom":sQuery(id+"F54.wireOp",EDGE,"E229.sketch_text.stroke-59")}),-1.0]])]});
            var Q2;
            Q2=makeQuery(id+"F54.imprint","IMPRINT",FACE,{"disambiguationData":[TD([[makeQuery(id+"F54.imprint","IMPRINT",EDGE,{"derivedFrom":sQuery(id+"F54.wireOp",EDGE,"E229.sketch_text.stroke-33")}),-1.0]])]});
            extrude(context, id + "F55", {"entities" : qUnion([Q0, Q1, Q2]), "operationType" : NewBodyOperationType.REMOVE, "oppositeDirection" : true, "depth" : 2 * mm, "offsetDistance" : 25 * mm});
        }
        {
            var Q0;
            {var subQ0=sQuery(id+"F0.wireOp",EDGE,"E65");Q0=makeQuery(id+"F1.opExtrude","SWEPT_FACE",FACE,{"disambiguationData":[OSD([subQ0]),TDD([makeQuery(id+"F0.imprint","IMPRINT",EDGE,{"disambiguationData":[TD([[makeQuery(id+"F0.imprint","INTERSECT",VERTEX,{"derivedFrom":[subQ0,sQuery(id+"F0.wireOp",EDGE,"E167"),sQuery(id+"F0.wireOp",EDGE,"E168")]}),1.0]])],"derivedFrom":subQ0})])]});}
            var sketch = newSketch(context, id + "F56", { "sketchPlane" : qUnion([Q0])});
            skText(sketch, "E230", { "text": "26", "fontName": "AllertaStencil-Regular.ttf"});
            const initialGuessF56  = {"E230": [0.0708, 0.01588, 1, 0, 0.00557]};
            skSetInitialGuess(sketch, initialGuessF56);
            skSolve(sketch);
        }
        {
            var Q0;
            Q0=makeQuery(id+"F56.imprint","IMPRINT",FACE,{"disambiguationData":[TD([[makeQuery(id+"F56.imprint","IMPRINT",EDGE,{"derivedFrom":sQuery(id+"F56.wireOp",EDGE,"E230.sketch_text.stroke-0")}),-1.0]])]});
            var Q1;
            Q1=makeQuery(id+"F56.imprint","IMPRINT",FACE,{"disambiguationData":[TD([[makeQuery(id+"F56.imprint","IMPRINT",EDGE,{"derivedFrom":sQuery(id+"F56.wireOp",EDGE,"E230.sketch_text.stroke-33")}),-1.0]])]});
            var Q2;
            Q2=makeQuery(id+"F56.imprint","IMPRINT",FACE,{"disambiguationData":[TD([[makeQuery(id+"F56.imprint","IMPRINT",EDGE,{"derivedFrom":sQuery(id+"F56.wireOp",EDGE,"E230.sketch_text.stroke-64")}),-1.0]])]});
            extrude(context, id + "F57", {"entities" : qUnion([Q0, Q1, Q2]), "operationType" : NewBodyOperationType.REMOVE, "oppositeDirection" : true, "depth" : 2 * mm, "offsetDistance" : 25 * mm});
        }
        {
            var Q0;
            {var subQ0=sQuery(id+"F0.wireOp",EDGE,"E65");Q0=makeQuery(id+"F1.opExtrude","SWEPT_FACE",FACE,{"disambiguationData":[OSD([subQ0]),TDD([makeQuery(id+"F0.imprint","IMPRINT",EDGE,{"disambiguationData":[TD([[makeQuery(id+"F0.imprint","INTERSECT",VERTEX,{"derivedFrom":[subQ0,sQuery(id+"F0.wireOp",EDGE,"E90")]}),1.0]])],"derivedFrom":subQ0})])]});}
            var sketch = newSketch(context, id + "F58", { "sketchPlane" : qUnion([Q0])});
            skText(sketch, "E231", { "text": "27", "fontName": "AllertaStencil-Regular.ttf"});
            const initialGuessF58  = {"E231": [0.05311, 0.01127, 1, 0, 0.00804]};
            skSetInitialGuess(sketch, initialGuessF58);
            skSolve(sketch);
        }
        {
            var Q0;
            Q0=makeQuery(id+"F58.imprint","IMPRINT",FACE,{"disambiguationData":[TD([[makeQuery(id+"F58.imprint","IMPRINT",EDGE,{"derivedFrom":sQuery(id+"F58.wireOp",EDGE,"E231.sketch_text.stroke-0")}),-1.0]])]});
            var Q1;
            Q1=makeQuery(id+"F58.imprint","IMPRINT",FACE,{"disambiguationData":[TD([[makeQuery(id+"F58.imprint","IMPRINT",EDGE,{"derivedFrom":sQuery(id+"F58.wireOp",EDGE,"E231.sketch_text.stroke-33")}),-1.0]])]});
            extrude(context, id + "F59", {"entities" : qUnion([Q0, Q1]), "operationType" : NewBodyOperationType.REMOVE, "oppositeDirection" : true, "depth" : 2 * mm, "offsetDistance" : 25 * mm});
        }
        {
            var Q0;
            Q0=makeQuery(id+"F1.opExtrude","SWEPT_FACE",FACE,{"disambiguationData":[OSD([sQuery(id+"F0.wireOp",EDGE,"E87")])]});
            var sketch = newSketch(context, id + "F60", { "sketchPlane" : qUnion([Q0])});
            skText(sketch, "E232", { "text": "28", "fontName": "AllertaStencil-Regular.ttf"});
            const initialGuessF60  = {"E232": [-0.03918, 0.0122, 1, 0, 0.0079]};
            skSetInitialGuess(sketch, initialGuessF60);
            skSolve(sketch);
        }
        {
            var Q0;
            Q0=makeQuery(id+"F60.imprint","IMPRINT",FACE,{"disambiguationData":[TD([[makeQuery(id+"F60.imprint","IMPRINT",EDGE,{"derivedFrom":sQuery(id+"F60.wireOp",EDGE,"E232.sketch_text.stroke-0")}),-1.0]])]});
            var Q1;
            Q1=makeQuery(id+"F60.imprint","IMPRINT",FACE,{"disambiguationData":[TD([[makeQuery(id+"F60.imprint","IMPRINT",EDGE,{"derivedFrom":sQuery(id+"F60.wireOp",EDGE,"E232.sketch_text.stroke-33")}),-1.0]])]});
            var Q2;
            Q2=makeQuery(id+"F60.imprint","IMPRINT",FACE,{"disambiguationData":[TD([[makeQuery(id+"F60.imprint","IMPRINT",EDGE,{"derivedFrom":sQuery(id+"F60.wireOp",EDGE,"E232.sketch_text.stroke-57")}),-1.0]])]});
            extrude(context, id + "F61", {"entities" : qUnion([Q0, Q1, Q2]), "operationType" : NewBodyOperationType.REMOVE, "oppositeDirection" : true, "depth" : 2 * mm, "offsetDistance" : 25 * mm});
        }
        {
            var Q0;
            Q0=makeQuery(id+"F1.opExtrude","SWEPT_FACE",FACE,{"disambiguationData":[OSD([sQuery(id+"F0.wireOp",EDGE,"E162")])]});
            var sketch = newSketch(context, id + "F62", { "sketchPlane" : qUnion([Q0])});
            skText(sketch, "E233", { "text": "29", "fontName": "AllertaStencil-Regular.ttf"});
            const initialGuessF62  = {"E233": [-0.12154, 0.0057, 1, 0, 0.01303]};
            skSetInitialGuess(sketch, initialGuessF62);
            skSolve(sketch);
        }
        {
            var Q0;
            Q0=makeQuery(id+"F62.imprint","IMPRINT",FACE,{"disambiguationData":[TD([[makeQuery(id+"F62.imprint","IMPRINT",EDGE,{"derivedFrom":sQuery(id+"F62.wireOp",EDGE,"E233.sketch_text.stroke-33")}),-1.0]])]});
            var Q1;
            Q1=makeQuery(id+"F62.imprint","IMPRINT",FACE,{"disambiguationData":[TD([[makeQuery(id+"F62.imprint","IMPRINT",EDGE,{"derivedFrom":sQuery(id+"F62.wireOp",EDGE,"E233.sketch_text.stroke-47")}),-1.0]])]});
            var Q2;
            Q2=makeQuery(id+"F62.imprint","IMPRINT",FACE,{"disambiguationData":[TD([[makeQuery(id+"F62.imprint","IMPRINT",EDGE,{"derivedFrom":sQuery(id+"F62.wireOp",EDGE,"E233.sketch_text.stroke-0")}),-1.0]])]});
            extrude(context, id + "F63", {"entities" : qUnion([Q0, Q1, Q2]), "operationType" : NewBodyOperationType.REMOVE, "oppositeDirection" : true, "depth" : 2 * mm, "offsetDistance" : 25 * mm});
        }
        {
            var Q0;
            Q0=makeQuery(id+"F1.opExtrude","SWEPT_FACE",FACE,{"disambiguationData":[OSD([sQuery(id+"F0.wireOp",EDGE,"E102")])]});
            var sketch = newSketch(context, id + "F64", { "sketchPlane" : qUnion([Q0])});
            skText(sketch, "E234", { "text": "30", "fontName": "AllertaStencil-Regular.ttf"});
            skPoint(sketch, "E234.firstSnap0", {"position": v(80.86, 25) * mm});
            const initialGuessF64  = {"E234": [0.08086, 0.0055, 1, 0, 0.01297]};
            skSetInitialGuess(sketch, initialGuessF64);
            skSolve(sketch);
        }
        {
            var Q0;
            Q0=makeQuery(id+"F64.imprint","IMPRINT",FACE,{"disambiguationData":[TD([[makeQuery(id+"F64.imprint","IMPRINT",EDGE,{"derivedFrom":sQuery(id+"F64.wireOp",EDGE,"E234.sketch_text.stroke-0")}),-1.0]])]});
            var Q1;
            Q1=makeQuery(id+"F64.imprint","IMPRINT",FACE,{"disambiguationData":[TD([[makeQuery(id+"F64.imprint","IMPRINT",EDGE,{"derivedFrom":sQuery(id+"F64.wireOp",EDGE,"E234.sketch_text.stroke-46")}),-1.0]])]});
            var Q2;
            Q2=makeQuery(id+"F64.imprint","IMPRINT",FACE,{"disambiguationData":[TD([[makeQuery(id+"F64.imprint","IMPRINT",EDGE,{"derivedFrom":sQuery(id+"F64.wireOp",EDGE,"E234.sketch_text.stroke-62")}),-1.0]])]});
            extrude(context, id + "F65", {"entities" : qUnion([Q0, Q1, Q2]), "operationType" : NewBodyOperationType.REMOVE, "oppositeDirection" : true, "depth" : 2 * mm, "offsetDistance" : 25 * mm});
        }
        {
            var Q0;
            Q0=makeQuery(id+"F1.opExtrude","SWEPT_FACE",FACE,{"disambiguationData":[OSD([sQuery(id+"F0.wireOp",EDGE,"E96")])]});
            var sketch = newSketch(context, id + "F66", { "sketchPlane" : qUnion([Q0])});
            skText(sketch, "E235", { "text": "31", "fontName": "AllertaStencil-Regular.ttf"});
            const initialGuessF66  = {"E235": [-0.05237, 0.0161, 1, 0, 0.00417]};
            skSetInitialGuess(sketch, initialGuessF66);
            skSolve(sketch);
        }
        {
            var Q0;
            Q0=makeQuery(id+"F1.opExtrude","SWEPT_FACE",FACE,{"disambiguationData":[OSD([sQuery(id+"F0.wireOp",EDGE,"E193")])]});
            var sketch = newSketch(context, id + "F67", { "sketchPlane" : qUnion([Q0])});
            skText(sketch, "E236", { "text": "32", "fontName": "AllertaStencil-Regular.ttf"});
            const initialGuessF67  = {"E236": [0.01564, 0.00886, 1, 0, 0.01305]};
            skSetInitialGuess(sketch, initialGuessF67);
            skSolve(sketch);
        }
        {
            var Q0;
            Q0=makeQuery(id+"F67.imprint","IMPRINT",FACE,{"disambiguationData":[TD([[makeQuery(id+"F67.imprint","IMPRINT",EDGE,{"derivedFrom":sQuery(id+"F67.wireOp",EDGE,"E236.sketch_text.stroke-0")}),-1.0]])]});
            var Q1;
            Q1=makeQuery(id+"F67.imprint","IMPRINT",FACE,{"disambiguationData":[TD([[makeQuery(id+"F67.imprint","IMPRINT",EDGE,{"derivedFrom":sQuery(id+"F67.wireOp",EDGE,"E236.sketch_text.stroke-46")}),-1.0]])]});
            extrude(context, id + "F68", {"entities" : qUnion([Q0, Q1]), "operationType" : NewBodyOperationType.REMOVE, "oppositeDirection" : true, "depth" : 2 * mm, "offsetDistance" : 25 * mm});
        }
        {
            var Q0;
            Q0=makeQuery(id+"F1.opExtrude","SWEPT_FACE",FACE,{"disambiguationData":[OSD([sQuery(id+"F0.wireOp",EDGE,"E97")])]});
            var sketch = newSketch(context, id + "F69", { "sketchPlane" : qUnion([Q0])});
            skText(sketch, "E237", { "text": "33", "fontName": "AllertaStencil-Regular.ttf"});
            const initialGuessF69  = {"E237": [-0.0187, 0.0137, 1, 0, 0.00601]};
            skSetInitialGuess(sketch, initialGuessF69);
            skSolve(sketch);
        }
        {
            var Q0;
            Q0=makeQuery(id+"F69.imprint","IMPRINT",FACE,{"disambiguationData":[TD([[makeQuery(id+"F69.imprint","IMPRINT",EDGE,{"derivedFrom":sQuery(id+"F69.wireOp",EDGE,"E237.sketch_text.stroke-0")}),-1.0]])]});
            var Q1;
            Q1=makeQuery(id+"F69.imprint","IMPRINT",FACE,{"disambiguationData":[TD([[makeQuery(id+"F69.imprint","IMPRINT",EDGE,{"derivedFrom":sQuery(id+"F69.wireOp",EDGE,"E237.sketch_text.stroke-46")}),-1.0]])]});
            extrude(context, id + "F70", {"entities" : qUnion([Q0, Q1]), "operationType" : NewBodyOperationType.REMOVE, "oppositeDirection" : true, "depth" : 2 * mm, "offsetDistance" : 25 * mm});
        }
        {
            var Q0;
            Q0=makeQuery(id+"F66.imprint","IMPRINT",FACE,{"disambiguationData":[TD([[makeQuery(id+"F66.imprint","IMPRINT",EDGE,{"derivedFrom":sQuery(id+"F66.wireOp",EDGE,"E235.sketch_text.stroke-0")}),-1.0]])]});
            var Q1;
            Q1=makeQuery(id+"F66.imprint","IMPRINT",FACE,{"disambiguationData":[TD([[makeQuery(id+"F66.imprint","IMPRINT",EDGE,{"derivedFrom":sQuery(id+"F66.wireOp",EDGE,"E235.sketch_text.stroke-46")}),-1.0]])]});
            extrude(context, id + "F71", {"entities" : qUnion([Q0, Q1]), "operationType" : NewBodyOperationType.REMOVE, "oppositeDirection" : true, "depth" : 2 * mm, "offsetDistance" : 25 * mm});
        }
        {
            var Q0;
            Q0=makeQuery(id+"F1.opExtrude","SWEPT_FACE",FACE,{"disambiguationData":[OSD([sQuery(id+"F0.wireOp",EDGE,"E203")])]});
            var sketch = newSketch(context, id + "F72", { "sketchPlane" : qUnion([Q0])});
            skText(sketch, "E238", { "text": "34", "fontName": "AllertaStencil-Regular.ttf"});
            const initialGuessF72  = {"E238": [0.00018, 0.01447, 1, 0, 0.00638]};
            skSetInitialGuess(sketch, initialGuessF72);
            skSolve(sketch);
        }
        {
            var Q0;
            Q0=makeQuery(id+"F72.imprint","IMPRINT",FACE,{"disambiguationData":[TD([[makeQuery(id+"F72.imprint","IMPRINT",EDGE,{"derivedFrom":sQuery(id+"F72.wireOp",EDGE,"E238.sketch_text.stroke-0")}),-1.0]])]});
            var Q1;
            Q1=makeQuery(id+"F72.imprint","IMPRINT",FACE,{"disambiguationData":[TD([[makeQuery(id+"F72.imprint","IMPRINT",EDGE,{"derivedFrom":sQuery(id+"F72.wireOp",EDGE,"E238.sketch_text.stroke-54")}),-1.0]])]});
            var Q2;
            Q2=makeQuery(id+"F72.imprint","IMPRINT",FACE,{"disambiguationData":[TD([[makeQuery(id+"F72.imprint","IMPRINT",EDGE,{"derivedFrom":sQuery(id+"F72.wireOp",EDGE,"E238.sketch_text.stroke-46")}),-1.0]])]});
            extrude(context, id + "F73", {"entities" : qUnion([Q0, Q1, Q2]), "operationType" : NewBodyOperationType.REMOVE, "oppositeDirection" : true, "depth" : 2 * mm, "offsetDistance" : 25 * mm});
        }
        {
            var Q0;
            Q0=makeQuery(id+"F1.opExtrude","SWEPT_FACE",FACE,{"disambiguationData":[OSD([sQuery(id+"F0.wireOp",EDGE,"E115")])]});
            var sketch = newSketch(context, id + "F74", { "sketchPlane" : qUnion([Q0])});
            skText(sketch, "E239", { "text": "35", "fontName": "AllertaStencil-Regular.ttf"});
            const initialGuessF74  = {"E239": [-0.10277, 0.0157, 1, 0, 0.00498]};
            skSetInitialGuess(sketch, initialGuessF74);
            skSolve(sketch);
        }
        {
            var Q0;
            Q0=makeQuery(id+"F74.imprint","IMPRINT",FACE,{"disambiguationData":[TD([[makeQuery(id+"F74.imprint","IMPRINT",EDGE,{"derivedFrom":sQuery(id+"F74.wireOp",EDGE,"E239.sketch_text.stroke-0")}),-1.0]])]});
            var Q1;
            Q1=makeQuery(id+"F74.imprint","IMPRINT",FACE,{"disambiguationData":[TD([[makeQuery(id+"F74.imprint","IMPRINT",EDGE,{"derivedFrom":sQuery(id+"F74.wireOp",EDGE,"E239.sketch_text.stroke-72")}),-1.0]])]});
            var Q2;
            Q2=makeQuery(id+"F74.imprint","IMPRINT",FACE,{"disambiguationData":[TD([[makeQuery(id+"F74.imprint","IMPRINT",EDGE,{"derivedFrom":sQuery(id+"F74.wireOp",EDGE,"E239.sketch_text.stroke-46")}),-1.0]])]});
            extrude(context, id + "F75", {"entities" : qUnion([Q0, Q1, Q2]), "operationType" : NewBodyOperationType.REMOVE, "oppositeDirection" : true, "depth" : 2 * mm, "offsetDistance" : 25 * mm});
        }
        {
            var Q0;
            Q0=makeQuery(id+"F1.opExtrude","SWEPT_FACE",FACE,{"disambiguationData":[OSD([sQuery(id+"F0.wireOp",EDGE,"E111")])]});
            var sketch = newSketch(context, id + "F76", { "sketchPlane" : qUnion([Q0])});
            skText(sketch, "E240", { "text": "36", "fontName": "AllertaStencil-Regular.ttf"});
            const initialGuessF76  = {"E240": [-0.1312, 0.00862, 1, 0, 0.01222]};
            skSetInitialGuess(sketch, initialGuessF76);
            skSolve(sketch);
        }
        {
            var Q0;
            Q0=makeQuery(id+"F76.imprint","IMPRINT",FACE,{"disambiguationData":[TD([[makeQuery(id+"F76.imprint","IMPRINT",EDGE,{"derivedFrom":sQuery(id+"F76.wireOp",EDGE,"E240.sketch_text.stroke-0")}),-1.0]])]});
            var Q1;
            Q1=makeQuery(id+"F76.imprint","IMPRINT",FACE,{"disambiguationData":[TD([[makeQuery(id+"F76.imprint","IMPRINT",EDGE,{"derivedFrom":sQuery(id+"F76.wireOp",EDGE,"E240.sketch_text.stroke-46")}),-1.0]])]});
            var Q2;
            Q2=makeQuery(id+"F76.imprint","IMPRINT",FACE,{"disambiguationData":[TD([[makeQuery(id+"F76.imprint","IMPRINT",EDGE,{"derivedFrom":sQuery(id+"F76.wireOp",EDGE,"E240.sketch_text.stroke-77")}),-1.0]])]});
            extrude(context, id + "F77", {"entities" : qUnion([Q0, Q1, Q2]), "operationType" : NewBodyOperationType.REMOVE, "oppositeDirection" : true, "depth" : 2 * mm, "offsetDistance" : 25 * mm});
        }
        {
            var Q0;
            Q0=makeQuery(id+"F1.opExtrude","SWEPT_FACE",FACE,{"disambiguationData":[OSD([sQuery(id+"F0.wireOp",EDGE,"E113")])]});
            var sketch = newSketch(context, id + "F78", { "sketchPlane" : qUnion([Q0])});
            skText(sketch, "E241", { "text": "37", "fontName": "AllertaStencil-Regular.ttf"});
            const initialGuessF78  = {"E241": [-0.05459, 0.00983, 1, 0, 0.00963]};
            skSetInitialGuess(sketch, initialGuessF78);
            skSolve(sketch);
        }
        {
            var Q0;
            Q0=makeQuery(id+"F78.imprint","IMPRINT",FACE,{"disambiguationData":[TD([[makeQuery(id+"F78.imprint","IMPRINT",EDGE,{"derivedFrom":sQuery(id+"F78.wireOp",EDGE,"E241.sketch_text.stroke-0")}),-1.0]])]});
            var Q1;
            Q1=makeQuery(id+"F78.imprint","IMPRINT",FACE,{"disambiguationData":[TD([[makeQuery(id+"F78.imprint","IMPRINT",EDGE,{"derivedFrom":sQuery(id+"F78.wireOp",EDGE,"E241.sketch_text.stroke-46")}),-1.0]])]});
            extrude(context, id + "F79", {"entities" : qUnion([Q0, Q1]), "operationType" : NewBodyOperationType.REMOVE, "oppositeDirection" : true, "depth" : 2 * mm, "offsetDistance" : 25 * mm});
        }
        {
            var Q0;
            Q0=makeQuery(id+"F1.opExtrude","SWEPT_FACE",FACE,{"disambiguationData":[OSD([sQuery(id+"F0.wireOp",EDGE,"E121")])]});
            var sketch = newSketch(context, id + "F80", { "sketchPlane" : qUnion([Q0])});
            skText(sketch, "E242", { "text": "38", "fontName": "AllertaStencil-Regular.ttf"});
            const initialGuessF80  = {"E242": [0.16538, 0.00895, 1, 0, 0.01087]};
            skSetInitialGuess(sketch, initialGuessF80);
            skSolve(sketch);
        }
        {
            var Q0;
            Q0=makeQuery(id+"F80.imprint","IMPRINT",FACE,{"disambiguationData":[TD([[makeQuery(id+"F80.imprint","IMPRINT",EDGE,{"derivedFrom":sQuery(id+"F80.wireOp",EDGE,"E242.sketch_text.stroke-0")}),-1.0]])]});
            var Q1;
            Q1=makeQuery(id+"F80.imprint","IMPRINT",FACE,{"disambiguationData":[TD([[makeQuery(id+"F80.imprint","IMPRINT",EDGE,{"derivedFrom":sQuery(id+"F80.wireOp",EDGE,"E242.sketch_text.stroke-46")}),-1.0]])]});
            var Q2;
            Q2=makeQuery(id+"F80.imprint","IMPRINT",FACE,{"disambiguationData":[TD([[makeQuery(id+"F80.imprint","IMPRINT",EDGE,{"derivedFrom":sQuery(id+"F80.wireOp",EDGE,"E242.sketch_text.stroke-70")}),-1.0]])]});
            extrude(context, id + "F81", {"entities" : qUnion([Q0, Q1, Q2]), "operationType" : NewBodyOperationType.REMOVE, "oppositeDirection" : true, "depth" : 2 * mm, "offsetDistance" : 25 * mm});
        }
        {
            var Q0;
            Q0=makeQuery(id+"F1.opExtrude","SWEPT_FACE",FACE,{"disambiguationData":[OSD([sQuery(id+"F0.wireOp",EDGE,"E122")])]});
            var sketch = newSketch(context, id + "F82", { "sketchPlane" : qUnion([Q0])});
            skText(sketch, "E243", { "text": "39", "fontName": "AllertaStencil-Regular.ttf"});
            const initialGuessF82  = {"E243": [-0.26838, 0.0084, 1, 0, 0.0108]};
            skSetInitialGuess(sketch, initialGuessF82);
            skSolve(sketch);
        }
        {
            var Q0;
            Q0=makeQuery(id+"F82.imprint","IMPRINT",FACE,{"disambiguationData":[TD([[makeQuery(id+"F82.imprint","IMPRINT",EDGE,{"derivedFrom":sQuery(id+"F82.wireOp",EDGE,"E243.sketch_text.stroke-0")}),-1.0]])]});
            var Q1;
            Q1=makeQuery(id+"F82.imprint","IMPRINT",FACE,{"disambiguationData":[TD([[makeQuery(id+"F82.imprint","IMPRINT",EDGE,{"derivedFrom":sQuery(id+"F82.wireOp",EDGE,"E243.sketch_text.stroke-46")}),-1.0]])]});
            var Q2;
            Q2=makeQuery(id+"F82.imprint","IMPRINT",FACE,{"disambiguationData":[TD([[makeQuery(id+"F82.imprint","IMPRINT",EDGE,{"derivedFrom":sQuery(id+"F82.wireOp",EDGE,"E243.sketch_text.stroke-60")}),-1.0]])]});
            extrude(context, id + "F83", {"entities" : qUnion([Q0, Q1, Q2]), "operationType" : NewBodyOperationType.REMOVE, "oppositeDirection" : true, "depth" : 2 * mm, "offsetDistance" : 25 * mm});
        }
        {
            var Q0;
            Q0=makeQuery(id+"F1.opExtrude","SWEPT_FACE",FACE,{"disambiguationData":[OSD([sQuery(id+"F0.wireOp",EDGE,"E131")])]});
            var sketch = newSketch(context, id + "F84", { "sketchPlane" : qUnion([Q0])});
            skText(sketch, "E244", { "text": "40", "fontName": "AllertaStencil-Regular.ttf"});
            const initialGuessF84  = {"E244": [-0.27408, 0.0062, 1, 0, 0.01183]};
            skSetInitialGuess(sketch, initialGuessF84);
            skSolve(sketch);
        }
        {
            var Q0;
            Q0=makeQuery(id+"F84.imprint","IMPRINT",FACE,{"disambiguationData":[TD([[makeQuery(id+"F84.imprint","IMPRINT",EDGE,{"derivedFrom":sQuery(id+"F84.wireOp",EDGE,"E244.sketch_text.stroke-8")}),-1.0]])]});
            var Q1;
            Q1=makeQuery(id+"F84.imprint","IMPRINT",FACE,{"disambiguationData":[TD([[makeQuery(id+"F84.imprint","IMPRINT",EDGE,{"derivedFrom":sQuery(id+"F84.wireOp",EDGE,"E244.sketch_text.stroke-0")}),-1.0]])]});
            var Q2;
            Q2=makeQuery(id+"F84.imprint","IMPRINT",FACE,{"disambiguationData":[TD([[makeQuery(id+"F84.imprint","IMPRINT",EDGE,{"derivedFrom":sQuery(id+"F84.wireOp",EDGE,"E244.sketch_text.stroke-15")}),-1.0]])]});
            var Q3;
            Q3=makeQuery(id+"F84.imprint","IMPRINT",FACE,{"disambiguationData":[TD([[makeQuery(id+"F84.imprint","IMPRINT",EDGE,{"derivedFrom":sQuery(id+"F84.wireOp",EDGE,"E244.sketch_text.stroke-31")}),-1.0]])]});
            extrude(context, id + "F85", {"entities" : qUnion([Q0, Q1, Q2, Q3]), "operationType" : NewBodyOperationType.REMOVE, "oppositeDirection" : true, "depth" : 2 * mm, "offsetDistance" : 25 * mm});
        }
        {
            var Q0;
            Q0=makeQuery(id+"F1.opExtrude","SWEPT_FACE",FACE,{"disambiguationData":[OSD([sQuery(id+"F0.wireOp",EDGE,"E195")])]});
            var sketch = newSketch(context, id + "F86", { "sketchPlane" : qUnion([Q0])});
            skText(sketch, "E245", { "text": "41", "fontName": "AllertaStencil-Regular.ttf"});
            const initialGuessF86  = {"E245": [0.2707, 0.00701, 1, 0, 0.01243]};
            skSetInitialGuess(sketch, initialGuessF86);
            skSolve(sketch);
        }
        {
            var Q0;
            Q0=makeQuery(id+"F86.imprint","IMPRINT",FACE,{"disambiguationData":[TD([[makeQuery(id+"F86.imprint","IMPRINT",EDGE,{"derivedFrom":sQuery(id+"F86.wireOp",EDGE,"E245.sketch_text.stroke-8")}),-1.0]])]});
            var Q1;
            Q1=makeQuery(id+"F86.imprint","IMPRINT",FACE,{"disambiguationData":[TD([[makeQuery(id+"F86.imprint","IMPRINT",EDGE,{"derivedFrom":sQuery(id+"F86.wireOp",EDGE,"E245.sketch_text.stroke-0")}),-1.0]])]});
            var Q2;
            Q2=makeQuery(id+"F86.imprint","IMPRINT",FACE,{"disambiguationData":[TD([[makeQuery(id+"F86.imprint","IMPRINT",EDGE,{"derivedFrom":sQuery(id+"F86.wireOp",EDGE,"E245.sketch_text.stroke-15")}),-1.0]])]});
            extrude(context, id + "F87", {"entities" : qUnion([Q0, Q1, Q2]), "operationType" : NewBodyOperationType.REMOVE, "oppositeDirection" : true, "depth" : 2 * mm, "offsetDistance" : 25 * mm});
        }
        {
            var Q0;
            Q0=makeQuery(id+"F1.opExtrude","SWEPT_FACE",FACE,{"disambiguationData":[OSD([sQuery(id+"F0.wireOp",EDGE,"E130")])]});
            var sketch = newSketch(context, id + "F88", { "sketchPlane" : qUnion([Q0])});
            skText(sketch, "E246", { "text": "42", "fontName": "AllertaStencil-Regular.ttf"});
            const initialGuessF88  = {"E246": [0.06688, 0.0072, 1, 0, 0.01249]};
            skSetInitialGuess(sketch, initialGuessF88);
            skSolve(sketch);
        }
        {
            var Q0;
            Q0=makeQuery(id+"F88.imprint","IMPRINT",FACE,{"disambiguationData":[TD([[makeQuery(id+"F88.imprint","IMPRINT",EDGE,{"derivedFrom":sQuery(id+"F88.wireOp",EDGE,"E246.sketch_text.stroke-8")}),-1.0]])]});
            var Q1;
            Q1=makeQuery(id+"F88.imprint","IMPRINT",FACE,{"disambiguationData":[TD([[makeQuery(id+"F88.imprint","IMPRINT",EDGE,{"derivedFrom":sQuery(id+"F88.wireOp",EDGE,"E246.sketch_text.stroke-0")}),-1.0]])]});
            var Q2;
            Q2=makeQuery(id+"F88.imprint","IMPRINT",FACE,{"disambiguationData":[TD([[makeQuery(id+"F88.imprint","IMPRINT",EDGE,{"derivedFrom":sQuery(id+"F88.wireOp",EDGE,"E246.sketch_text.stroke-15")}),-1.0]])]});
            extrude(context, id + "F89", {"entities" : qUnion([Q0, Q1, Q2]), "operationType" : NewBodyOperationType.REMOVE, "oppositeDirection" : true, "depth" : 2 * mm, "offsetDistance" : 25 * mm});
        }
        {
            var Q0;
            Q0=makeQuery(id+"F1.opExtrude","SWEPT_FACE",FACE,{"disambiguationData":[OSD([sQuery(id+"F0.wireOp",EDGE,"E142")])]});
            var sketch = newSketch(context, id + "F90", { "sketchPlane" : qUnion([Q0])});
            skText(sketch, "E247", { "text": "43", "fontName": "AllertaStencil-Regular.ttf"});
            const initialGuessF90  = {"E247": [-0.09062, 0.0071, 1, 0, 0.01382]};
            skSetInitialGuess(sketch, initialGuessF90);
            skSolve(sketch);
        }
        {
            var Q0;
            Q0=makeQuery(id+"F90.imprint","IMPRINT",FACE,{"disambiguationData":[TD([[makeQuery(id+"F90.imprint","IMPRINT",EDGE,{"derivedFrom":sQuery(id+"F90.wireOp",EDGE,"E247.sketch_text.stroke-8")}),-1.0]])]});
            var Q1;
            Q1=makeQuery(id+"F90.imprint","IMPRINT",FACE,{"disambiguationData":[TD([[makeQuery(id+"F90.imprint","IMPRINT",EDGE,{"derivedFrom":sQuery(id+"F90.wireOp",EDGE,"E247.sketch_text.stroke-0")}),-1.0]])]});
            var Q2;
            Q2=makeQuery(id+"F90.imprint","IMPRINT",FACE,{"disambiguationData":[TD([[makeQuery(id+"F90.imprint","IMPRINT",EDGE,{"derivedFrom":sQuery(id+"F90.wireOp",EDGE,"E247.sketch_text.stroke-15")}),-1.0]])]});
            extrude(context, id + "F91", {"entities" : qUnion([Q0, Q1, Q2]), "operationType" : NewBodyOperationType.REMOVE, "oppositeDirection" : true, "depth" : 2 * mm, "offsetDistance" : 25 * mm});
        }
        {
            var Q0;
            Q0=makeQuery(id+"F1.opExtrude","SWEPT_FACE",FACE,{"disambiguationData":[OSD([sQuery(id+"F0.wireOp",EDGE,"E182")])]});
            var sketch = newSketch(context, id + "F92", { "sketchPlane" : qUnion([Q0])});
            skText(sketch, "E248", { "text": "44", "fontName": "AllertaStencil-Regular.ttf"});
            const initialGuessF92  = {"E248": [0.06671, 0.0106, 1, 0, 0.00842]};
            skSetInitialGuess(sketch, initialGuessF92);
            skSolve(sketch);
        }
        {
            var Q0;
            Q0=makeQuery(id+"F92.imprint","IMPRINT",FACE,{"disambiguationData":[TD([[makeQuery(id+"F92.imprint","IMPRINT",EDGE,{"derivedFrom":sQuery(id+"F92.wireOp",EDGE,"E248.sketch_text.stroke-8")}),-1.0]])]});
            var Q1;
            Q1=makeQuery(id+"F92.imprint","IMPRINT",FACE,{"disambiguationData":[TD([[makeQuery(id+"F92.imprint","IMPRINT",EDGE,{"derivedFrom":sQuery(id+"F92.wireOp",EDGE,"E248.sketch_text.stroke-0")}),-1.0]])]});
            var Q2;
            Q2=makeQuery(id+"F92.imprint","IMPRINT",FACE,{"disambiguationData":[TD([[makeQuery(id+"F92.imprint","IMPRINT",EDGE,{"derivedFrom":sQuery(id+"F92.wireOp",EDGE,"E248.sketch_text.stroke-23")}),-1.0]])]});
            var Q3;
            Q3=makeQuery(id+"F92.imprint","IMPRINT",FACE,{"disambiguationData":[TD([[makeQuery(id+"F92.imprint","IMPRINT",EDGE,{"derivedFrom":sQuery(id+"F92.wireOp",EDGE,"E248.sketch_text.stroke-15")}),-1.0]])]});
            extrude(context, id + "F93", {"entities" : qUnion([Q0, Q1, Q2, Q3]), "operationType" : NewBodyOperationType.REMOVE, "oppositeDirection" : true, "depth" : 2 * mm, "offsetDistance" : 25 * mm});
        }
        {
            var Q0;
            Q0=makeQuery(id+"F1.opExtrude","SWEPT_FACE",FACE,{"disambiguationData":[OSD([sQuery(id+"F0.wireOp",EDGE,"E185")])]});
            var sketch = newSketch(context, id + "F94", { "sketchPlane" : qUnion([Q0])});
            skText(sketch, "E249", { "text": "45", "fontName": "AllertaStencil-Regular.ttf"});
            const initialGuessF94  = {"E249": [0.0795, 0.01156, 1, 0, 0.00846]};
            skSetInitialGuess(sketch, initialGuessF94);
            skSolve(sketch);
        }
        {
            var Q0;
            Q0=makeQuery(id+"F94.imprint","IMPRINT",FACE,{"disambiguationData":[TD([[makeQuery(id+"F94.imprint","IMPRINT",EDGE,{"derivedFrom":sQuery(id+"F94.wireOp",EDGE,"E249.sketch_text.stroke-8")}),-1.0]])]});
            var Q1;
            Q1=makeQuery(id+"F94.imprint","IMPRINT",FACE,{"disambiguationData":[TD([[makeQuery(id+"F94.imprint","IMPRINT",EDGE,{"derivedFrom":sQuery(id+"F94.wireOp",EDGE,"E249.sketch_text.stroke-0")}),-1.0]])]});
            var Q2;
            Q2=makeQuery(id+"F94.imprint","IMPRINT",FACE,{"disambiguationData":[TD([[makeQuery(id+"F94.imprint","IMPRINT",EDGE,{"derivedFrom":sQuery(id+"F94.wireOp",EDGE,"E249.sketch_text.stroke-41")}),-1.0]])]});
            var Q3;
            Q3=makeQuery(id+"F94.imprint","IMPRINT",FACE,{"disambiguationData":[TD([[makeQuery(id+"F94.imprint","IMPRINT",EDGE,{"derivedFrom":sQuery(id+"F94.wireOp",EDGE,"E249.sketch_text.stroke-15")}),-1.0]])]});
            extrude(context, id + "F95", {"entities" : qUnion([Q0, Q1, Q2, Q3]), "operationType" : NewBodyOperationType.REMOVE, "oppositeDirection" : true, "depth" : 2 * mm, "offsetDistance" : 25 * mm});
        }
        {
            var Q0;
            Q0=makeQuery(id+"F1.opExtrude","SWEPT_FACE",FACE,{"disambiguationData":[OSD([sQuery(id+"F0.wireOp",EDGE,"E138")])]});
            var sketch = newSketch(context, id + "F96", { "sketchPlane" : qUnion([Q0])});
            skText(sketch, "E250", { "text": "46", "fontName": "AllertaStencil-Regular.ttf"});
            const initialGuessF96  = {"E250": [0.06253, 0.01119, 1, 0, 0.00856]};
            skSetInitialGuess(sketch, initialGuessF96);
            skSolve(sketch);
        }
        {
            var Q0;
            Q0=makeQuery(id+"F96.imprint","IMPRINT",FACE,{"disambiguationData":[TD([[makeQuery(id+"F96.imprint","IMPRINT",EDGE,{"derivedFrom":sQuery(id+"F96.wireOp",EDGE,"E250.sketch_text.stroke-8")}),-1.0]])]});
            var Q1;
            Q1=makeQuery(id+"F96.imprint","IMPRINT",FACE,{"disambiguationData":[TD([[makeQuery(id+"F96.imprint","IMPRINT",EDGE,{"derivedFrom":sQuery(id+"F96.wireOp",EDGE,"E250.sketch_text.stroke-0")}),-1.0]])]});
            var Q2;
            Q2=makeQuery(id+"F96.imprint","IMPRINT",FACE,{"disambiguationData":[TD([[makeQuery(id+"F96.imprint","IMPRINT",EDGE,{"derivedFrom":sQuery(id+"F96.wireOp",EDGE,"E250.sketch_text.stroke-15")}),-1.0]])]});
            var Q3;
            Q3=makeQuery(id+"F96.imprint","IMPRINT",FACE,{"disambiguationData":[TD([[makeQuery(id+"F96.imprint","IMPRINT",EDGE,{"derivedFrom":sQuery(id+"F96.wireOp",EDGE,"E250.sketch_text.stroke-46")}),-1.0]])]});
            extrude(context, id + "F97", {"entities" : qUnion([Q0, Q1, Q2, Q3]), "operationType" : NewBodyOperationType.REMOVE, "oppositeDirection" : true, "depth" : 2 * mm, "offsetDistance" : 25 * mm});
        }
        {
            var Q0;
            Q0=makeQuery(id+"F1.opExtrude","SWEPT_FACE",FACE,{"disambiguationData":[OSD([sQuery(id+"F0.wireOp",EDGE,"E137")])]});
            var sketch = newSketch(context, id + "F98", { "sketchPlane" : qUnion([Q0])});
            skText(sketch, "E251", { "text": "47", "fontName": "AllertaStencil-Regular.ttf"});
            const initialGuessF98  = {"E251": [0.05075, 0.00825, 1, 0, 0.00982]};
            skSetInitialGuess(sketch, initialGuessF98);
            skSolve(sketch);
        }
        {
            var Q0;
            Q0=makeQuery(id+"F98.imprint","IMPRINT",FACE,{"disambiguationData":[TD([[makeQuery(id+"F98.imprint","IMPRINT",EDGE,{"derivedFrom":sQuery(id+"F98.wireOp",EDGE,"E251.sketch_text.stroke-8")}),-1.0]])]});
            var Q1;
            Q1=makeQuery(id+"F98.imprint","IMPRINT",FACE,{"disambiguationData":[TD([[makeQuery(id+"F98.imprint","IMPRINT",EDGE,{"derivedFrom":sQuery(id+"F98.wireOp",EDGE,"E251.sketch_text.stroke-0")}),-1.0]])]});
            var Q2;
            Q2=makeQuery(id+"F98.imprint","IMPRINT",FACE,{"disambiguationData":[TD([[makeQuery(id+"F98.imprint","IMPRINT",EDGE,{"derivedFrom":sQuery(id+"F98.wireOp",EDGE,"E251.sketch_text.stroke-15")}),-1.0]])]});
            extrude(context, id + "F99", {"entities" : qUnion([Q0, Q1, Q2]), "operationType" : NewBodyOperationType.REMOVE, "oppositeDirection" : true, "depth" : 2 * mm, "offsetDistance" : 25 * mm});
        }
        {
            var Q0;
            Q0=makeQuery(id+"F1.opExtrude","SWEPT_FACE",FACE,{"disambiguationData":[OSD([sQuery(id+"F0.wireOp",EDGE,"E157")])]});
            var sketch = newSketch(context, id + "F100", { "sketchPlane" : qUnion([Q0])});
            skText(sketch, "E252", { "text": "48", "fontName": "AllertaStencil-Regular.ttf"});
            const initialGuessF100  = {"E252": [-0.10088, 0.00875, 1, 0, 0.01125]};
            skSetInitialGuess(sketch, initialGuessF100);
            skSolve(sketch);
        }
        {
            var Q0;
            Q0=makeQuery(id+"F100.imprint","IMPRINT",FACE,{"disambiguationData":[TD([[makeQuery(id+"F100.imprint","IMPRINT",EDGE,{"derivedFrom":sQuery(id+"F100.wireOp",EDGE,"E252.sketch_text.stroke-8")}),-1.0]])]});
            var Q1;
            Q1=makeQuery(id+"F100.imprint","IMPRINT",FACE,{"disambiguationData":[TD([[makeQuery(id+"F100.imprint","IMPRINT",EDGE,{"derivedFrom":sQuery(id+"F100.wireOp",EDGE,"E252.sketch_text.stroke-0")}),-1.0]])]});
            var Q2;
            Q2=makeQuery(id+"F100.imprint","IMPRINT",FACE,{"disambiguationData":[TD([[makeQuery(id+"F100.imprint","IMPRINT",EDGE,{"derivedFrom":sQuery(id+"F100.wireOp",EDGE,"E252.sketch_text.stroke-15")}),-1.0]])]});
            var Q3;
            Q3=makeQuery(id+"F100.imprint","IMPRINT",FACE,{"disambiguationData":[TD([[makeQuery(id+"F100.imprint","IMPRINT",EDGE,{"derivedFrom":sQuery(id+"F100.wireOp",EDGE,"E252.sketch_text.stroke-39")}),-1.0]])]});
            extrude(context, id + "F101", {"entities" : qUnion([Q0, Q1, Q2, Q3]), "operationType" : NewBodyOperationType.REMOVE, "oppositeDirection" : true, "depth" : 2 * mm, "offsetDistance" : 25 * mm});
        }
        {
            var Q0;
            Q0=makeQuery(id+"F1.opExtrude","SWEPT_FACE",FACE,{"disambiguationData":[OSD([sQuery(id+"F0.wireOp",EDGE,"E152")])]});
            var sketch = newSketch(context, id + "F102", { "sketchPlane" : qUnion([Q0])});
            skText(sketch, "E253", { "text": "49", "fontName": "AllertaStencil-Regular.ttf"});
            const initialGuessF102  = {"E253": [-0.33707, 0.00706, 1, 0, 0.01192]};
            skSetInitialGuess(sketch, initialGuessF102);
            skSolve(sketch);
        }
        {
            var Q0;
            Q0=makeQuery(id+"F102.imprint","IMPRINT",FACE,{"disambiguationData":[TD([[makeQuery(id+"F102.imprint","IMPRINT",EDGE,{"derivedFrom":sQuery(id+"F102.wireOp",EDGE,"E253.sketch_text.stroke-8")}),-1.0]])]});
            var Q1;
            Q1=makeQuery(id+"F102.imprint","IMPRINT",FACE,{"disambiguationData":[TD([[makeQuery(id+"F102.imprint","IMPRINT",EDGE,{"derivedFrom":sQuery(id+"F102.wireOp",EDGE,"E253.sketch_text.stroke-15")}),-1.0]])]});
            var Q2;
            Q2=makeQuery(id+"F102.imprint","IMPRINT",FACE,{"disambiguationData":[TD([[makeQuery(id+"F102.imprint","IMPRINT",EDGE,{"derivedFrom":sQuery(id+"F102.wireOp",EDGE,"E253.sketch_text.stroke-29")}),-1.0]])]});
            var Q3;
            Q3=makeQuery(id+"F102.imprint","IMPRINT",FACE,{"disambiguationData":[TD([[makeQuery(id+"F102.imprint","IMPRINT",EDGE,{"derivedFrom":sQuery(id+"F102.wireOp",EDGE,"E253.sketch_text.stroke-0")}),-1.0]])]});
            extrude(context, id + "F103", {"entities" : qUnion([Q0, Q1, Q2, Q3]), "operationType" : NewBodyOperationType.REMOVE, "oppositeDirection" : true, "depth" : 2 * mm, "offsetDistance" : 25 * mm});
        }
        {
            var Q0;
            Q0=makeQuery(id+"F1.opExtrude","SWEPT_FACE",FACE,{"disambiguationData":[OSD([sQuery(id+"F0.wireOp",EDGE,"E198")])]});
            var sketch = newSketch(context, id + "F104", { "sketchPlane" : qUnion([Q0])});
            skText(sketch, "E254", { "text": "50", "fontName": "AllertaStencil-Regular.ttf"});
            const initialGuessF104  = {"E254": [-0.16843, 0.0114, 1, 0, 0.00871]};
            skSetInitialGuess(sketch, initialGuessF104);
            skSolve(sketch);
        }
        {
            var Q0;
            Q0=makeQuery(id+"F104.imprint","IMPRINT",FACE,{"disambiguationData":[TD([[makeQuery(id+"F104.imprint","IMPRINT",EDGE,{"derivedFrom":sQuery(id+"F104.wireOp",EDGE,"E254.sketch_text.stroke-26")}),-1.0]])]});
            var Q1;
            Q1=makeQuery(id+"F104.imprint","IMPRINT",FACE,{"disambiguationData":[TD([[makeQuery(id+"F104.imprint","IMPRINT",EDGE,{"derivedFrom":sQuery(id+"F104.wireOp",EDGE,"E254.sketch_text.stroke-0")}),-1.0]])]});
            var Q2;
            Q2=makeQuery(id+"F104.imprint","IMPRINT",FACE,{"disambiguationData":[TD([[makeQuery(id+"F104.imprint","IMPRINT",EDGE,{"derivedFrom":sQuery(id+"F104.wireOp",EDGE,"E254.sketch_text.stroke-41")}),-1.0]])]});
            var Q3;
            Q3=makeQuery(id+"F104.imprint","IMPRINT",FACE,{"disambiguationData":[TD([[makeQuery(id+"F104.imprint","IMPRINT",EDGE,{"derivedFrom":sQuery(id+"F104.wireOp",EDGE,"E254.sketch_text.stroke-57")}),-1.0]])]});
            extrude(context, id + "F105", {"entities" : qUnion([Q0, Q1, Q2, Q3]), "operationType" : NewBodyOperationType.REMOVE, "oppositeDirection" : true, "depth" : 2 * mm, "offsetDistance" : 25 * mm});
        }
        {
            var Q0;
            Q0=makeQuery(id+"F2.opExtrude","SWEPT_FACE",FACE,{"disambiguationData":[OSD([sQuery(id+"F0.wireOp",EDGE,"E62")])]});
            var sketch = newSketch(context, id + "F106", { "sketchPlane" : qUnion([Q0])});
            skText(sketch, "E255", { "text": "51", "fontName": "AllertaStencil-Regular.ttf"});
            const initialGuessF106  = {"E255": [0.04274, 0.00578, 1, 0, 0.01292]};
            skSetInitialGuess(sketch, initialGuessF106);
            skSolve(sketch);
        }
        {
            var Q0;
            Q0=makeQuery(id+"F106.imprint","IMPRINT",FACE,{"disambiguationData":[TD([[makeQuery(id+"F106.imprint","IMPRINT",EDGE,{"derivedFrom":sQuery(id+"F106.wireOp",EDGE,"E255.sketch_text.stroke-26")}),-1.0]])]});
            var Q1;
            Q1=makeQuery(id+"F106.imprint","IMPRINT",FACE,{"disambiguationData":[TD([[makeQuery(id+"F106.imprint","IMPRINT",EDGE,{"derivedFrom":sQuery(id+"F106.wireOp",EDGE,"E255.sketch_text.stroke-0")}),-1.0]])]});
            var Q2;
            Q2=makeQuery(id+"F106.imprint","IMPRINT",FACE,{"disambiguationData":[TD([[makeQuery(id+"F106.imprint","IMPRINT",EDGE,{"derivedFrom":sQuery(id+"F106.wireOp",EDGE,"E255.sketch_text.stroke-41")}),-1.0]])]});
            extrude(context, id + "F107", {"entities" : qUnion([Q0, Q1, Q2]), "operationType" : NewBodyOperationType.REMOVE, "oppositeDirection" : true, "depth" : 2 * mm, "offsetDistance" : 25 * mm});
        }
        {
            var Q0;
            Q0=makeQuery(id+"F2.opExtrude","SWEPT_FACE",FACE,{"disambiguationData":[OSD([sQuery(id+"F0.wireOp",EDGE,"E133")])]});
            var sketch = newSketch(context, id + "F108", { "sketchPlane" : qUnion([Q0])});
            skText(sketch, "E256", { "text": "52", "fontName": "AllertaStencil-Regular.ttf"});
            const initialGuessF108  = {"E256": [0.07705, 0.00465, 1, 0, 0.01449]};
            skSetInitialGuess(sketch, initialGuessF108);
            skSolve(sketch);
        }
        {
            var Q0;
            Q0=makeQuery(id+"F108.imprint","IMPRINT",FACE,{"disambiguationData":[TD([[makeQuery(id+"F108.imprint","IMPRINT",EDGE,{"derivedFrom":sQuery(id+"F108.wireOp",EDGE,"E256.sketch_text.stroke-26")}),-1.0]])]});
            var Q1;
            Q1=makeQuery(id+"F108.imprint","IMPRINT",FACE,{"disambiguationData":[TD([[makeQuery(id+"F108.imprint","IMPRINT",EDGE,{"derivedFrom":sQuery(id+"F108.wireOp",EDGE,"E256.sketch_text.stroke-0")}),-1.0]])]});
            var Q2;
            Q2=makeQuery(id+"F108.imprint","IMPRINT",FACE,{"disambiguationData":[TD([[makeQuery(id+"F108.imprint","IMPRINT",EDGE,{"derivedFrom":sQuery(id+"F108.wireOp",EDGE,"E256.sketch_text.stroke-41")}),-1.0]])]});
            extrude(context, id + "F109", {"entities" : qUnion([Q0, Q1, Q2]), "operationType" : NewBodyOperationType.REMOVE, "oppositeDirection" : true, "depth" : 2 * mm, "offsetDistance" : 25 * mm});
        }
        {
            var Q0;
            Q0=makeQuery(id+"F2.opExtrude","SWEPT_FACE",FACE,{"disambiguationData":[OSD([sQuery(id+"F0.wireOp",EDGE,"E40")])]});
            var sketch = newSketch(context, id + "F110", { "sketchPlane" : qUnion([Q0])});
            skText(sketch, "E257", { "text": "53", "fontName": "AllertaStencil-Regular.ttf"});
            const initialGuessF110  = {"E257": [0.20109, 0.0062, 1, 0, 0.01435]};
            skSetInitialGuess(sketch, initialGuessF110);
            skSolve(sketch);
        }
        {
            var Q0;
            Q0=makeQuery(id+"F110.imprint","IMPRINT",FACE,{"disambiguationData":[TD([[makeQuery(id+"F110.imprint","IMPRINT",EDGE,{"derivedFrom":sQuery(id+"F110.wireOp",EDGE,"E257.sketch_text.stroke-26")}),-1.0]])]});
            var Q1;
            Q1=makeQuery(id+"F110.imprint","IMPRINT",FACE,{"disambiguationData":[TD([[makeQuery(id+"F110.imprint","IMPRINT",EDGE,{"derivedFrom":sQuery(id+"F110.wireOp",EDGE,"E257.sketch_text.stroke-0")}),-1.0]])]});
            var Q2;
            Q2=makeQuery(id+"F110.imprint","IMPRINT",FACE,{"disambiguationData":[TD([[makeQuery(id+"F110.imprint","IMPRINT",EDGE,{"derivedFrom":sQuery(id+"F110.wireOp",EDGE,"E257.sketch_text.stroke-41")}),-1.0]])]});
            extrude(context, id + "F111", {"entities" : qUnion([Q0, Q1, Q2]), "operationType" : NewBodyOperationType.REMOVE, "oppositeDirection" : true, "depth" : 2 * mm, "offsetDistance" : 25 * mm});
        }
        {
            var Q0;
            Q0=makeQuery(id+"F2.opExtrude","SWEPT_FACE",FACE,{"disambiguationData":[OSD([sQuery(id+"F0.wireOp",EDGE,"E200")])]});
            var sketch = newSketch(context, id + "F112", { "sketchPlane" : qUnion([Q0])});
            skText(sketch, "E258", { "text": "54", "fontName": "AllertaStencil-Regular.ttf"});
            const initialGuessF112  = {"E258": [0.21723, 0.00561, 1, 0, 0.0143]};
            skSetInitialGuess(sketch, initialGuessF112);
            skSolve(sketch);
        }
        {
            var Q0;
            Q0=makeQuery(id+"F112.imprint","IMPRINT",FACE,{"disambiguationData":[TD([[makeQuery(id+"F112.imprint","IMPRINT",EDGE,{"derivedFrom":sQuery(id+"F112.wireOp",EDGE,"E258.sketch_text.stroke-26")}),-1.0]])]});
            var Q1;
            Q1=makeQuery(id+"F112.imprint","IMPRINT",FACE,{"disambiguationData":[TD([[makeQuery(id+"F112.imprint","IMPRINT",EDGE,{"derivedFrom":sQuery(id+"F112.wireOp",EDGE,"E258.sketch_text.stroke-0")}),-1.0]])]});
            var Q2;
            Q2=makeQuery(id+"F112.imprint","IMPRINT",FACE,{"disambiguationData":[TD([[makeQuery(id+"F112.imprint","IMPRINT",EDGE,{"derivedFrom":sQuery(id+"F112.wireOp",EDGE,"E258.sketch_text.stroke-49")}),-1.0]])]});
            var Q3;
            Q3=makeQuery(id+"F112.imprint","IMPRINT",FACE,{"disambiguationData":[TD([[makeQuery(id+"F112.imprint","IMPRINT",EDGE,{"derivedFrom":sQuery(id+"F112.wireOp",EDGE,"E258.sketch_text.stroke-41")}),-1.0]])]});
            extrude(context, id + "F113", {"entities" : qUnion([Q0, Q1, Q2, Q3]), "operationType" : NewBodyOperationType.REMOVE, "oppositeDirection" : true, "depth" : 2 * mm, "offsetDistance" : 25 * mm});
        }
        {
            var Q0;
            Q0=makeQuery(id+"F2.opExtrude","SWEPT_FACE",FACE,{"disambiguationData":[OSD([sQuery(id+"F0.wireOp",EDGE,"E38")])]});
            var sketch = newSketch(context, id + "F114", { "sketchPlane" : qUnion([Q0])});
            skText(sketch, "E259", { "text": "55", "fontName": "AllertaStencil-Regular.ttf"});
            const initialGuessF114  = {"E259": [0.0686, 0.01618, 1, 0, 0.00502]};
            skSetInitialGuess(sketch, initialGuessF114);
            skSolve(sketch);
        }
        {
            var Q0;
            Q0=makeQuery(id+"F114.imprint","IMPRINT",FACE,{"disambiguationData":[TD([[makeQuery(id+"F114.imprint","IMPRINT",EDGE,{"derivedFrom":sQuery(id+"F114.wireOp",EDGE,"E259.sketch_text.stroke-26")}),-1.0]])]});
            var Q1;
            Q1=makeQuery(id+"F114.imprint","IMPRINT",FACE,{"disambiguationData":[TD([[makeQuery(id+"F114.imprint","IMPRINT",EDGE,{"derivedFrom":sQuery(id+"F114.wireOp",EDGE,"E259.sketch_text.stroke-0")}),-1.0]])]});
            var Q2;
            Q2=makeQuery(id+"F114.imprint","IMPRINT",FACE,{"disambiguationData":[TD([[makeQuery(id+"F114.imprint","IMPRINT",EDGE,{"derivedFrom":sQuery(id+"F114.wireOp",EDGE,"E259.sketch_text.stroke-41")}),-1.0]])]});
            var Q3;
            Q3=makeQuery(id+"F114.imprint","IMPRINT",FACE,{"disambiguationData":[TD([[makeQuery(id+"F114.imprint","IMPRINT",EDGE,{"derivedFrom":sQuery(id+"F114.wireOp",EDGE,"E259.sketch_text.stroke-67")}),-1.0]])]});
            extrude(context, id + "F115", {"entities" : qUnion([Q0, Q1, Q2, Q3]), "operationType" : NewBodyOperationType.REMOVE, "oppositeDirection" : true, "depth" : 2 * mm, "offsetDistance" : 25 * mm});
        }
        {
            var Q0;
            Q0=makeQuery(id+"F2.opExtrude","SWEPT_FACE",FACE,{"disambiguationData":[OSD([sQuery(id+"F0.wireOp",EDGE,"E160")])]});
            var sketch = newSketch(context, id + "F116", { "sketchPlane" : qUnion([Q0])});
            skText(sketch, "E260", { "text": "56", "fontName": "AllertaStencil-Regular.ttf"});
            const initialGuessF116  = {"E260": [0.08337, 0.01196, 1, 0, 0.00601]};
            skSetInitialGuess(sketch, initialGuessF116);
            skSolve(sketch);
        }
        {
            var Q0;
            Q0=makeQuery(id+"F116.imprint","IMPRINT",FACE,{"disambiguationData":[TD([[makeQuery(id+"F116.imprint","IMPRINT",EDGE,{"derivedFrom":sQuery(id+"F116.wireOp",EDGE,"E260.sketch_text.stroke-26")}),-1.0]])]});
            var Q1;
            Q1=makeQuery(id+"F116.imprint","IMPRINT",FACE,{"disambiguationData":[TD([[makeQuery(id+"F116.imprint","IMPRINT",EDGE,{"derivedFrom":sQuery(id+"F116.wireOp",EDGE,"E260.sketch_text.stroke-0")}),-1.0]])]});
            var Q2;
            Q2=makeQuery(id+"F116.imprint","IMPRINT",FACE,{"disambiguationData":[TD([[makeQuery(id+"F116.imprint","IMPRINT",EDGE,{"derivedFrom":sQuery(id+"F116.wireOp",EDGE,"E260.sketch_text.stroke-72")}),-1.0]])]});
            var Q3;
            Q3=makeQuery(id+"F116.imprint","IMPRINT",FACE,{"disambiguationData":[TD([[makeQuery(id+"F116.imprint","IMPRINT",EDGE,{"derivedFrom":sQuery(id+"F116.wireOp",EDGE,"E260.sketch_text.stroke-41")}),-1.0]])]});
            extrude(context, id + "F117", {"entities" : qUnion([Q0, Q1, Q2, Q3]), "operationType" : NewBodyOperationType.REMOVE, "oppositeDirection" : true, "depth" : 2 * mm, "offsetDistance" : 25 * mm});
        }
        {
            var Q0;
            Q0=makeQuery(id+"F2.opExtrude","SWEPT_FACE",FACE,{"disambiguationData":[OSD([sQuery(id+"F0.wireOp",EDGE,"E68")])]});
            var sketch = newSketch(context, id + "F118", { "sketchPlane" : qUnion([Q0])});
            skText(sketch, "E261", { "text": "57", "fontName": "AllertaStencil-Regular.ttf"});
            const initialGuessF118  = {"E261": [-0.32774, 0.00885, 1, 0, 0.00947]};
            skSetInitialGuess(sketch, initialGuessF118);
            skSolve(sketch);
        }
        {
            var Q0;
            Q0=makeQuery(id+"F118.imprint","IMPRINT",FACE,{"disambiguationData":[TD([[makeQuery(id+"F118.imprint","IMPRINT",EDGE,{"derivedFrom":sQuery(id+"F118.wireOp",EDGE,"E261.sketch_text.stroke-26")}),-1.0]])]});
            var Q1;
            Q1=makeQuery(id+"F118.imprint","IMPRINT",FACE,{"disambiguationData":[TD([[makeQuery(id+"F118.imprint","IMPRINT",EDGE,{"derivedFrom":sQuery(id+"F118.wireOp",EDGE,"E261.sketch_text.stroke-0")}),-1.0]])]});
            var Q2;
            Q2=makeQuery(id+"F118.imprint","IMPRINT",FACE,{"disambiguationData":[TD([[makeQuery(id+"F118.imprint","IMPRINT",EDGE,{"derivedFrom":sQuery(id+"F118.wireOp",EDGE,"E261.sketch_text.stroke-41")}),-1.0]])]});
            extrude(context, id + "F119", {"entities" : qUnion([Q0, Q1, Q2]), "operationType" : NewBodyOperationType.REMOVE, "oppositeDirection" : true, "depth" : 2 * mm, "offsetDistance" : 25 * mm});
        }
        {
            var Q0;
            Q0=makeQuery(id+"F2.opExtrude","SWEPT_FACE",FACE,{"disambiguationData":[OSD([sQuery(id+"F0.wireOp",EDGE,"E80")])]});
            var sketch = newSketch(context, id + "F120", { "sketchPlane" : qUnion([Q0])});
            skText(sketch, "E262", { "text": "58", "fontName": "AllertaStencil-Regular.ttf"});
            const initialGuessF120  = {"E262": [-0.42083, 0.00638, 1, 0, 0.01344]};
            skSetInitialGuess(sketch, initialGuessF120);
            skSolve(sketch);
        }
        {
            var Q0;
            Q0=makeQuery(id+"F120.imprint","IMPRINT",FACE,{"disambiguationData":[TD([[makeQuery(id+"F120.imprint","IMPRINT",EDGE,{"derivedFrom":sQuery(id+"F120.wireOp",EDGE,"E262.sketch_text.stroke-26")}),-1.0]])]});
            var Q1;
            Q1=makeQuery(id+"F120.imprint","IMPRINT",FACE,{"disambiguationData":[TD([[makeQuery(id+"F120.imprint","IMPRINT",EDGE,{"derivedFrom":sQuery(id+"F120.wireOp",EDGE,"E262.sketch_text.stroke-0")}),-1.0]])]});
            var Q2;
            Q2=makeQuery(id+"F120.imprint","IMPRINT",FACE,{"disambiguationData":[TD([[makeQuery(id+"F120.imprint","IMPRINT",EDGE,{"derivedFrom":sQuery(id+"F120.wireOp",EDGE,"E262.sketch_text.stroke-41")}),-1.0]])]});
            var Q3;
            Q3=makeQuery(id+"F120.imprint","IMPRINT",FACE,{"disambiguationData":[TD([[makeQuery(id+"F120.imprint","IMPRINT",EDGE,{"derivedFrom":sQuery(id+"F120.wireOp",EDGE,"E262.sketch_text.stroke-65")}),-1.0]])]});
            extrude(context, id + "F121", {"entities" : qUnion([Q0, Q1, Q2, Q3]), "operationType" : NewBodyOperationType.REMOVE, "oppositeDirection" : true, "depth" : 2 * mm, "offsetDistance" : 25 * mm});
        }
        {
            var Q0;
            Q0=makeQuery(id+"F2.opExtrude","SWEPT_FACE",FACE,{"disambiguationData":[OSD([sQuery(id+"F0.wireOp",EDGE,"E148")])]});
            var sketch = newSketch(context, id + "F122", { "sketchPlane" : qUnion([Q0])});
            skText(sketch, "E263", { "text": "59", "fontName": "AllertaStencil-Regular.ttf"});
            const initialGuessF122  = {"E263": [-0.37752, 0.0053, 1, 0, 0.01411]};
            skSetInitialGuess(sketch, initialGuessF122);
            skSolve(sketch);
        }
        {
            var Q0;
            Q0=makeQuery(id+"F122.imprint","IMPRINT",FACE,{"disambiguationData":[TD([[makeQuery(id+"F122.imprint","IMPRINT",EDGE,{"derivedFrom":sQuery(id+"F122.wireOp",EDGE,"E263.sketch_text.stroke-26")}),-1.0]])]});
            var Q1;
            Q1=makeQuery(id+"F122.imprint","IMPRINT",FACE,{"disambiguationData":[TD([[makeQuery(id+"F122.imprint","IMPRINT",EDGE,{"derivedFrom":sQuery(id+"F122.wireOp",EDGE,"E263.sketch_text.stroke-0")}),-1.0]])]});
            var Q2;
            Q2=makeQuery(id+"F122.imprint","IMPRINT",FACE,{"disambiguationData":[TD([[makeQuery(id+"F122.imprint","IMPRINT",EDGE,{"derivedFrom":sQuery(id+"F122.wireOp",EDGE,"E263.sketch_text.stroke-41")}),-1.0]])]});
            var Q3;
            Q3=makeQuery(id+"F122.imprint","IMPRINT",FACE,{"disambiguationData":[TD([[makeQuery(id+"F122.imprint","IMPRINT",EDGE,{"derivedFrom":sQuery(id+"F122.wireOp",EDGE,"E263.sketch_text.stroke-55")}),-1.0]])]});
            extrude(context, id + "F123", {"entities" : qUnion([Q0, Q1, Q2, Q3]), "operationType" : NewBodyOperationType.REMOVE, "oppositeDirection" : true, "depth" : 2 * mm, "offsetDistance" : 25 * mm});
        }
        {
            var Q0;
            Q0=makeQuery(id+"F2.opExtrude","SWEPT_FACE",FACE,{"disambiguationData":[OSD([sQuery(id+"F0.wireOp",EDGE,"E123")])]});
            var sketch = newSketch(context, id + "F124", { "sketchPlane" : qUnion([Q0])});
            skText(sketch, "E264", { "text": "60", "fontName": "AllertaStencil-Regular.ttf"});
            const initialGuessF124  = {"E264": [-0.20572, 0.00612, 1, 0, 0.013]};
            skSetInitialGuess(sketch, initialGuessF124);
            skSolve(sketch);
        }
        {
            var Q0;
            Q0=makeQuery(id+"F124.imprint","IMPRINT",FACE,{"disambiguationData":[TD([[makeQuery(id+"F124.imprint","IMPRINT",EDGE,{"derivedFrom":sQuery(id+"F124.wireOp",EDGE,"E264.sketch_text.stroke-0")}),-1.0]])]});
            var Q1;
            Q1=makeQuery(id+"F124.imprint","IMPRINT",FACE,{"disambiguationData":[TD([[makeQuery(id+"F124.imprint","IMPRINT",EDGE,{"derivedFrom":sQuery(id+"F124.wireOp",EDGE,"E264.sketch_text.stroke-31")}),-1.0]])]});
            var Q2;
            Q2=makeQuery(id+"F124.imprint","IMPRINT",FACE,{"disambiguationData":[TD([[makeQuery(id+"F124.imprint","IMPRINT",EDGE,{"derivedFrom":sQuery(id+"F124.wireOp",EDGE,"E264.sketch_text.stroke-45")}),-1.0]])]});
            var Q3;
            Q3=makeQuery(id+"F124.imprint","IMPRINT",FACE,{"disambiguationData":[TD([[makeQuery(id+"F124.imprint","IMPRINT",EDGE,{"derivedFrom":sQuery(id+"F124.wireOp",EDGE,"E264.sketch_text.stroke-61")}),-1.0]])]});
            extrude(context, id + "F125", {"entities" : qUnion([Q0, Q1, Q2, Q3]), "operationType" : NewBodyOperationType.REMOVE, "oppositeDirection" : true, "depth" : 2 * mm, "offsetDistance" : 25 * mm});
        }
        {
            var Q0;
            Q0=makeQuery(id+"F5.opPattern","COPY",BODY,{"derivedFrom":makeQuery(id+"F1.opExtrude","SWEPT_BODY",BODY,{"disambiguationData":[OSD([sQuery(id+"F0.wireOp",EDGE,"E3"),sQuery(id+"F0.wireOp",EDGE,"E53"),sQuery(id+"F0.wireOp",EDGE,"E54")])]}),"instanceName":"1"});
            deleteBodies(context, id + "F126", {"entities" : qUnion([Q0])});
        }
        {
            var Q0;
            Q0=makeQuery(id+"F2.opExtrude","SWEPT_FACE",FACE,{"disambiguationData":[OSD([sQuery(id+"F0.wireOp",EDGE,"E107")])]});
            var sketch = newSketch(context, id + "F127", { "sketchPlane" : qUnion([Q0])});
            skText(sketch, "E265", { "text": "61", "fontName": "AllertaStencil-Regular.ttf"});
            const initialGuessF127  = {"E265": [-0.10947, 0.00766, 1, 0, 0.01356]};
            skSetInitialGuess(sketch, initialGuessF127);
            skSolve(sketch);
        }
        {
            var Q0;
            Q0=makeQuery(id+"F127.imprint","IMPRINT",FACE,{"disambiguationData":[TD([[makeQuery(id+"F127.imprint","IMPRINT",EDGE,{"derivedFrom":sQuery(id+"F127.wireOp",EDGE,"E265.sketch_text.stroke-0")}),-1.0]])]});
            var Q1;
            Q1=makeQuery(id+"F127.imprint","IMPRINT",FACE,{"disambiguationData":[TD([[makeQuery(id+"F127.imprint","IMPRINT",EDGE,{"derivedFrom":sQuery(id+"F127.wireOp",EDGE,"E265.sketch_text.stroke-31")}),-1.0]])]});
            var Q2;
            Q2=makeQuery(id+"F127.imprint","IMPRINT",FACE,{"disambiguationData":[TD([[makeQuery(id+"F127.imprint","IMPRINT",EDGE,{"derivedFrom":sQuery(id+"F127.wireOp",EDGE,"E265.sketch_text.stroke-45")}),-1.0]])]});
            extrude(context, id + "F128", {"entities" : qUnion([Q0, Q1, Q2]), "operationType" : NewBodyOperationType.REMOVE, "oppositeDirection" : true, "depth" : 2 * mm, "offsetDistance" : 25 * mm});
        }
        {
            var Q0;
            Q0=makeQuery(id+"F2.opExtrude","SWEPT_FACE",FACE,{"disambiguationData":[OSD([sQuery(id+"F0.wireOp",EDGE,"E71")])]});
            var sketch = newSketch(context, id + "F129", { "sketchPlane" : qUnion([Q0])});
            skText(sketch, "E266", { "text": "62", "fontName": "AllertaStencil-Regular.ttf"});
            const initialGuessF129  = {"E266": [0.4625, 0.0093, 1, 0, 0.0098]};
            skSetInitialGuess(sketch, initialGuessF129);
            skSolve(sketch);
        }
        {
            var Q0;
            Q0=makeQuery(id+"F129.imprint","IMPRINT",FACE,{"disambiguationData":[TD([[makeQuery(id+"F129.imprint","IMPRINT",EDGE,{"derivedFrom":sQuery(id+"F129.wireOp",EDGE,"E266.sketch_text.stroke-0")}),-1.0]])]});
            var Q1;
            Q1=makeQuery(id+"F129.imprint","IMPRINT",FACE,{"disambiguationData":[TD([[makeQuery(id+"F129.imprint","IMPRINT",EDGE,{"derivedFrom":sQuery(id+"F129.wireOp",EDGE,"E266.sketch_text.stroke-31")}),-1.0]])]});
            var Q2;
            Q2=makeQuery(id+"F129.imprint","IMPRINT",FACE,{"disambiguationData":[TD([[makeQuery(id+"F129.imprint","IMPRINT",EDGE,{"derivedFrom":sQuery(id+"F129.wireOp",EDGE,"E266.sketch_text.stroke-45")}),-1.0]])]});
            extrude(context, id + "F130", {"entities" : qUnion([Q0, Q1, Q2]), "operationType" : NewBodyOperationType.REMOVE, "oppositeDirection" : true, "depth" : 2 * mm, "offsetDistance" : 25 * mm});
        }
        {
            var Q0;
            Q0=makeQuery(id+"F2.opExtrude","SWEPT_FACE",FACE,{"disambiguationData":[OSD([sQuery(id+"F0.wireOp",EDGE,"E69")])]});
            var sketch = newSketch(context, id + "F131", { "sketchPlane" : qUnion([Q0])});
            skText(sketch, "E267", { "text": "63", "fontName": "AllertaStencil-Regular.ttf"});
            const initialGuessF131  = {"E267": [0.50585, 0.00931, 1, 0, 0.0113]};
            skSetInitialGuess(sketch, initialGuessF131);
            skSolve(sketch);
        }
        {
            var Q0;
            Q0=makeQuery(id+"F131.imprint","IMPRINT",FACE,{"disambiguationData":[TD([[makeQuery(id+"F131.imprint","IMPRINT",EDGE,{"derivedFrom":sQuery(id+"F131.wireOp",EDGE,"E267.sketch_text.stroke-45")}),-1.0]])]});
            var Q1;
            Q1=makeQuery(id+"F131.imprint","IMPRINT",FACE,{"disambiguationData":[TD([[makeQuery(id+"F131.imprint","IMPRINT",EDGE,{"derivedFrom":sQuery(id+"F131.wireOp",EDGE,"E267.sketch_text.stroke-31")}),-1.0]])]});
            var Q2;
            Q2=makeQuery(id+"F131.imprint","IMPRINT",FACE,{"disambiguationData":[TD([[makeQuery(id+"F131.imprint","IMPRINT",EDGE,{"derivedFrom":sQuery(id+"F131.wireOp",EDGE,"E267.sketch_text.stroke-0")}),-1.0]])]});
            extrude(context, id + "F132", {"entities" : qUnion([Q0, Q1, Q2]), "operationType" : NewBodyOperationType.REMOVE, "oppositeDirection" : true, "depth" : 2 * mm, "offsetDistance" : 25 * mm});
        }
        {
            var Q0;
            Q0=makeQuery(id+"F2.opExtrude","SWEPT_FACE",FACE,{"disambiguationData":[OSD([sQuery(id+"F0.wireOp",EDGE,"E33")])]});
            var sketch = newSketch(context, id + "F133", { "sketchPlane" : qUnion([Q0])});
            skText(sketch, "E268", { "text": "64", "fontName": "AllertaStencil-Regular.ttf"});
            const initialGuessF133  = {"E268": [0.09223, 0.01192, 1, 0, 0.00947]};
            skSetInitialGuess(sketch, initialGuessF133);
            skSolve(sketch);
        }
        {
            var Q0;
            Q0=makeQuery(id+"F133.imprint","IMPRINT",FACE,{"disambiguationData":[TD([[makeQuery(id+"F133.imprint","IMPRINT",EDGE,{"derivedFrom":sQuery(id+"F133.wireOp",EDGE,"E268.sketch_text.stroke-0")}),-1.0]])]});
            var Q1;
            Q1=makeQuery(id+"F133.imprint","IMPRINT",FACE,{"disambiguationData":[TD([[makeQuery(id+"F133.imprint","IMPRINT",EDGE,{"derivedFrom":sQuery(id+"F133.wireOp",EDGE,"E268.sketch_text.stroke-31")}),-1.0]])]});
            var Q2;
            Q2=makeQuery(id+"F133.imprint","IMPRINT",FACE,{"disambiguationData":[TD([[makeQuery(id+"F133.imprint","IMPRINT",EDGE,{"derivedFrom":sQuery(id+"F133.wireOp",EDGE,"E268.sketch_text.stroke-53")}),-1.0]])]});
            var Q3;
            Q3=makeQuery(id+"F133.imprint","IMPRINT",FACE,{"disambiguationData":[TD([[makeQuery(id+"F133.imprint","IMPRINT",EDGE,{"derivedFrom":sQuery(id+"F133.wireOp",EDGE,"E268.sketch_text.stroke-45")}),-1.0]])]});
            extrude(context, id + "F134", {"entities" : qUnion([Q0, Q1, Q2, Q3]), "operationType" : NewBodyOperationType.REMOVE, "oppositeDirection" : true, "depth" : 2 * mm, "offsetDistance" : 25 * mm});
        }
        {
            var Q0;
            Q0=makeQuery(id+"F2.opExtrude","SWEPT_FACE",FACE,{"disambiguationData":[OSD([sQuery(id+"F0.wireOp",EDGE,"E126")])]});
            var sketch = newSketch(context, id + "F135", { "sketchPlane" : qUnion([Q0])});
            skText(sketch, "E269", { "text": "65", "fontName": "AllertaStencil-Regular.ttf"});
            const initialGuessF135  = {"E269": [-0.14014, 0.00717, 1, 0, 0.01248]};
            skSetInitialGuess(sketch, initialGuessF135);
            skSolve(sketch);
        }
        {
            var Q0;
            Q0=makeQuery(id+"F135.imprint","IMPRINT",FACE,{"disambiguationData":[TD([[makeQuery(id+"F135.imprint","IMPRINT",EDGE,{"derivedFrom":sQuery(id+"F135.wireOp",EDGE,"E269.sketch_text.stroke-0")}),-1.0]])]});
            var Q1;
            Q1=makeQuery(id+"F135.imprint","IMPRINT",FACE,{"disambiguationData":[TD([[makeQuery(id+"F135.imprint","IMPRINT",EDGE,{"derivedFrom":sQuery(id+"F135.wireOp",EDGE,"E269.sketch_text.stroke-31")}),-1.0]])]});
            var Q2;
            Q2=makeQuery(id+"F135.imprint","IMPRINT",FACE,{"disambiguationData":[TD([[makeQuery(id+"F135.imprint","IMPRINT",EDGE,{"derivedFrom":sQuery(id+"F135.wireOp",EDGE,"E269.sketch_text.stroke-71")}),-1.0]])]});
            var Q3;
            Q3=makeQuery(id+"F135.imprint","IMPRINT",FACE,{"disambiguationData":[TD([[makeQuery(id+"F135.imprint","IMPRINT",EDGE,{"derivedFrom":sQuery(id+"F135.wireOp",EDGE,"E269.sketch_text.stroke-45")}),-1.0]])]});
            extrude(context, id + "F136", {"entities" : qUnion([Q0, Q1, Q2, Q3]), "operationType" : NewBodyOperationType.REMOVE, "oppositeDirection" : true, "depth" : 2 * mm, "offsetDistance" : 25 * mm});
        }
        {
            var Q0;
            Q0=makeQuery(id+"F2.opExtrude","SWEPT_FACE",FACE,{"disambiguationData":[OSD([sQuery(id+"F0.wireOp",EDGE,"E42")])]});
            var sketch = newSketch(context, id + "F137", { "sketchPlane" : qUnion([Q0])});
            skText(sketch, "E270", { "text": "66", "fontName": "AllertaStencil-Regular.ttf"});
            const initialGuessF137  = {"E270": [0.29323, 0.00724, 1, 0, 0.01295]};
            skSetInitialGuess(sketch, initialGuessF137);
            skSolve(sketch);
        }
        {
            var Q0;
            Q0=makeQuery(id+"F137.imprint","IMPRINT",FACE,{"disambiguationData":[TD([[makeQuery(id+"F137.imprint","IMPRINT",EDGE,{"derivedFrom":sQuery(id+"F137.wireOp",EDGE,"E270.sketch_text.stroke-0")}),-1.0]])]});
            var Q1;
            Q1=makeQuery(id+"F137.imprint","IMPRINT",FACE,{"disambiguationData":[TD([[makeQuery(id+"F137.imprint","IMPRINT",EDGE,{"derivedFrom":sQuery(id+"F137.wireOp",EDGE,"E270.sketch_text.stroke-31")}),-1.0]])]});
            var Q2;
            Q2=makeQuery(id+"F137.imprint","IMPRINT",FACE,{"disambiguationData":[TD([[makeQuery(id+"F137.imprint","IMPRINT",EDGE,{"derivedFrom":sQuery(id+"F137.wireOp",EDGE,"E270.sketch_text.stroke-45")}),-1.0]])]});
            var Q3;
            Q3=makeQuery(id+"F137.imprint","IMPRINT",FACE,{"disambiguationData":[TD([[makeQuery(id+"F137.imprint","IMPRINT",EDGE,{"derivedFrom":sQuery(id+"F137.wireOp",EDGE,"E270.sketch_text.stroke-76")}),-1.0]])]});
            extrude(context, id + "F138", {"entities" : qUnion([Q0, Q1, Q2, Q3]), "operationType" : NewBodyOperationType.REMOVE, "oppositeDirection" : true, "depth" : 2 * mm, "offsetDistance" : 25 * mm});
        }
        {
            var Q0;
            Q0=makeQuery(id+"F2.opExtrude","SWEPT_FACE",FACE,{"disambiguationData":[OSD([sQuery(id+"F0.wireOp",EDGE,"E45")])]});
            var sketch = newSketch(context, id + "F139", { "sketchPlane" : qUnion([Q0])});
            skText(sketch, "E271", { "text": "67", "fontName": "AllertaStencil-Regular.ttf"});
            const initialGuessF139  = {"E271": [-0.25562, 0.00918, 1, 0, 0.0111]};
            skSetInitialGuess(sketch, initialGuessF139);
            skSolve(sketch);
        }
        {
            var Q0;
            Q0=makeQuery(id+"F139.imprint","IMPRINT",FACE,{"disambiguationData":[TD([[makeQuery(id+"F139.imprint","IMPRINT",EDGE,{"derivedFrom":sQuery(id+"F139.wireOp",EDGE,"E271.sketch_text.stroke-0")}),-1.0]])]});
            var Q1;
            Q1=makeQuery(id+"F139.imprint","IMPRINT",FACE,{"disambiguationData":[TD([[makeQuery(id+"F139.imprint","IMPRINT",EDGE,{"derivedFrom":sQuery(id+"F139.wireOp",EDGE,"E271.sketch_text.stroke-31")}),-1.0]])]});
            var Q2;
            Q2=makeQuery(id+"F139.imprint","IMPRINT",FACE,{"disambiguationData":[TD([[makeQuery(id+"F139.imprint","IMPRINT",EDGE,{"derivedFrom":sQuery(id+"F139.wireOp",EDGE,"E271.sketch_text.stroke-45")}),-1.0]])]});
            extrude(context, id + "F140", {"entities" : qUnion([Q0, Q1, Q2]), "operationType" : NewBodyOperationType.REMOVE, "oppositeDirection" : true, "depth" : 2 * mm, "offsetDistance" : 25 * mm});
        }
        {
            var Q0;
            Q0=makeQuery(id+"F2.opExtrude","SWEPT_FACE",FACE,{"disambiguationData":[OSD([sQuery(id+"F0.wireOp",EDGE,"E192")])]});
            var sketch = newSketch(context, id + "F141", { "sketchPlane" : qUnion([Q0])});
            skText(sketch, "E272", { "text": "68", "fontName": "AllertaStencil-Regular.ttf"});
            const initialGuessF141  = {"E272": [-0.07956, 0.01347, 1, 0, 0.00741]};
            skSetInitialGuess(sketch, initialGuessF141);
            skSolve(sketch);
        }
        {
            var Q0;
            Q0=makeQuery(id+"F141.imprint","IMPRINT",FACE,{"disambiguationData":[TD([[makeQuery(id+"F141.imprint","IMPRINT",EDGE,{"derivedFrom":sQuery(id+"F141.wireOp",EDGE,"E272.sketch_text.stroke-0")}),-1.0]])]});
            var Q1;
            Q1=makeQuery(id+"F141.imprint","IMPRINT",FACE,{"disambiguationData":[TD([[makeQuery(id+"F141.imprint","IMPRINT",EDGE,{"derivedFrom":sQuery(id+"F141.wireOp",EDGE,"E272.sketch_text.stroke-31")}),-1.0]])]});
            var Q2;
            Q2=makeQuery(id+"F141.imprint","IMPRINT",FACE,{"disambiguationData":[TD([[makeQuery(id+"F141.imprint","IMPRINT",EDGE,{"derivedFrom":sQuery(id+"F141.wireOp",EDGE,"E272.sketch_text.stroke-45")}),-1.0]])]});
            var Q3;
            Q3=makeQuery(id+"F141.imprint","IMPRINT",FACE,{"disambiguationData":[TD([[makeQuery(id+"F141.imprint","IMPRINT",EDGE,{"derivedFrom":sQuery(id+"F141.wireOp",EDGE,"E272.sketch_text.stroke-69")}),-1.0]])]});
            extrude(context, id + "F142", {"entities" : qUnion([Q0, Q1, Q2, Q3]), "operationType" : NewBodyOperationType.REMOVE, "oppositeDirection" : true, "depth" : 2 * mm, "offsetDistance" : 25 * mm});
        }
        {
            var Q0;
            Q0=makeQuery(id+"F2.opExtrude","SWEPT_FACE",FACE,{"disambiguationData":[OSD([sQuery(id+"F0.wireOp",EDGE,"E93")])]});
            var sketch = newSketch(context, id + "F143", { "sketchPlane" : qUnion([Q0])});
            skText(sketch, "E273", { "text": "69", "fontName": "AllertaStencil-Regular.ttf"});
            const initialGuessF143  = {"E273": [-0.04676, 0.01668, 1, 0, 0.00394]};
            skSetInitialGuess(sketch, initialGuessF143);
            skSolve(sketch);
        }
        {
            var Q0;
            Q0=makeQuery(id+"F143.imprint","IMPRINT",FACE,{"disambiguationData":[TD([[makeQuery(id+"F143.imprint","IMPRINT",EDGE,{"derivedFrom":sQuery(id+"F143.wireOp",EDGE,"E273.sketch_text.stroke-0")}),-1.0]])]});
            var Q1;
            Q1=makeQuery(id+"F143.imprint","IMPRINT",FACE,{"disambiguationData":[TD([[makeQuery(id+"F143.imprint","IMPRINT",EDGE,{"derivedFrom":sQuery(id+"F143.wireOp",EDGE,"E273.sketch_text.stroke-31")}),-1.0]])]});
            var Q2;
            Q2=makeQuery(id+"F143.imprint","IMPRINT",FACE,{"disambiguationData":[TD([[makeQuery(id+"F143.imprint","IMPRINT",EDGE,{"derivedFrom":sQuery(id+"F143.wireOp",EDGE,"E273.sketch_text.stroke-45")}),-1.0]])]});
            var Q3;
            Q3=makeQuery(id+"F143.imprint","IMPRINT",FACE,{"disambiguationData":[TD([[makeQuery(id+"F143.imprint","IMPRINT",EDGE,{"derivedFrom":sQuery(id+"F143.wireOp",EDGE,"E273.sketch_text.stroke-59")}),-1.0]])]});
            extrude(context, id + "F144", {"entities" : qUnion([Q0, Q1, Q2, Q3]), "operationType" : NewBodyOperationType.REMOVE, "oppositeDirection" : true, "depth" : 1.4 * mm, "offsetDistance" : 25 * mm});
        }
        {
            var Q0;
            Q0=makeQuery(id+"F2.opExtrude","SWEPT_FACE",FACE,{"disambiguationData":[OSD([sQuery(id+"F0.wireOp",EDGE,"E54")])]});
            var sketch = newSketch(context, id + "F145", { "sketchPlane" : qUnion([Q0])});
            skText(sketch, "E274", { "text": "70", "fontName": "AllertaStencil-Regular.ttf"});
            const initialGuessF145  = {"E274": [-0.11158, 0.00778, 1, 0, 0.01173]};
            skSetInitialGuess(sketch, initialGuessF145);
            skSolve(sketch);
        }
        {
            var Q0;
            Q0=makeQuery(id+"F145.imprint","IMPRINT",FACE,{"disambiguationData":[TD([[makeQuery(id+"F145.imprint","IMPRINT",EDGE,{"derivedFrom":sQuery(id+"F145.wireOp",EDGE,"E274.sketch_text.stroke-0")}),-1.0]])]});
            var Q1;
            Q1=makeQuery(id+"F145.imprint","IMPRINT",FACE,{"disambiguationData":[TD([[makeQuery(id+"F145.imprint","IMPRINT",EDGE,{"derivedFrom":sQuery(id+"F145.wireOp",EDGE,"E274.sketch_text.stroke-6")}),-1.0]])]});
            var Q2;
            Q2=makeQuery(id+"F145.imprint","IMPRINT",FACE,{"disambiguationData":[TD([[makeQuery(id+"F145.imprint","IMPRINT",EDGE,{"derivedFrom":sQuery(id+"F145.wireOp",EDGE,"E274.sketch_text.stroke-22")}),-1.0]])]});
            extrude(context, id + "F146", {"entities" : qUnion([Q0, Q1, Q2]), "operationType" : NewBodyOperationType.REMOVE, "oppositeDirection" : true, "depth" : 2 * mm, "offsetDistance" : 25 * mm});
        }
        {
            var Q0;
            Q0=makeQuery(id+"F2.opExtrude","SWEPT_FACE",FACE,{"disambiguationData":[OSD([sQuery(id+"F0.wireOp",EDGE,"E55")])]});
            var sketch = newSketch(context, id + "F147", { "sketchPlane" : qUnion([Q0])});
            skText(sketch, "E275", { "text": "71\n", "fontName": "AllertaStencil-Regular.ttf"});
            const initialGuessF147  = {"E275": [-0.13813, 0.00532, 1, 0, 0.0141]};
            skSetInitialGuess(sketch, initialGuessF147);
            skSolve(sketch);
        }
        {
            var Q0;
            Q0=makeQuery(id+"F147.imprint","IMPRINT",FACE,{"disambiguationData":[TD([[makeQuery(id+"F147.imprint","IMPRINT",EDGE,{"derivedFrom":sQuery(id+"F147.wireOp",EDGE,"E275.sketch_text.stroke-0")}),-1.0]])]});
            var Q1;
            Q1=makeQuery(id+"F147.imprint","IMPRINT",FACE,{"disambiguationData":[TD([[makeQuery(id+"F147.imprint","IMPRINT",EDGE,{"derivedFrom":sQuery(id+"F147.wireOp",EDGE,"E275.sketch_text.stroke-6")}),-1.0]])]});
            extrude(context, id + "F148", {"entities" : qUnion([Q0, Q1]), "operationType" : NewBodyOperationType.REMOVE, "oppositeDirection" : true, "depth" : 2 * mm, "offsetDistance" : 25 * mm});
        }
        {
            var Q0;
            Q0=makeQuery(id+"F2.opExtrude","SWEPT_FACE",FACE,{"disambiguationData":[OSD([sQuery(id+"F0.wireOp",EDGE,"E95")])]});
            var sketch = newSketch(context, id + "F149", { "sketchPlane" : qUnion([Q0])});
            skText(sketch, "E276", { "text": "7", "fontName": "AllertaStencil-Regular.ttf"});
            skText(sketch, "E277", { "text": "2", "fontName": "AllertaStencil-Regular.ttf"});
            const initialGuessF149  = {"E276": [-0.05199, 0.01437, 1, 0, 0.00878], "E277": [-0.05114, 0.0049, 1, 0, 0.00748]};
            skSetInitialGuess(sketch, initialGuessF149);
            skSolve(sketch);
        }
        {
            var Q0;
            Q0=makeQuery(id+"F149.imprint","IMPRINT",FACE,{"disambiguationData":[TD([[makeQuery(id+"F149.imprint","IMPRINT",EDGE,{"derivedFrom":sQuery(id+"F149.wireOp",EDGE,"E276.sketch_text.stroke-0")}),-1.0]])]});
            var Q1;
            Q1=makeQuery(id+"F149.imprint","IMPRINT",FACE,{"disambiguationData":[TD([[makeQuery(id+"F149.imprint","IMPRINT",EDGE,{"derivedFrom":sQuery(id+"F149.wireOp",EDGE,"E277.sketch_text.stroke-0")}),-1.0]])]});
            extrude(context, id + "F150", {"entities" : qUnion([Q0, Q1]), "operationType" : NewBodyOperationType.REMOVE, "oppositeDirection" : true, "depth" : 2 * mm, "offsetDistance" : 25 * mm});
        }
        {
            var Q0;
            Q0=makeQuery(id+"F2.opExtrude","SWEPT_FACE",FACE,{"disambiguationData":[OSD([sQuery(id+"F0.wireOp",EDGE,"E89")])]});
            var sketch = newSketch(context, id + "F151", { "sketchPlane" : qUnion([Q0])});
            skText(sketch, "E278", { "text": "7", "fontName": "AllertaStencil-Regular.ttf"});
            skText(sketch, "E279", { "text": "3", "fontName": "AllertaStencil-Regular.ttf"});
            const initialGuessF151  = {"E278": [0.02842, 0.01697, 1, 0, 0.00604], "E279": [0.02842, 0.00965, 1, 0, 0.00558]};
            skSetInitialGuess(sketch, initialGuessF151);
            skSolve(sketch);
        }
        {
            var Q0;
            Q0=makeQuery(id+"F151.imprint","IMPRINT",FACE,{"disambiguationData":[TD([[makeQuery(id+"F151.imprint","IMPRINT",EDGE,{"derivedFrom":sQuery(id+"F151.wireOp",EDGE,"E278.sketch_text.stroke-0")}),-1.0]])]});
            var Q1;
            Q1=makeQuery(id+"F151.imprint","IMPRINT",FACE,{"disambiguationData":[TD([[makeQuery(id+"F151.imprint","IMPRINT",EDGE,{"derivedFrom":sQuery(id+"F151.wireOp",EDGE,"E279.sketch_text.stroke-0")}),-1.0]])]});
            extrude(context, id + "F152", {"entities" : qUnion([Q0, Q1]), "operationType" : NewBodyOperationType.REMOVE, "oppositeDirection" : true, "depth" : 2 * mm, "offsetDistance" : 25 * mm});
        }
        {
            var Q0;
            Q0=makeQuery(id+"F2.opExtrude","SWEPT_FACE",FACE,{"disambiguationData":[OSD([sQuery(id+"F0.wireOp",EDGE,"E202")])]});
            var sketch = newSketch(context, id + "F153", { "sketchPlane" : qUnion([Q0])});
            skText(sketch, "E280", { "text": "7", "fontName": "AllertaStencil-Regular.ttf"});
            skText(sketch, "E281", { "text": "4", "fontName": "AllertaStencil-Regular.ttf"});
            const initialGuessF153  = {"E280": [0.04054, 0.01536, 1, 0, 0.00652], "E281": [0.04054, 0.00742, 1, 0, 0.00618]};
            skSetInitialGuess(sketch, initialGuessF153);
            skSolve(sketch);
        }
        {
            var Q0;
            Q0=makeQuery(id+"F153.imprint","IMPRINT",FACE,{"disambiguationData":[TD([[makeQuery(id+"F153.imprint","IMPRINT",EDGE,{"derivedFrom":sQuery(id+"F153.wireOp",EDGE,"E280.sketch_text.stroke-0")}),-1.0]])]});
            var Q1;
            Q1=makeQuery(id+"F153.imprint","IMPRINT",FACE,{"disambiguationData":[TD([[makeQuery(id+"F153.imprint","IMPRINT",EDGE,{"derivedFrom":sQuery(id+"F153.wireOp",EDGE,"E281.sketch_text.stroke-8")}),-1.0]])]});
            var Q2;
            Q2=makeQuery(id+"F153.imprint","IMPRINT",FACE,{"disambiguationData":[TD([[makeQuery(id+"F153.imprint","IMPRINT",EDGE,{"derivedFrom":sQuery(id+"F153.wireOp",EDGE,"E281.sketch_text.stroke-0")}),-1.0]])]});
            extrude(context, id + "F154", {"entities" : qUnion([Q0, Q1, Q2]), "operationType" : NewBodyOperationType.REMOVE, "oppositeDirection" : true, "depth" : 2 * mm, "offsetDistance" : 25 * mm});
        }
        {
            var Q0;
            Q0=makeQuery(id+"F2.opExtrude","SWEPT_FACE",FACE,{"disambiguationData":[OSD([sQuery(id+"F0.wireOp",EDGE,"E87")])]});
            var sketch = newSketch(context, id + "F155", { "sketchPlane" : qUnion([Q0])});
            skText(sketch, "E282", { "text": "7", "fontName": "AllertaStencil-Regular.ttf"});
            skPoint(sketch, "E282.firstSnap0", {"position": v(31.65, 25) * mm});
            skText(sketch, "E283", { "text": "5", "fontName": "AllertaStencil-Regular.ttf"});
            const initialGuessF155  = {"E282": [0.03165, 0.01661, 1, 0, 0.00634], "E283": [0.03165, 0.0077, 1, 0, 0.00676]};
            skSetInitialGuess(sketch, initialGuessF155);
            skSolve(sketch);
        }
        {
            var Q0;
            Q0=makeQuery(id+"F155.imprint","IMPRINT",FACE,{"disambiguationData":[TD([[makeQuery(id+"F155.imprint","IMPRINT",EDGE,{"derivedFrom":sQuery(id+"F155.wireOp",EDGE,"E282.sketch_text.stroke-0")}),-1.0]])]});
            var Q1;
            Q1=makeQuery(id+"F155.imprint","IMPRINT",FACE,{"disambiguationData":[TD([[makeQuery(id+"F155.imprint","IMPRINT",EDGE,{"derivedFrom":sQuery(id+"F155.wireOp",EDGE,"E283.sketch_text.stroke-26")}),-1.0]])]});
            var Q2;
            Q2=makeQuery(id+"F155.imprint","IMPRINT",FACE,{"disambiguationData":[TD([[makeQuery(id+"F155.imprint","IMPRINT",EDGE,{"derivedFrom":sQuery(id+"F155.wireOp",EDGE,"E283.sketch_text.stroke-0")}),-1.0]])]});
            extrude(context, id + "F156", {"entities" : qUnion([Q0, Q1, Q2]), "operationType" : NewBodyOperationType.REMOVE, "oppositeDirection" : true, "depth" : 2 * mm, "offsetDistance" : 25 * mm});
        }
    });
